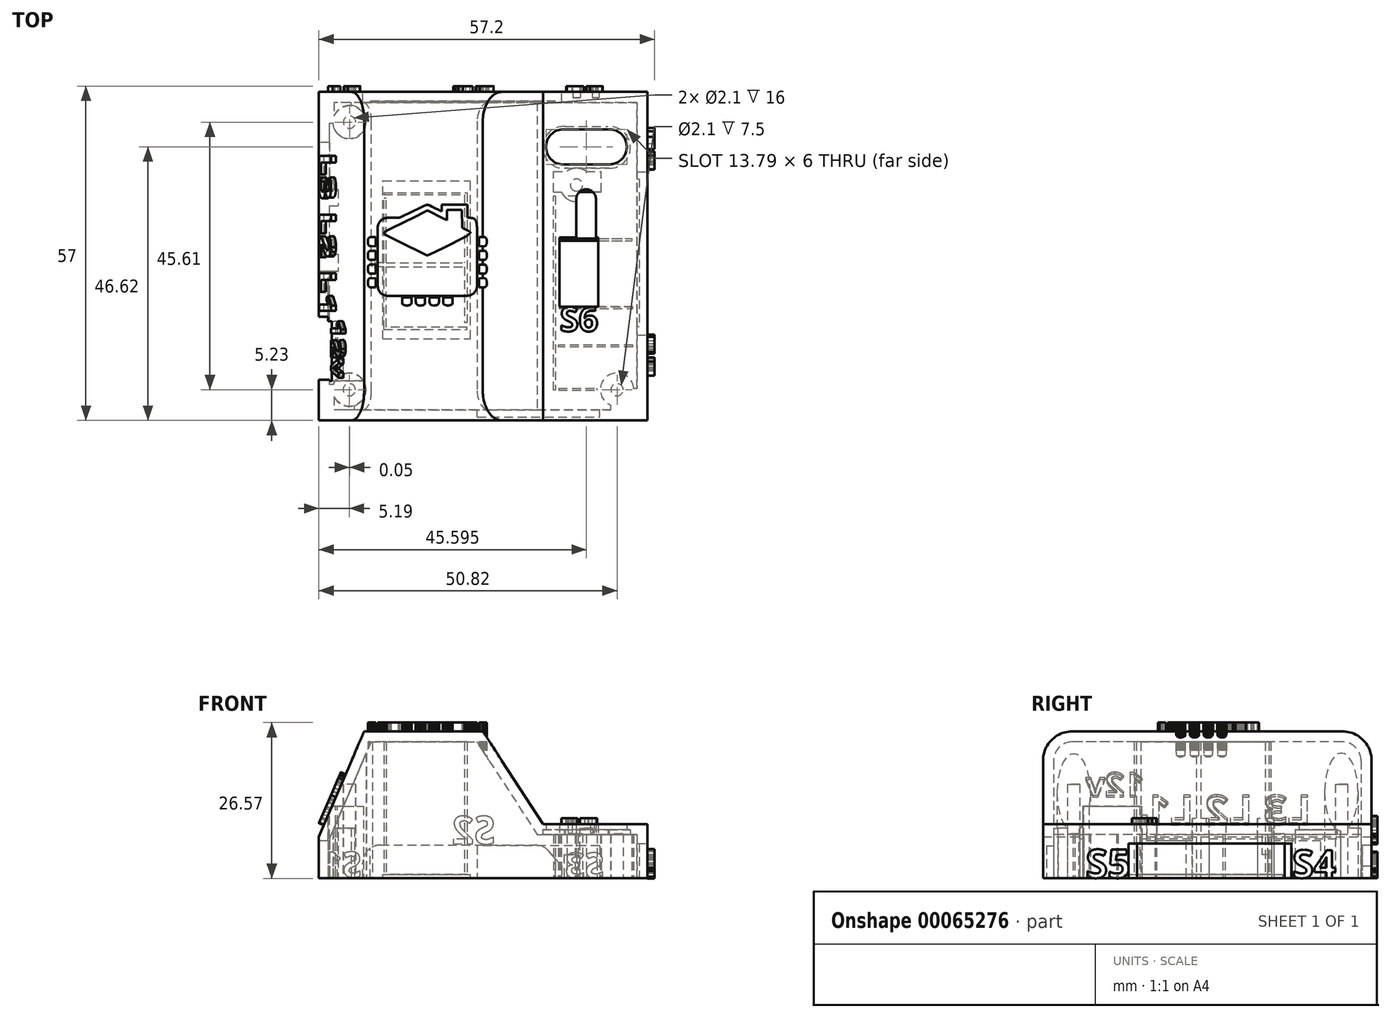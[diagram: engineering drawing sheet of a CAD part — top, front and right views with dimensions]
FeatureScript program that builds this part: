
annotation { "Feature Type Name" : "Feature", "Feature Type Description" : "" }
export const myFeature = defineFeature(function(context is Context, id is Id, definition is map)
    precondition{}
    {
        {
            var Q0;
            Q0=qCreatedBy(makeId("Top.planeOp"),FACE);
            var sketch = newSketch(context, id + "F0", { "sketchPlane" : qUnion([Q0])});
            skLineSegment(sketch, "E0.rect.bottom", {"start": v(22.84, -21.13) * mm, "end": v(-26.83, -21.13) * mm});
            skLineSegment(sketch, "E0.rect.top", {"start": v(22.84, 28.7) * mm, "end": v(-26.83, 28.7) * mm});
            skLineSegment(sketch, "E0.rect.left", {"start": v(22.84, -21.13) * mm, "end": v(22.84, 28.7) * mm});
            skPoint(sketch, "E0.rect.middle", {"position": v(-2, 3.78) * mm});
            skCircle(sketch, "E1", {"center": v(-24.81, -18.99) * mm, "radius": 1.05 * mm});
            skCircle(sketch, "E2", {"center": v(-24.76, 26.62) * mm, "radius": 1.05 * mm});
            skCircle(sketch, "E3", {"center": v(13.92, 15.91) * mm, "radius": 1.05 * mm});
            skLineSegment(sketch, "E4", {"start": v(-2, -21.13) * mm, "end": v(-2, -18.21) * mm});
            skCircle(sketch, "E5.MirrorC", {"center": v(20.82, -18.99) * mm, "radius": 1.05 * mm});
            skLineSegment(sketch, "E6.rect.bottom", {"start": v(24.75, -22.97) * mm, "end": v(-28.75, -22.97) * mm});
            skLineSegment(sketch, "E6.rect.top", {"start": v(24.75, 30.53) * mm, "end": v(-28.75, 30.53) * mm});
            skLineSegment(sketch, "E6.rect.left", {"start": v(24.75, -22.97) * mm, "end": v(24.75, 30.53) * mm});
            skLineSegment(sketch, "E6.rect.right", {"start": v(-28.75, -22.97) * mm, "end": v(-28.75, 30.53) * mm});
            skLineSegment(sketch, "E7.rect.bottom", {"start": v(26, -24.22) * mm, "end": v(-30, -24.22) * mm});
            skLineSegment(sketch, "E7.rect.top", {"start": v(26, 31.78) * mm, "end": v(-30, 31.78) * mm});
            skLineSegment(sketch, "E7.rect.left", {"start": v(26, -24.22) * mm, "end": v(26, 31.78) * mm});
            skLineSegment(sketch, "E7.rect.right", {"start": v(-30, -24.22) * mm, "end": v(-30, 31.78) * mm});
            skPoint(sketch, "E8", {"position": v(8.65, 14) * mm});
            skSolve(sketch);
        }
        {
            var Q0;
            Q0=qSketchRegion(id+"F0",true);
            var Q1;
            Q1=makeQuery(id+"F0.imprint","IMPRINT",FACE,{"disambiguationData":[TD([[makeQuery(id+"F0.imprint","IMPRINT",EDGE,{"derivedFrom":sQuery(id+"F0.wireOp",EDGE,"E1")}),-1.0]])]});
            extrude(context, id + "F1", {"entities" : qUnion([Q0, Q1]), "depth" : 25 * mm});
        }
        {
            var Q0;
            Q0=qCreatedBy(makeId("Front.planeOp"),FACE);
            var sketch = newSketch(context, id + "F2", { "sketchPlane" : qUnion([Q0])});
            skLineSegment(sketch, "E9", {"start": v(0, 0) * mm, "end": v(0, 7) * mm});
            skLineSegment(sketch, "E10", {"start": v(0, 7) * mm, "end": v(26.03, 7) * mm});
            skLineSegment(sketch, "E11", {"start": v(26.03, 9.19) * mm, "end": v(26.03, 25.51) * mm});
            skLineSegment(sketch, "E12", {"start": v(15.3, 7) * mm, "end": v(26.03, 7) * mm});
            skLineSegment(sketch, "E13", {"start": v(0, 7) * mm, "end": v(-30.02, 7) * mm});
            skLineSegment(sketch, "E14", {"start": v(-30.02, 7) * mm, "end": v(-22.06, 25.51) * mm});
            skLineSegment(sketch, "E15", {"start": v(-22.06, 25.51) * mm, "end": v(-2.39, 25.51) * mm});
            skLineSegment(sketch, "E16", {"start": v(26.03, 25.51) * mm, "end": v(-2.39, 25.51) * mm});
            skLineSegment(sketch, "E17", {"start": v(-22.06, 25.51) * mm, "end": v(-30.02, 25.51) * mm});
            skLineSegment(sketch, "E18", {"start": v(-30.02, 25.51) * mm, "end": v(-30.02, 7) * mm});
            skLineSegment(sketch, "E19", {"start": v(18.06, 10.7) * mm, "end": v(18.04, 10.7) * mm});
            skLineSegment(sketch, "E20", {"start": v(19.86, 9.19) * mm, "end": v(8.2, 9.19) * mm});
            skLineSegment(sketch, "E21", {"start": v(8.2, 9.19) * mm, "end": v(-2.39, 25.51) * mm});
            skLineSegment(sketch, "E22", {"start": v(19.86, 9.19) * mm, "end": v(26.03, 9.19) * mm});
            skSolve(sketch);
        }
        {
            var Q0;
            Q0=makeQuery(id+"F2.imprint","IMPRINT",FACE,{"disambiguationData":[TD([[makeQuery(id+"F2.imprint","IMPRINT",EDGE,{"derivedFrom":sQuery(id+"F2.wireOp",EDGE,"E14")}),1.0]])]});
            var Q1;
            {var subQ0=sQuery(id+"F2.wireOp",EDGE,"E11");Q1=makeQuery(id+"F2.imprint","IMPRINT",FACE,{"disambiguationData":[TD([[makeQuery(id+"F2.imprint","IMPRINT",EDGE,{"derivedFrom":subQ0}),1.0]])]});}
            extrude(context, id + "F3", {"entities" : qUnion([Q0, Q1]), "operationType" : NewBodyOperationType.REMOVE, "endBound" : BoundingType.UP_TO_NEXT, "oppositeDirection" : true, "depth" : 25 * mm, "hasSecondDirection" : true, "secondDirectionOppositeDirection" : false, "secondDirectionDepth" : 25 * mm});
        }
        {
            var Q0;
            Q0=makeQuery(id+"F1.opExtrude","CAP_EDGE",EDGE,{"disambiguationData":[OSD([sQuery(id+"F0.wireOp",EDGE,"E7.rect.right")])],"isStart":false});
            var Q1;
            Q1=makeQuery(id+"F3.boolean.opBoolean","COPY",EDGE,{"derivedFrom":makeQuery(id+"F3.opExtrude","TWEAK_EDGE",EDGE,{"derivedFrom":[makeQuery(id+"F1.opExtrude","CAP_FACE",FACE,{"disambiguationData":[OSD([sQuery(id+"F0.wireOp",EDGE,"E1"),sQuery(id+"F0.wireOp",EDGE,"E2"),sQuery(id+"F0.wireOp",EDGE,"E3"),sQuery(id+"F0.wireOp",EDGE,"E5.MirrorC"),sQuery(id+"F0.wireOp",EDGE,"E7.rect.bottom"),sQuery(id+"F0.wireOp",EDGE,"E7.rect.top"),sQuery(id+"F0.wireOp",EDGE,"E7.rect.left"),sQuery(id+"F0.wireOp",EDGE,"E7.rect.right")])],"isStart":false}),makeQuery(id+"F2.imprint","IMPRINT",EDGE,{"derivedFrom":sQuery(id+"F2.wireOp",EDGE,"ff17f17f-c23f-4b7b-92e3-773d52701edb")})]})});
            var Q2;
            Q2=makeQuery(id+"F3.boolean.opBoolean","COPY",EDGE,{"derivedFrom":makeQuery(id+"F3.opExtrude","TWEAK_EDGE",EDGE,{"derivedFrom":[makeQuery(id+"F1.opExtrude","CAP_FACE",FACE,{"disambiguationData":[OSD([sQuery(id+"F0.wireOp",EDGE,"E1"),sQuery(id+"F0.wireOp",EDGE,"E2"),sQuery(id+"F0.wireOp",EDGE,"E3"),sQuery(id+"F0.wireOp",EDGE,"E5.MirrorC"),sQuery(id+"F0.wireOp",EDGE,"E7.rect.bottom"),sQuery(id+"F0.wireOp",EDGE,"E7.rect.top"),sQuery(id+"F0.wireOp",EDGE,"E7.rect.left"),sQuery(id+"F0.wireOp",EDGE,"E7.rect.right")])],"isStart":false}),makeQuery(id+"F2.imprint","IMPRINT",EDGE,{"derivedFrom":sQuery(id+"F2.wireOp",EDGE,"7c30f75c-de24-4105-9ec6-0528e7197d9e")})]})});
            var Q3;
            {var subQ0=sQuery(id+"F2.wireOp",EDGE,"cpQ2IQLn-lepx-jHqE-Occg-QwCyzWVKbBFz");var subQ1=sQuery(id+"F2.wireOp",EDGE,"9136473a-ce9f-4df1-8e41-d79c079f6f02");var subQ2=makeQuery(id+"F2.imprint","INTERSECT",VERTEX,{"disambiguationData":[OD(0.0)],"derivedFrom":[subQ1,subQ0]});var subQ4=makeQuery(id+"F2.imprint","INTERSECT",VERTEX,{"disambiguationData":[OD(1.0)],"derivedFrom":[subQ1,subQ0]});Q3=makeQuery(id+"F3.boolean.opBoolean","COPY",EDGE,{"derivedFrom":makeQuery(id+"F3.opExtrude","TWEAK_EDGE",EDGE,{"derivedFrom":[makeQuery(id+"F1.opExtrude","CAP_FACE",FACE,{"disambiguationData":[OSD([sQuery(id+"F0.wireOp",EDGE,"E1"),sQuery(id+"F0.wireOp",EDGE,"E2"),sQuery(id+"F0.wireOp",EDGE,"E3"),sQuery(id+"F0.wireOp",EDGE,"E5.MirrorC"),sQuery(id+"F0.wireOp",EDGE,"E7.rect.bottom"),sQuery(id+"F0.wireOp",EDGE,"E7.rect.top"),sQuery(id+"F0.wireOp",EDGE,"E7.rect.left"),sQuery(id+"F0.wireOp",EDGE,"E7.rect.right")])],"isStart":false}),makeQuery(id+"F2.imprint","IMPRINT",EDGE,{"disambiguationData":[TD([[subQ4,1.0]])],"derivedFrom":subQ0}),makeQuery(id+"F2.imprint","IMPRINT",EDGE,{"disambiguationData":[TD([[subQ2,1.0]])],"derivedFrom":subQ0}),makeQuery(id+"F2.imprint","IMPRINT",EDGE,{"disambiguationData":[TD([[subQ2,-1.0]])],"derivedFrom":subQ0})]})});}
            var Q4;
            {var subQ0=sQuery(id+"F2.wireOp",EDGE,"cpQ2IQLn-lepx-jHqE-Occg-QwCyzWVKbBFz");var subQ1=sQuery(id+"F2.wireOp",EDGE,"9136473a-ce9f-4df1-8e41-d79c079f6f02");var subQ2=makeQuery(id+"F2.imprint","INTERSECT",VERTEX,{"disambiguationData":[OD(0.0)],"derivedFrom":[subQ1,subQ0]});var subQ3=sQuery(id+"F2.wireOp",EDGE,"7c30f75c-de24-4105-9ec6-0528e7197d9e");var subQ4=makeQuery(id+"F2.imprint","INTERSECT",VERTEX,{"derivedFrom":[subQ3,subQ0]});var subQ5=makeQuery(id+"F2.imprint","INTERSECT",VERTEX,{"disambiguationData":[OD(1.0)],"derivedFrom":[subQ1,subQ0]});Q4=makeQuery(id+"F3.boolean.opBoolean","COPY",EDGE,{"derivedFrom":makeQuery(id+"F3.opExtrude","TWEAK_EDGE",EDGE,{"disambiguationData":[OD(0.0)],"derivedFrom":[makeQuery(id+"F2.imprint","IMPRINT",EDGE,{"disambiguationData":[TD([[subQ4,1.0]])],"derivedFrom":subQ3}),makeQuery(id+"F2.imprint","IMPRINT",EDGE,{"disambiguationData":[TD([[subQ5,1.0]])],"derivedFrom":subQ0}),makeQuery(id+"F2.imprint","IMPRINT",EDGE,{"disambiguationData":[TD([[subQ2,1.0]])],"derivedFrom":subQ0}),makeQuery(id+"F2.imprint","IMPRINT",EDGE,{"disambiguationData":[TD([[subQ2,-1.0]])],"derivedFrom":subQ0})]})});}
            var Q5;
            {var subQ0=sQuery(id+"F2.wireOp",EDGE,"cpQ2IQLn-lepx-jHqE-Occg-QwCyzWVKbBFz");var subQ1=sQuery(id+"F2.wireOp",EDGE,"9136473a-ce9f-4df1-8e41-d79c079f6f02");var subQ2=makeQuery(id+"F2.imprint","INTERSECT",VERTEX,{"disambiguationData":[OD(0.0)],"derivedFrom":[subQ1,subQ0]});var subQ3=sQuery(id+"F2.wireOp",EDGE,"7c30f75c-de24-4105-9ec6-0528e7197d9e");var subQ4=makeQuery(id+"F2.imprint","INTERSECT",VERTEX,{"derivedFrom":[subQ3,subQ0]});var subQ5=makeQuery(id+"F2.imprint","INTERSECT",VERTEX,{"disambiguationData":[OD(1.0)],"derivedFrom":[subQ1,subQ0]});Q5=makeQuery(id+"F3.boolean.opBoolean","COPY",EDGE,{"derivedFrom":makeQuery(id+"F3.opExtrude","TWEAK_EDGE",EDGE,{"disambiguationData":[OD(1.0)],"derivedFrom":[makeQuery(id+"F2.imprint","IMPRINT",EDGE,{"disambiguationData":[TD([[subQ4,1.0]])],"derivedFrom":subQ3}),makeQuery(id+"F2.imprint","IMPRINT",EDGE,{"disambiguationData":[TD([[subQ5,1.0]])],"derivedFrom":subQ0}),makeQuery(id+"F2.imprint","IMPRINT",EDGE,{"disambiguationData":[TD([[subQ2,1.0]])],"derivedFrom":subQ0}),makeQuery(id+"F2.imprint","IMPRINT",EDGE,{"disambiguationData":[TD([[subQ2,-1.0]])],"derivedFrom":subQ0})]})});}
            var Q6;
            Q6=makeQuery(id+"F1.opExtrude","CAP_EDGE",EDGE,{"disambiguationData":[OSD([sQuery(id+"F0.wireOp",EDGE,"E7.rect.bottom")])],"isStart":false});
            var Q7;
            {var subQ0=sQuery(id+"F2.wireOp",EDGE,"cpQ2IQLn-lepx-jHqE-Occg-QwCyzWVKbBFz");var subQ1=sQuery(id+"F2.wireOp",EDGE,"9136473a-ce9f-4df1-8e41-d79c079f6f02");var subQ2=makeQuery(id+"F2.imprint","INTERSECT",VERTEX,{"disambiguationData":[OD(0.0)],"derivedFrom":[subQ1,subQ0]});var subQ4=makeQuery(id+"F2.imprint","INTERSECT",VERTEX,{"disambiguationData":[OD(1.0)],"derivedFrom":[subQ1,subQ0]});Q7=makeQuery(id+"F3.boolean.opBoolean","COPY",EDGE,{"derivedFrom":makeQuery(id+"F3.opExtrude","TWEAK_EDGE",EDGE,{"derivedFrom":[makeQuery(id+"F1.opExtrude","SWEPT_FACE",FACE,{"disambiguationData":[OSD([sQuery(id+"F0.wireOp",EDGE,"E7.rect.bottom")])]}),makeQuery(id+"F2.imprint","IMPRINT",EDGE,{"disambiguationData":[TD([[subQ4,1.0]])],"derivedFrom":subQ0}),makeQuery(id+"F2.imprint","IMPRINT",EDGE,{"disambiguationData":[TD([[subQ2,1.0]])],"derivedFrom":subQ0}),makeQuery(id+"F2.imprint","IMPRINT",EDGE,{"disambiguationData":[TD([[subQ2,-1.0]])],"derivedFrom":subQ0})]})});}
            var Q8;
            Q8=makeQuery(id+"F1.opExtrude","CAP_EDGE",EDGE,{"disambiguationData":[OSD([sQuery(id+"F0.wireOp",EDGE,"E7.rect.top")])],"isStart":false});
            var Q9;
            {var subQ0=sQuery(id+"F2.wireOp",EDGE,"cpQ2IQLn-lepx-jHqE-Occg-QwCyzWVKbBFz");var subQ1=sQuery(id+"F2.wireOp",EDGE,"9136473a-ce9f-4df1-8e41-d79c079f6f02");var subQ2=makeQuery(id+"F2.imprint","INTERSECT",VERTEX,{"disambiguationData":[OD(0.0)],"derivedFrom":[subQ1,subQ0]});var subQ4=makeQuery(id+"F2.imprint","INTERSECT",VERTEX,{"disambiguationData":[OD(1.0)],"derivedFrom":[subQ1,subQ0]});Q9=makeQuery(id+"F3.boolean.opBoolean","COPY",EDGE,{"derivedFrom":makeQuery(id+"F3.opExtrude","TWEAK_EDGE",EDGE,{"derivedFrom":[makeQuery(id+"F1.opExtrude","SWEPT_FACE",FACE,{"disambiguationData":[OSD([sQuery(id+"F0.wireOp",EDGE,"E7.rect.top")])]}),makeQuery(id+"F2.imprint","IMPRINT",EDGE,{"disambiguationData":[TD([[subQ4,1.0]])],"derivedFrom":subQ0}),makeQuery(id+"F2.imprint","IMPRINT",EDGE,{"disambiguationData":[TD([[subQ2,1.0]])],"derivedFrom":subQ0}),makeQuery(id+"F2.imprint","IMPRINT",EDGE,{"disambiguationData":[TD([[subQ2,-1.0]])],"derivedFrom":subQ0})]})});}
            var Q10;
            Q10=makeQuery(id+"F3.boolean.opBoolean","COPY",EDGE,{"derivedFrom":makeQuery(id+"F3.opExtrude","TWEAK_EDGE",EDGE,{"derivedFrom":[makeQuery(id+"F1.opExtrude","CAP_FACE",FACE,{"disambiguationData":[OSD([sQuery(id+"F0.wireOp",EDGE,"E1"),sQuery(id+"F0.wireOp",EDGE,"E2"),sQuery(id+"F0.wireOp",EDGE,"E3"),sQuery(id+"F0.wireOp",EDGE,"E5.MirrorC"),sQuery(id+"F0.wireOp",EDGE,"E7.rect.bottom"),sQuery(id+"F0.wireOp",EDGE,"E7.rect.top"),sQuery(id+"F0.wireOp",EDGE,"E7.rect.left"),sQuery(id+"F0.wireOp",EDGE,"E7.rect.right")])],"isStart":false}),makeQuery(id+"F2.imprint","IMPRINT",EDGE,{"derivedFrom":sQuery(id+"F2.wireOp",EDGE,"99fa5713-44e2-4710-8a3e-a5a5802f03ed")})]})});
            var Q11;
            Q11=makeQuery(id+"F3.boolean.opBoolean","COPY",EDGE,{"derivedFrom":makeQuery(id+"F3.opExtrude","TWEAK_EDGE",EDGE,{"derivedFrom":[makeQuery(id+"F1.opExtrude","CAP_FACE",FACE,{"disambiguationData":[OSD([sQuery(id+"F0.wireOp",EDGE,"E1"),sQuery(id+"F0.wireOp",EDGE,"E2"),sQuery(id+"F0.wireOp",EDGE,"E3"),sQuery(id+"F0.wireOp",EDGE,"E5.MirrorC"),sQuery(id+"F0.wireOp",EDGE,"E7.rect.bottom"),sQuery(id+"F0.wireOp",EDGE,"E7.rect.top"),sQuery(id+"F0.wireOp",EDGE,"E7.rect.left"),sQuery(id+"F0.wireOp",EDGE,"E7.rect.right")])],"isStart":false}),makeQuery(id+"F2.imprint","IMPRINT",EDGE,{"derivedFrom":sQuery(id+"F2.wireOp",EDGE,"E14")})]})});
            var Q12;
            Q12=makeQuery(id+"F3.boolean.opBoolean","COPY",EDGE,{"derivedFrom":makeQuery(id+"F3.opExtrude","TWEAK_EDGE",EDGE,{"derivedFrom":[makeQuery(id+"F1.opExtrude","CAP_FACE",FACE,{"disambiguationData":[OSD([sQuery(id+"F0.wireOp",EDGE,"E1"),sQuery(id+"F0.wireOp",EDGE,"E2"),sQuery(id+"F0.wireOp",EDGE,"E3"),sQuery(id+"F0.wireOp",EDGE,"E5.MirrorC"),sQuery(id+"F0.wireOp",EDGE,"E7.rect.bottom"),sQuery(id+"F0.wireOp",EDGE,"E7.rect.top"),sQuery(id+"F0.wireOp",EDGE,"E7.rect.left"),sQuery(id+"F0.wireOp",EDGE,"E7.rect.right")])],"isStart":false}),makeQuery(id+"F2.imprint","IMPRINT",EDGE,{"derivedFrom":sQuery(id+"F2.wireOp",EDGE,"E21")})]})});
            var Q13;
            Q13=makeQuery(id+"F3.boolean.opBoolean","COPY",EDGE,{"derivedFrom":makeQuery(id+"F3.opExtrude","TWEAK_EDGE",EDGE,{"derivedFrom":[makeQuery(id+"F2.imprint","IMPRINT",EDGE,{"derivedFrom":sQuery(id+"F2.wireOp",EDGE,"E20")}),makeQuery(id+"F2.imprint","IMPRINT",EDGE,{"derivedFrom":sQuery(id+"F2.wireOp",EDGE,"E21")})]})});
            var Q14;
            Q14=makeQuery(id+"F3.boolean.opBoolean","COPY",EDGE,{"derivedFrom":makeQuery(id+"F3.opExtrude","TWEAK_EDGE",EDGE,{"derivedFrom":[makeQuery(id+"F1.opExtrude","SWEPT_FACE",FACE,{"disambiguationData":[OSD([sQuery(id+"F0.wireOp",EDGE,"E7.rect.bottom")])]}),makeQuery(id+"F2.imprint","IMPRINT",EDGE,{"derivedFrom":sQuery(id+"F2.wireOp",EDGE,"E21")})]})});
            var Q15;
            Q15=makeQuery(id+"F3.boolean.opBoolean","COPY",EDGE,{"derivedFrom":makeQuery(id+"F3.opExtrude","TWEAK_EDGE",EDGE,{"derivedFrom":[makeQuery(id+"F1.opExtrude","SWEPT_FACE",FACE,{"disambiguationData":[OSD([sQuery(id+"F0.wireOp",EDGE,"E7.rect.top")])]}),makeQuery(id+"F2.imprint","IMPRINT",EDGE,{"derivedFrom":sQuery(id+"F2.wireOp",EDGE,"E21")})]})});
            var Q16;
            Q16=makeQuery(id+"F3.boolean.opBoolean","COPY",EDGE,{"derivedFrom":makeQuery(id+"F3.opExtrude","TWEAK_EDGE",EDGE,{"derivedFrom":[makeQuery(id+"F1.opExtrude","SWEPT_FACE",FACE,{"disambiguationData":[OSD([sQuery(id+"F0.wireOp",EDGE,"E7.rect.left")])]}),makeQuery(id+"F2.imprint","IMPRINT",EDGE,{"derivedFrom":sQuery(id+"F2.wireOp",EDGE,"E20")}),makeQuery(id+"F2.imprint","IMPRINT",EDGE,{"derivedFrom":sQuery(id+"F2.wireOp",EDGE,"E22")})]})});
            var Q17;
            Q17=makeQuery(id+"F3.boolean.opBoolean","COPY",EDGE,{"derivedFrom":makeQuery(id+"F3.opExtrude","TWEAK_EDGE",EDGE,{"derivedFrom":[makeQuery(id+"F2.imprint","IMPRINT",EDGE,{"derivedFrom":sQuery(id+"F2.wireOp",EDGE,"E20")}),makeQuery(id+"F2.imprint","IMPRINT",EDGE,{"derivedFrom":sQuery(id+"F2.wireOp",EDGE,"E21")}),makeQuery(id+"F2.imprint","IMPRINT",EDGE,{"derivedFrom":sQuery(id+"F2.wireOp",EDGE,"E22")})]})});
            fillet(context, id + "F4", {"entities" : qUnion([Q0, Q1, Q2, Q3, Q4, Q5, Q6, Q7, Q8, Q9, Q10, Q11, Q12, Q13, Q14, Q15, Q16, Q17]), "radius" : 5 * mm, "tangentPropagation" : true, "allowEdgeOverflow" : false});
        }
        {
            var Q0;
            Q0=makeQuery(id+"F1.opExtrude","SWEPT_BODY",BODY,{"disambiguationData":[OSD([sQuery(id+"F0.wireOp",EDGE,"E1"),sQuery(id+"F0.wireOp",EDGE,"E2"),sQuery(id+"F0.wireOp",EDGE,"E3"),sQuery(id+"F0.wireOp",EDGE,"E5.MirrorC"),sQuery(id+"F0.wireOp",EDGE,"E7.rect.bottom"),sQuery(id+"F0.wireOp",EDGE,"E7.rect.top"),sQuery(id+"F0.wireOp",EDGE,"E7.rect.left"),sQuery(id+"F0.wireOp",EDGE,"E7.rect.right")])]});
            transform(context, id + "F5", {"entities" : qUnion([Q0]), "transformType" : TransformType.TRANSLATION_3D, "dx" : -5 * mm, "dy" : -12 * mm, "dz" : 0 * mm, "makeCopy" : false});
        }
        {
            var Q0;
            Q0=makeQuery(id+"F1.opExtrude","CAP_FACE",FACE,{"disambiguationData":[OSD([sQuery(id+"F0.wireOp",EDGE,"E1"),sQuery(id+"F0.wireOp",EDGE,"E2"),sQuery(id+"F0.wireOp",EDGE,"E3"),sQuery(id+"F0.wireOp",EDGE,"E5.MirrorC"),sQuery(id+"F0.wireOp",EDGE,"E7.rect.bottom"),sQuery(id+"F0.wireOp",EDGE,"E7.rect.top"),sQuery(id+"F0.wireOp",EDGE,"E7.rect.left"),sQuery(id+"F0.wireOp",EDGE,"E7.rect.right")])],"isStart":true});
            shell(context, id + "F6", {"entities" : qUnion([Q0]), "thickness" : 1.8 * mm});
        }
        {
            var Q0;
            Q0=makeQuery(id+"F1.opExtrude","SWEPT_FACE",FACE,{"disambiguationData":[OSD([sQuery(id+"F0.wireOp",EDGE,"E7.rect.left")])]});
            cPlane(context, id + "F7", {"entities" : qUnion([Q0]), "cplaneType" : CPlaneType.OFFSET, "offset" : 0 * mm, "width" : 150 * mm, "height" : 150 * mm});
        }
        {
            var Q0;
            Q0=qCreatedBy(id+"F7.planeOp",FACE);
            var sketch = newSketch(context, id + "F8", { "sketchPlane" : qUnion([Q0])});
            skLineSegment(sketch, "E23.bottom", {"start": v(6.92, 0) * mm, "end": v(-20.2, 0) * mm});
            skLineSegment(sketch, "E23.top", {"start": v(6.12, 5.87) * mm, "end": v(-20.2, 5.87) * mm});
            skLineSegment(sketch, "E24", {"start": v(-20.2, 5.87) * mm, "end": v(-21.64, 5.87) * mm});
            skLineSegment(sketch, "E25", {"start": v(-21.64, 5.87) * mm, "end": v(-21.64, 0) * mm});
            skLineSegment(sketch, "E26", {"start": v(-21.64, 0) * mm, "end": v(-20.2, 0) * mm});
            skLineSegment(sketch, "E27", {"start": v(-20.2, 5.87) * mm, "end": v(-20.2, 0) * mm});
            skLineSegment(sketch, "E28", {"start": v(6.12, 5.87) * mm, "end": v(6.12, 0) * mm});
            skPoint(sketch, "E29.orphan", {"position": v(7.84, 0) * mm});
            skLineSegment(sketch, "E30", {"start": v(4.97, 0) * mm, "end": v(4.97, 5.87) * mm});
            skSolve(sketch);
        }
        {
            var Q0;
            Q0=qSketchRegion(id+"F8",true);
            extrude(context, id + "F9", {"entities" : qUnion([Q0]), "operationType" : NewBodyOperationType.REMOVE, "oppositeDirection" : true, "depth" : (1.7 - 0.3) * mm});
        }
        {
            var Q0;
            Q0=makeQuery(id+"F8.imprint","IMPRINT",FACE,{"disambiguationData":[TD([[makeQuery(id+"F8.imprint","IMPRINT",EDGE,{"derivedFrom":sQuery(id+"F8.wireOp",EDGE,"E24")}),1.0]])]});
            var Q1;
            {var subQ0=sQuery(id+"F8.wireOp",EDGE,"E23.left");Q1=makeQuery(id+"F8.imprint","IMPRINT",FACE,{"disambiguationData":[TD([[makeQuery(id+"F8.imprint","IMPRINT",EDGE,{"derivedFrom":subQ0}),1.0]])]});}
            var Q2;
            {var subQ0=sQuery(id+"F8.wireOp",EDGE,"4UiORLbo-slaH-JSft-xh6I-61qYCNnPId7j");Q2=makeQuery(id+"F8.imprint","IMPRINT",FACE,{"disambiguationData":[TD([[makeQuery(id+"F8.imprint","IMPRINT",EDGE,{"derivedFrom":subQ0}),1.0]])]});}
            var Q3;
            {var subQ0=sQuery(id+"F8.wireOp",EDGE,"E28");Q3=makeQuery(id+"F8.imprint","IMPRINT",FACE,{"disambiguationData":[TD([[makeQuery(id+"F8.imprint","IMPRINT",EDGE,{"derivedFrom":subQ0}),-1.0]])]});}
            extrude(context, id + "F10", {"entities" : qUnion([Q0, Q1, Q2, Q3]), "operationType" : NewBodyOperationType.REMOVE, "oppositeDirection" : true, "depth" : 2 * mm});
        }
        {
            var Q0;
            Q0=makeQuery(id+"F1.opExtrude","SWEPT_FACE",FACE,{"disambiguationData":[OSD([sQuery(id+"F0.wireOp",EDGE,"E7.rect.right")])]});
            cPlane(context, id + "F11", {"entities" : qUnion([Q0]), "cplaneType" : CPlaneType.OFFSET, "offset" : 0 * mm, "width" : 150 * mm, "height" : 150 * mm});
        }
        {
            var Q0;
            Q0=qCreatedBy(id+"F11.planeOp",FACE);
            var sketch = newSketch(context, id + "F12", { "sketchPlane" : qUnion([Q0])});
            skLineSegment(sketch, "E31.top", {"start": v(-11.15, 6.31) * mm, "end": v(-3.45, 6.31) * mm});
            skLineSegment(sketch, "E32", {"start": v(27.25, 11.15) * mm, "end": v(27.25, 11.15) * mm});
            skLineSegment(sketch, "E33", {"start": v(-11.15, 0) * mm, "end": v(-11.15, 6.31) * mm});
            skPoint(sketch, "E34.start.orphan", {"position": v(-15.15, 0) * mm});
            skLineSegment(sketch, "E35", {"start": v(29.28, 0) * mm, "end": v(-11.15, 0) * mm});
            skLineSegment(sketch, "E36", {"start": v(-10.29, 6.31) * mm, "end": v(-10.29, 0) * mm});
            skLineSegment(sketch, "E37", {"start": v(19.35, 12.2) * mm, "end": v(29.28, 12.2) * mm});
            skLineSegment(sketch, "E38", {"start": v(-11.15, 3.16) * mm, "end": v(-3.45, 3.16) * mm, "construction": true});
            skLineSegment(sketch, "E39", {"start": v(-3.45, 3.16) * mm, "end": v(-0.05, 3.16) * mm, "construction": true});
            skLineSegment(sketch, "E40", {"start": v(-0.05, 3.16) * mm, "end": v(7.65, 3.16) * mm, "construction": true});
            skLineSegment(sketch, "E41", {"start": v(7.65, 3.16) * mm, "end": v(11.05, 3.16) * mm, "construction": true});
            skLineSegment(sketch, "E42.trimOffspring", {"start": v(11.05, 6.31) * mm, "end": v(18.53, 6.31) * mm});
            skLineSegment(sketch, "E43", {"start": v(11.9, 6.31) * mm, "end": v(11.9, 0) * mm});
            skLineSegment(sketch, "E44", {"start": v(0, 6.31) * mm, "end": v(7.65, 6.31) * mm});
            skLineSegment(sketch, "E45", {"start": v(7.65, 0) * mm, "end": v(0, 0) * mm});
            skLineSegment(sketch, "E46", {"start": v(-3.45, 0) * mm, "end": v(-11.15, 0) * mm});
            skLineSegment(sketch, "E47", {"start": v(30.08, 0) * mm, "end": v(11.05, 0) * mm});
            skLineSegment(sketch, "E48.bottom", {"start": v(-0.32, 0) * mm, "end": v(-3.15, 0) * mm});
            skLineSegment(sketch, "E48.top", {"start": v(-0.32, 6.31) * mm, "end": v(-3.15, 6.31) * mm});
            skLineSegment(sketch, "E48.left", {"start": v(-0.32, 0) * mm, "end": v(-0.32, 6.31) * mm});
            skLineSegment(sketch, "E48.right", {"start": v(-3.15, 0) * mm, "end": v(-3.15, 6.31) * mm});
            skLineSegment(sketch, "E49.bottom", {"start": v(10.8, 0) * mm, "end": v(7.92, 0) * mm});
            skLineSegment(sketch, "E49.top", {"start": v(10.8, 6.31) * mm, "end": v(7.92, 6.31) * mm});
            skLineSegment(sketch, "E49.left", {"start": v(10.8, 0) * mm, "end": v(10.8, 6.31) * mm});
            skLineSegment(sketch, "E49.right", {"start": v(7.92, 0) * mm, "end": v(7.92, 6.31) * mm});
            skLineSegment(sketch, "E50", {"start": v(-3.45, 6.31) * mm, "end": v(11.05, 6.31) * mm});
            skLineSegment(sketch, "E51", {"start": v(29.28, 12.2) * mm, "end": v(29.28, 0) * mm});
            skPoint(sketch, "E52.end.orphan", {"position": v(30.08, 11.15) * mm});
            skPoint(sketch, "E52.start.orphan", {"position": v(30.08, 12.2) * mm});
            skLineSegment(sketch, "E53", {"start": v(18.53, 6.31) * mm, "end": v(18.53, 12.2) * mm});
            skLineSegment(sketch, "E54", {"start": v(18.53, 12.2) * mm, "end": v(19.35, 12.2) * mm});
            skPoint(sketch, "E55.start.orphan", {"position": v(19.35, 11.15) * mm});
            skPoint(sketch, "E56.end.orphan", {"position": v(19.35, 0) * mm});
            skPoint(sketch, "E56.start.orphan", {"position": v(19.35, 6.31) * mm});
            skLineSegment(sketch, "E57", {"start": v(28.38, 0) * mm, "end": v(28.38, 12.2) * mm});
            skLineSegment(sketch, "E58", {"start": v(19.35, 12.2) * mm, "end": v(19.35, 0) * mm});
            skSolve(sketch);
        }
        {
            var Q0;
            {var subQ0=sQuery(id+"F12.wireOp",EDGE,"E33");Q0=makeQuery(id+"F12.imprint","IMPRINT",FACE,{"disambiguationData":[TD([[makeQuery(id+"F12.imprint","IMPRINT",EDGE,{"derivedFrom":subQ0}),-1.0]])]});}
            var Q1;
            {var subQ1=sQuery(id+"F12.wireOp",EDGE,"E36");Q1=makeQuery(id+"F12.imprint","IMPRINT",FACE,{"disambiguationData":[TD([[makeQuery(id+"F12.imprint","IMPRINT",EDGE,{"derivedFrom":subQ1}),1.0]])]});}
            var Q2;
            {var subQ0=sQuery(id+"F12.wireOp",EDGE,"LVVauTd6-uSLQ-SWm0-nvuu-HrEgJgk2loCY");Q2=makeQuery(id+"F12.imprint","IMPRINT",FACE,{"disambiguationData":[TD([[makeQuery(id+"F12.imprint","IMPRINT",EDGE,{"derivedFrom":subQ0}),-1.0]])]});}
            var Q3;
            Q3=makeQuery(id+"F12.imprint","IMPRINT",FACE,{"disambiguationData":[TD([[makeQuery(id+"F12.imprint","IMPRINT",EDGE,{"derivedFrom":sQuery(id+"F12.wireOp",EDGE,"Bzj0w9RH-aYdH-ZF7y-Z4mK-Pif1xP8myCSu")}),1.0]])]});
            var Q4;
            {var subQ2=sQuery(id+"F12.wireOp",EDGE,"E43");Q4=makeQuery(id+"F12.imprint","IMPRINT",FACE,{"disambiguationData":[TD([[makeQuery(id+"F12.imprint","IMPRINT",EDGE,{"derivedFrom":subQ2}),1.0]])]});}
            extrude(context, id + "F13", {"entities" : qUnion([Q0, Q1, Q2, Q3, Q4]), "operationType" : NewBodyOperationType.REMOVE, "oppositeDirection" : true, "depth" : 1.6 * mm});
        }
        {
            var Q0;
            {var subQ2=sQuery(id+"F12.wireOp",EDGE,"E57");Q0=makeQuery(id+"F12.imprint","IMPRINT",FACE,{"disambiguationData":[TD([[makeQuery(id+"F12.imprint","IMPRINT",EDGE,{"derivedFrom":subQ2}),1.0]])]});}
            var Q1;
            {var subQ0=sQuery(id+"F12.wireOp",EDGE,"E33");Q1=makeQuery(id+"F12.imprint","IMPRINT",FACE,{"disambiguationData":[TD([[makeQuery(id+"F12.imprint","IMPRINT",EDGE,{"derivedFrom":subQ0}),-1.0]])]});}
            var Q2;
            {var subQ1=sQuery(id+"F12.wireOp",EDGE,"E45");Q2=makeQuery(id+"F12.imprint","IMPRINT",FACE,{"disambiguationData":[TD([[makeQuery(id+"F12.imprint","IMPRINT",EDGE,{"derivedFrom":subQ1}),-1.0]])]});}
            var Q3;
            {var subQ3=sQuery(id+"F12.wireOp",EDGE,"E36");Q3=makeQuery(id+"F12.imprint","IMPRINT",FACE,{"disambiguationData":[TD([[makeQuery(id+"F12.imprint","IMPRINT",EDGE,{"derivedFrom":subQ3}),1.0]])]});}
            var Q4;
            {var subQ3=sQuery(id+"F12.wireOp",EDGE,"E43");Q4=makeQuery(id+"F12.imprint","IMPRINT",FACE,{"disambiguationData":[TD([[makeQuery(id+"F12.imprint","IMPRINT",EDGE,{"derivedFrom":subQ3}),-1.0]])]});}
            var Q5;
            {var subQ0=sQuery(id+"F12.wireOp",EDGE,"E51");Q5=makeQuery(id+"F12.imprint","IMPRINT",FACE,{"disambiguationData":[TD([[makeQuery(id+"F12.imprint","IMPRINT",EDGE,{"derivedFrom":subQ0}),-1.0]])]});}
            extrude(context, id + "F14", {"entities" : qUnion([Q0, Q1, Q2, Q3, Q4, Q5]), "operationType" : NewBodyOperationType.REMOVE, "oppositeDirection" : true, "depth" : 8 * mm});
        }
        {
            var Q0;
            Q0=qCreatedBy(makeId("Top.planeOp"),FACE);
            var sketch = newSketch(context, id + "F15", { "sketchPlane" : qUnion([Q0])});
            skLineSegment(sketch, "E59.bottom", {"start": v(-27.19, -29.45) * mm, "end": v(-33.17, -29.45) * mm});
            skLineSegment(sketch, "E59.top", {"start": v(-27.19, -20) * mm, "end": v(-33.17, -20) * mm});
            skLineSegment(sketch, "E59.left", {"start": v(-27.19, -29.45) * mm, "end": v(-27.19, -21.32) * mm});
            skLineSegment(sketch, "E59.right", {"start": v(-33.17, -29.45) * mm, "end": v(-33.17, -21.32) * mm});
            skLineSegment(sketch, "E60", {"start": v(-33.17, -20.99) * mm, "end": v(-27.19, -20.99) * mm});
            skLineSegment(sketch, "E61", {"start": v(-33.17, -21.32) * mm, "end": v(-27.19, -21.32) * mm});
            skLineSegment(sketch, "E62.trimOffspring", {"start": v(-27.19, -20.99) * mm, "end": v(-27.19, -20) * mm});
            skLineSegment(sketch, "E63.trimOffspring", {"start": v(-33.17, -20.99) * mm, "end": v(-33.17, -20) * mm});
            skSolve(sketch);
        }
        {
            var Q0;
            Q0=qSketchRegion(id+"F15",true);
            var Q1;
            {var subQ0=sQuery(id+"F12.wireOp",EDGE,"E37");Q1=makeQuery(id+"F14.boolean.opBoolean","COPY",FACE,{"derivedFrom":makeQuery(id+"F14.opExtrude","SWEPT_FACE",FACE,{"disambiguationData":[OSD([subQ0]),TDD([makeQuery(id+"F12.imprint","IMPRINT",EDGE,{"disambiguationData":[TD([[makeQuery(id+"F12.imprint","INTERSECT",VERTEX,{"derivedFrom":[subQ0,sQuery(id+"F12.wireOp",EDGE,"E52")]}),1.0]])],"derivedFrom":subQ0})])]})});}
            extrude(context, id + "F16", {"entities" : qUnion([Q0]), "operationType" : NewBodyOperationType.REMOVE, "endBound" : BoundingType.UP_TO_SURFACE, "endBoundEntityFace" : qUnion([Q1]), "depth" : 11.3 * mm});
        }
        {
            var Q0;
            Q0=makeQuery(id+"F1.opExtrude","SWEPT_FACE",FACE,{"disambiguationData":[OSD([sQuery(id+"F0.wireOp",EDGE,"E7.rect.top")])]});
            cPlane(context, id + "F17", {"entities" : qUnion([Q0]), "cplaneType" : CPlaneType.OFFSET, "offset" : 0 * mm, "width" : 150 * mm, "height" : 150 * mm});
        }
        {
            var Q0;
            Q0=qCreatedBy(id+"F17.planeOp",FACE);
            var sketch = newSketch(context, id + "F18", { "sketchPlane" : qUnion([Q0])});
            skLineSegment(sketch, "E64.bottom", {"start": v(-6.36, 0) * mm, "end": v(27.5, 0) * mm});
            skLineSegment(sketch, "E64.left", {"start": v(-6.36, 0) * mm, "end": v(-6.36, 2.05) * mm});
            skLineSegment(sketch, "E65", {"start": v(-5.32, 3.26) * mm, "end": v(-5.32, 0) * mm});
            skLineSegment(sketch, "E66", {"start": v(27.5, 2.61) * mm, "end": v(27.5, 0) * mm});
            skLineSegment(sketch, "E67", {"start": v(26.27, 5.04) * mm, "end": v(26.27, 0) * mm});
            skPoint(sketch, "E68.visualSharp", {"position": v(-6.36, 7.05) * mm});
            skLineSegment(sketch, "E69", {"start": v(-6.36, 2.05) * mm, "end": v(-4.17, 4.58) * mm});
            skLineSegment(sketch, "E70", {"start": v(24.5, 5.61) * mm, "end": v(-1.9, 5.61) * mm});
            skPoint(sketch, "E71.visualSharp", {"position": v(-3.28, 5.61) * mm});
            skArc(sketch, "E71.filletArc", {"start": v(-1.9, 5.61) * mm, "mid": v(-3.15, 5.34) * mm, "end": v(-4.17, 4.58) * mm});
            skPoint(sketch, "E72.visualSharp", {"position": v(27.5, 5.61) * mm});
            skArc(sketch, "E72.filletArc", {"start": v(27.5, 2.61) * mm, "mid": v(26.63, 4.73) * mm, "end": v(24.5, 5.61) * mm});
            skSolve(sketch);
        }
        {
            var Q0;
            Q0=qSketchRegion(id+"F18",true);
            extrude(context, id + "F19", {"entities" : qUnion([Q0]), "operationType" : NewBodyOperationType.REMOVE, "oppositeDirection" : true, "depth" : 1.6 * mm});
        }
        {
            var Q0;
            Q0=qCreatedBy(makeId("Top.planeOp"),FACE);
            var sketch = newSketch(context, id + "F20", { "sketchPlane" : qUnion([Q0])});
            skArc(sketch, "E73", {"start": v(6.16, 2.02) * mm, "mid": v(8.9, 0.56) * mm, "end": v(11.63, 2.02) * mm});
            skLineSegment(sketch, "E74", {"start": v(11.63, 2.02) * mm, "end": v(6.16, 2.02) * mm});
            skSolve(sketch);
        }
        {
            var Q0;
            Q0=qSketchRegion(id+"F20",true);
            extrude(context, id + "F21", {"entities" : qUnion([Q0]), "operationType" : NewBodyOperationType.REMOVE, "depth" : 4 * mm});
        }
        {
            var Q0;
            {var subQ0=sQuery(id+"F18.wireOp",EDGE,"E64.left");Q0=makeQuery(id+"F18.imprint","IMPRINT",FACE,{"disambiguationData":[TD([[makeQuery(id+"F18.imprint","IMPRINT",EDGE,{"derivedFrom":subQ0}),-1.0]])]});}
            var Q1;
            {var subQ0=sQuery(id+"F18.wireOp",EDGE,"E64.right");Q1=makeQuery(id+"F18.imprint","IMPRINT",FACE,{"disambiguationData":[TD([[makeQuery(id+"F18.imprint","IMPRINT",EDGE,{"derivedFrom":subQ0}),1.0]])]});}
            extrude(context, id + "F22", {"entities" : qUnion([Q0, Q1]), "operationType" : NewBodyOperationType.REMOVE, "oppositeDirection" : true, "depth" : 2 * mm});
        }
        {
            var Q0;
            Q0=qCreatedBy(makeId("Top.planeOp"),FACE);
            var sketch = newSketch(context, id + "F23", { "sketchPlane" : qUnion([Q0])});
            skLineSegment(sketch, "E75", {"start": v(21, 19.9) * mm, "end": v(21, 10.4) * mm, "construction": true});
            skLineSegment(sketch, "E76", {"start": v(12.22, 0) * mm, "end": v(12.22, -5.06) * mm});
            skLineSegment(sketch, "E77", {"start": v(12.22, 0) * mm, "end": v(12.22, 1.5) * mm});
            skArc(sketch, "E78", {"start": v(14.47, 7.42) * mm, "mid": v(17.49, 10.4) * mm, "end": v(14.5, 13.4) * mm});
            skArc(sketch, "E79", {"start": v(6.7, 13.4) * mm, "mid": v(3.7, 10.4) * mm, "end": v(6.7, 7.4) * mm});
            skLineSegment(sketch, "E80", {"start": v(14.5, 13.4) * mm, "end": v(6.7, 13.4) * mm});
            skLineSegment(sketch, "E81", {"start": v(6.7, 7.4) * mm, "end": v(14.54, 7.42) * mm});
            skLineSegment(sketch, "E82", {"start": v(6, -5.57) * mm, "end": v(6, -16.85) * mm});
            skLineSegment(sketch, "E83", {"start": v(12.6, -16.85) * mm, "end": v(6, -16.85) * mm});
            skPoint(sketch, "E84.center.orphan", {"position": v(10.72, -16.85) * mm});
            skLineSegment(sketch, "E85", {"start": v(12.6, -5.57) * mm, "end": v(12.6, -16.85) * mm});
            skLineSegment(sketch, "E86", {"start": v(8.87, -5.06) * mm, "end": v(8.87, 1.5) * mm});
            skArc(sketch, "E87", {"start": v(12.22, 1.5) * mm, "mid": v(10.54, 3.17) * mm, "end": v(8.87, 1.5) * mm});
            skPoint(sketch, "E88.orphan", {"position": v(12.22, -16.85) * mm});
            skLineSegment(sketch, "E89", {"start": v(0, 0) * mm, "end": v(0, 19.9) * mm, "construction": true});
            skLineSegment(sketch, "E90", {"start": v(0, 19.9) * mm, "end": v(21, 19.9) * mm, "construction": true});
            skLineSegment(sketch, "E91", {"start": v(14.5, 10.4) * mm, "end": v(21, 10.4) * mm, "construction": true});
            skLineSegment(sketch, "E92", {"start": v(8.87, -5.06) * mm, "end": v(6, -5.06) * mm});
            skLineSegment(sketch, "E93", {"start": v(6, -5.06) * mm, "end": v(6, -5.57) * mm});
            skLineSegment(sketch, "E94", {"start": v(12.22, -5.06) * mm, "end": v(12.6, -5.06) * mm});
            skLineSegment(sketch, "E95", {"start": v(12.6, -5.06) * mm, "end": v(12.6, -5.57) * mm});
            skSolve(sketch);
        }
        {
            var Q0;
            Q0=qSketchRegion(id+"F23",true);
            extrude(context, id + "F24", {"entities" : qUnion([Q0]), "operationType" : NewBodyOperationType.REMOVE, "depth" : 25 * mm});
        }
        {
            var Q0;
            Q0=qCreatedBy(makeId("Top.planeOp"),FACE);
            var sketch = newSketch(context, id + "F25", { "sketchPlane" : qUnion([Q0])});
            skLineSegment(sketch, "E96", {"start": v(18.49, -17.16) * mm, "end": v(5.97, -17.16) * mm});
            skLineSegment(sketch, "E97", {"start": v(18.49, -16.86) * mm, "end": v(5.97, -16.86) * mm});
            skLineSegment(sketch, "E98", {"start": v(12.44, -31.08) * mm, "end": v(5.87, -31.08) * mm});
            skLineSegment(sketch, "E99", {"start": v(12.44, -30.78) * mm, "end": v(5.87, -30.78) * mm});
            skLineSegment(sketch, "E100.bottom", {"start": v(-33.84, 14.47) * mm, "end": v(-32.16, 14.47) * mm});
            skLineSegment(sketch, "E100.top", {"start": v(-33.84, 18.7) * mm, "end": v(-29.5, 18.7) * mm});
            skLineSegment(sketch, "E100.left", {"start": v(-33.84, 14.47) * mm, "end": v(-33.84, 18.7) * mm});
            skLineSegment(sketch, "E100.right", {"start": v(-29.5, 16.74) * mm, "end": v(-29.5, 18.7) * mm});
            skArc(sketch, "E101", {"start": v(-29.5, 16.74) * mm, "mid": v(-31.35, 16.22) * mm, "end": v(-32.16, 14.47) * mm});
            skLineSegment(sketch, "E102.bottom", {"start": v(-33.6, -31.08) * mm, "end": v(-33.6, -31.08) * mm});
            skLineSegment(sketch, "E102.top", {"start": v(-33.6, -34.81) * mm, "end": v(-31.03, -34.81) * mm});
            skLineSegment(sketch, "E102.left", {"start": v(-33.6, -31.08) * mm, "end": v(-33.6, -34.81) * mm});
            skLineSegment(sketch, "E102.right", {"start": v(-31.03, -31.08) * mm, "end": v(-31.03, -33.21) * mm});
            skLineSegment(sketch, "E103.bottom", {"start": v(-31.03, -34.81) * mm, "end": v(-28.95, -34.81) * mm});
            skLineSegment(sketch, "E103.top", {"start": v(-31.03, -33.21) * mm, "end": v(-28.95, -33.21) * mm});
            skLineSegment(sketch, "E103.right", {"start": v(-28.95, -34.81) * mm, "end": v(-28.95, -33.21) * mm});
            skPoint(sketch, "E104.end.orphan", {"position": v(-34.98, -31.08) * mm});
            skPoint(sketch, "E104.start.orphan", {"position": v(-34.98, -30.78) * mm});
            skLineSegment(sketch, "E105.bottom", {"start": v(16.87, -34.88) * mm, "end": v(19.69, -34.88) * mm});
            skLineSegment(sketch, "E105.top", {"start": v(16.87, -30.79) * mm, "end": v(19.69, -30.79) * mm});
            skLineSegment(sketch, "E105.left", {"start": v(16.87, -33.4) * mm, "end": v(16.87, -30.79) * mm});
            skLineSegment(sketch, "E105.right", {"start": v(19.69, -34.88) * mm, "end": v(19.69, -30.79) * mm});
            skLineSegment(sketch, "E106.bottom", {"start": v(16.87, -34.88) * mm, "end": v(14.73, -34.88) * mm});
            skLineSegment(sketch, "E106.top", {"start": v(16.87, -33.4) * mm, "end": v(14.73, -33.4) * mm});
            skLineSegment(sketch, "E106.right", {"start": v(14.73, -34.88) * mm, "end": v(14.73, -33.4) * mm});
            skLineSegment(sketch, "E107.top", {"start": v(-31.03, -30.09) * mm, "end": v(-33.6, -30.09) * mm});
            skLineSegment(sketch, "E107.left", {"start": v(-31.03, -31.08) * mm, "end": v(-31.03, -30.09) * mm});
            skLineSegment(sketch, "E107.right", {"start": v(-33.6, -31.08) * mm, "end": v(-33.6, -30.09) * mm});
            skLineSegment(sketch, "E108", {"start": v(5.87, -31.08) * mm, "end": v(5.87, -30.78) * mm});
            skPoint(sketch, "E109.end.orphan", {"position": v(-34.98, -17.16) * mm});
            skPoint(sketch, "E109.start.orphan", {"position": v(-34.98, -16.86) * mm});
            skLineSegment(sketch, "E110.trimOffspring", {"start": v(5.97, -17.16) * mm, "end": v(5.97, -16.86) * mm});
            skLineSegment(sketch, "E111.bottom", {"start": v(5.85, -23.4) * mm, "end": v(18.49, -23.4) * mm});
            skLineSegment(sketch, "E111.top", {"start": v(5.85, -23.7) * mm, "end": v(18.49, -23.7) * mm});
            skLineSegment(sketch, "E111.left", {"start": v(5.85, -23.4) * mm, "end": v(5.85, -23.7) * mm});
            skLineSegment(sketch, "E112", {"start": v(5.29, -31.08) * mm, "end": v(5.29, 2.03) * mm});
            skLineSegment(sketch, "E113", {"start": v(4.99, -31.08) * mm, "end": v(5.29, -31.08) * mm});
            skLineSegment(sketch, "E114", {"start": v(12.44, -30.78) * mm, "end": v(12.44, -31.08) * mm});
            skLineSegment(sketch, "E115", {"start": v(18.49, -16.86) * mm, "end": v(18.49, -17.16) * mm});
            skPoint(sketch, "E116.orphan", {"position": v(19.24, -17.16) * mm});
            skLineSegment(sketch, "E117.trimOffspring", {"start": v(18.49, -23.4) * mm, "end": v(18.49, -23.7) * mm});
            skPoint(sketch, "E118.orphan", {"position": v(19.24, -23.7) * mm});
            skLineSegment(sketch, "E119.trimOffspring", {"start": v(4.99, 2.03) * mm, "end": v(4.99, -31.08) * mm});
            skLineSegment(sketch, "E120", {"start": v(4.99, 2.03) * mm, "end": v(5.29, 2.03) * mm});
            skLineSegment(sketch, "E121.bottom", {"start": v(4.99, 2.73) * mm, "end": v(13.12, 2.73) * mm});
            skLineSegment(sketch, "E121.top", {"start": v(4.99, 6.24) * mm, "end": v(13.12, 6.24) * mm});
            skLineSegment(sketch, "E121.left", {"start": v(4.99, 2.73) * mm, "end": v(4.99, 6.24) * mm});
            skLineSegment(sketch, "E121.right", {"start": v(13.12, 2.73) * mm, "end": v(13.12, 6.24) * mm});
            skCircle(sketch, "E122", {"center": v(8.91, 3.9) * mm, "radius": 1.04 * mm});
            skPoint(sketch, "E122.first.point", {"position": v(8.9, 2.86) * mm});
            skPoint(sketch, "E122.second.point", {"position": v(8.95, 4.94) * mm});
            skPoint(sketch, "E122.third.point", {"position": v(9.95, 3.84) * mm});
            skSolve(sketch);
        }
        {
            var Q0;
            Q0=qSketchRegion(id+"F25",true);
            var Q1;
            Q1=makeQuery(id+"F6.opShell","OFFSET_FACE",FACE,{"disambiguationData":[OSD([sQuery(id+"F2.wireOp",EDGE,"E20"),sQuery(id+"F2.wireOp",EDGE,"E22")])]});
            extrude(context, id + "F26", {"entities" : qUnion([Q0]), "operationType" : NewBodyOperationType.ADD, "endBoundEntityFace" : qUnion([Q1]), "depth" : 8.5 * mm});
        }
        {
            var Q0;
            Q0=qCreatedBy(makeId("Top.planeOp"),FACE);
            var sketch = newSketch(context, id + "F27", { "sketchPlane" : qUnion([Q0])});
            skLineSegment(sketch, "E123", {"start": v(-14.06, 0.58) * mm, "end": v(-9.7, 0.57) * mm});
            skLineSegment(sketch, "E124", {"start": v(-8.04, -3.57) * mm, "end": v(-8.03, -3.84) * mm});
            skLineSegment(sketch, "E125", {"start": v(-8.03, -3.84) * mm, "end": v(-8.04, -13.15) * mm});
            skLineSegment(sketch, "E126", {"start": v(-8.04, -13.15) * mm, "end": v(-8.03, -13.22) * mm});
            skLineSegment(sketch, "E127", {"start": v(-8.03, -13.22) * mm, "end": v(-8.03, -13.28) * mm});
            skLineSegment(sketch, "E128", {"start": v(-8.03, -13.28) * mm, "end": v(-8.04, -13.35) * mm});
            skLineSegment(sketch, "E129", {"start": v(-8.04, -13.35) * mm, "end": v(-8.04, -13.42) * mm});
            skLineSegment(sketch, "E130", {"start": v(-8.04, -13.42) * mm, "end": v(-8.05, -13.48) * mm});
            skLineSegment(sketch, "E131", {"start": v(-8.05, -13.48) * mm, "end": v(-8.06, -13.55) * mm});
            skLineSegment(sketch, "E132", {"start": v(-8.06, -13.55) * mm, "end": v(-8.07, -13.61) * mm});
            skLineSegment(sketch, "E133", {"start": v(-8.07, -13.61) * mm, "end": v(-8.1, -13.68) * mm});
            skLineSegment(sketch, "E134", {"start": v(-8.1, -13.68) * mm, "end": v(-8.1, -13.74) * mm});
            skLineSegment(sketch, "E135", {"start": v(-8.1, -13.74) * mm, "end": v(-8.13, -13.8) * mm});
            skLineSegment(sketch, "E136", {"start": v(-8.13, -13.8) * mm, "end": v(-8.15, -13.86) * mm});
            skLineSegment(sketch, "E137", {"start": v(-8.15, -13.86) * mm, "end": v(-8.18, -13.93) * mm});
            skLineSegment(sketch, "E138", {"start": v(-8.18, -13.93) * mm, "end": v(-8.2, -13.99) * mm});
            skLineSegment(sketch, "E139", {"start": v(-8.2, -13.99) * mm, "end": v(-8.23, -14.05) * mm});
            skLineSegment(sketch, "E140", {"start": v(-8.23, -14.05) * mm, "end": v(-8.26, -14.1) * mm});
            skLineSegment(sketch, "E141", {"start": v(-8.26, -14.1) * mm, "end": v(-8.3, -14.16) * mm});
            skLineSegment(sketch, "E142", {"start": v(-8.3, -14.16) * mm, "end": v(-8.33, -14.22) * mm});
            skLineSegment(sketch, "E143", {"start": v(-8.33, -14.22) * mm, "end": v(-8.37, -14.27) * mm});
            skLineSegment(sketch, "E144", {"start": v(-8.37, -14.27) * mm, "end": v(-8.4, -14.32) * mm});
            skLineSegment(sketch, "E145", {"start": v(-8.4, -14.32) * mm, "end": v(-8.45, -14.37) * mm});
            skLineSegment(sketch, "E146", {"start": v(-8.45, -14.37) * mm, "end": v(-8.5, -14.42) * mm});
            skLineSegment(sketch, "E147", {"start": v(-8.5, -14.42) * mm, "end": v(-8.54, -14.47) * mm});
            skLineSegment(sketch, "E148", {"start": v(-8.54, -14.47) * mm, "end": v(-8.59, -14.52) * mm});
            skLineSegment(sketch, "E149", {"start": v(-8.59, -14.52) * mm, "end": v(-8.63, -14.56) * mm});
            skLineSegment(sketch, "E150", {"start": v(-8.63, -14.56) * mm, "end": v(-8.69, -14.6) * mm});
            skLineSegment(sketch, "E151", {"start": v(-8.69, -14.6) * mm, "end": v(-8.74, -14.64) * mm});
            skLineSegment(sketch, "E152", {"start": v(-8.74, -14.64) * mm, "end": v(-8.8, -14.68) * mm});
            skLineSegment(sketch, "E153", {"start": v(-8.8, -14.68) * mm, "end": v(-8.85, -14.72) * mm});
            skLineSegment(sketch, "E154", {"start": v(-8.85, -14.72) * mm, "end": v(-8.9, -14.75) * mm});
            skLineSegment(sketch, "E155", {"start": v(-8.9, -14.75) * mm, "end": v(-8.95, -14.77) * mm});
            skLineSegment(sketch, "E156", {"start": v(-8.95, -14.77) * mm, "end": v(-8.99, -14.8) * mm});
            skLineSegment(sketch, "E157", {"start": v(-8.99, -14.8) * mm, "end": v(-9.03, -14.81) * mm});
            skLineSegment(sketch, "E158", {"start": v(-9.03, -14.81) * mm, "end": v(-9.07, -14.83) * mm});
            skLineSegment(sketch, "E159", {"start": v(-9.07, -14.83) * mm, "end": v(-9.11, -14.85) * mm});
            skLineSegment(sketch, "E160", {"start": v(-9.11, -14.85) * mm, "end": v(-9.16, -14.86) * mm});
            skLineSegment(sketch, "E161", {"start": v(-9.16, -14.86) * mm, "end": v(-9.2, -14.88) * mm});
            skLineSegment(sketch, "E162", {"start": v(-9.2, -14.88) * mm, "end": v(-9.24, -14.9) * mm});
            skLineSegment(sketch, "E163", {"start": v(-9.24, -14.9) * mm, "end": v(-9.29, -14.9) * mm});
            skLineSegment(sketch, "E164", {"start": v(-9.29, -14.9) * mm, "end": v(-9.33, -14.91) * mm});
            skLineSegment(sketch, "E165", {"start": v(-9.33, -14.91) * mm, "end": v(-9.38, -14.92) * mm});
            skLineSegment(sketch, "E166", {"start": v(-9.38, -14.92) * mm, "end": v(-9.42, -14.93) * mm});
            skLineSegment(sketch, "E167", {"start": v(-9.42, -14.93) * mm, "end": v(-9.51, -14.94) * mm});
            skLineSegment(sketch, "E168", {"start": v(-9.51, -14.94) * mm, "end": v(-9.6, -14.96) * mm});
            skLineSegment(sketch, "E169", {"start": v(-9.6, -14.96) * mm, "end": v(-9.74, -14.97) * mm});
            skLineSegment(sketch, "E170", {"start": v(-9.74, -14.97) * mm, "end": v(-10.2, -14.98) * mm});
            skLineSegment(sketch, "E171", {"start": v(-10.2, -14.98) * mm, "end": v(-23.2, -14.97) * mm});
            skLineSegment(sketch, "E172", {"start": v(-23.2, -14.97) * mm, "end": v(-23.28, -14.97) * mm});
            skLineSegment(sketch, "E173", {"start": v(-23.28, -14.97) * mm, "end": v(-23.35, -14.97) * mm});
            skLineSegment(sketch, "E174", {"start": v(-23.35, -14.97) * mm, "end": v(-23.43, -14.97) * mm});
            skLineSegment(sketch, "E175", {"start": v(-23.43, -14.97) * mm, "end": v(-23.5, -14.96) * mm});
            skLineSegment(sketch, "E176", {"start": v(-23.5, -14.96) * mm, "end": v(-23.58, -14.94) * mm});
            skLineSegment(sketch, "E177", {"start": v(-23.58, -14.94) * mm, "end": v(-23.65, -14.93) * mm});
            skLineSegment(sketch, "E178", {"start": v(-23.65, -14.93) * mm, "end": v(-23.72, -14.9) * mm});
            skLineSegment(sketch, "E179", {"start": v(-23.72, -14.9) * mm, "end": v(-23.8, -14.89) * mm});
            skLineSegment(sketch, "E180", {"start": v(-23.8, -14.89) * mm, "end": v(-23.86, -14.86) * mm});
            skLineSegment(sketch, "E181", {"start": v(-23.86, -14.86) * mm, "end": v(-23.93, -14.83) * mm});
            skLineSegment(sketch, "E182", {"start": v(-23.93, -14.83) * mm, "end": v(-24, -14.8) * mm});
            skLineSegment(sketch, "E183", {"start": v(-24, -14.8) * mm, "end": v(-24.07, -14.77) * mm});
            skLineSegment(sketch, "E184", {"start": v(-24.07, -14.77) * mm, "end": v(-24.13, -14.73) * mm});
            skLineSegment(sketch, "E185", {"start": v(-24.13, -14.73) * mm, "end": v(-24.2, -14.7) * mm});
            skLineSegment(sketch, "E186", {"start": v(-24.2, -14.7) * mm, "end": v(-24.26, -14.65) * mm});
            skLineSegment(sketch, "E187", {"start": v(-24.26, -14.65) * mm, "end": v(-24.32, -14.6) * mm});
            skLineSegment(sketch, "E188", {"start": v(-24.32, -14.6) * mm, "end": v(-24.38, -14.56) * mm});
            skLineSegment(sketch, "E189", {"start": v(-24.38, -14.56) * mm, "end": v(-24.43, -14.51) * mm});
            skLineSegment(sketch, "E190", {"start": v(-24.43, -14.51) * mm, "end": v(-24.48, -14.46) * mm});
            skLineSegment(sketch, "E191", {"start": v(-24.48, -14.46) * mm, "end": v(-24.54, -14.4) * mm});
            skLineSegment(sketch, "E192", {"start": v(-24.54, -14.4) * mm, "end": v(-24.59, -14.35) * mm});
            skLineSegment(sketch, "E193", {"start": v(-24.59, -14.35) * mm, "end": v(-24.63, -14.3) * mm});
            skLineSegment(sketch, "E194", {"start": v(-24.63, -14.3) * mm, "end": v(-24.68, -14.23) * mm});
            skLineSegment(sketch, "E195", {"start": v(-24.68, -14.23) * mm, "end": v(-24.72, -14.17) * mm});
            skLineSegment(sketch, "E196", {"start": v(-24.72, -14.17) * mm, "end": v(-24.76, -14.1) * mm});
            skLineSegment(sketch, "E197", {"start": v(-24.76, -14.1) * mm, "end": v(-24.8, -14.04) * mm});
            skLineSegment(sketch, "E198", {"start": v(-24.8, -14.04) * mm, "end": v(-24.82, -13.97) * mm});
            skLineSegment(sketch, "E199", {"start": v(-24.82, -13.97) * mm, "end": v(-24.85, -13.9) * mm});
            skLineSegment(sketch, "E200", {"start": v(-24.85, -13.9) * mm, "end": v(-24.88, -13.83) * mm});
            skLineSegment(sketch, "E201", {"start": v(-24.88, -13.83) * mm, "end": v(-24.9, -13.76) * mm});
            skLineSegment(sketch, "E202", {"start": v(-24.9, -13.76) * mm, "end": v(-24.92, -13.66) * mm});
            skLineSegment(sketch, "E203", {"start": v(-24.92, -13.66) * mm, "end": v(-24.94, -13.55) * mm});
            skLineSegment(sketch, "E204", {"start": v(-24.94, -13.55) * mm, "end": v(-24.96, -13.38) * mm});
            skLineSegment(sketch, "E205", {"start": v(-24.96, -13.38) * mm, "end": v(-24.98, -12.8) * mm});
            skLineSegment(sketch, "E206", {"start": v(-24.98, -12.8) * mm, "end": v(-24.98, -3.92) * mm});
            skLineSegment(sketch, "E207", {"start": v(-24.98, -3.92) * mm, "end": v(-24.97, -3.38) * mm});
            skLineSegment(sketch, "E208", {"start": v(-24.97, -3.38) * mm, "end": v(-24.96, -3.24) * mm});
            skLineSegment(sketch, "E209", {"start": v(-24.96, -3.24) * mm, "end": v(-24.95, -3.15) * mm});
            skLineSegment(sketch, "E210", {"start": v(-24.95, -3.15) * mm, "end": v(-24.94, -3.1) * mm});
            skLineSegment(sketch, "E211", {"start": v(-24.94, -3.1) * mm, "end": v(-24.93, -3.06) * mm});
            skLineSegment(sketch, "E212", {"start": v(-24.93, -3.06) * mm, "end": v(-24.93, -3.02) * mm});
            skLineSegment(sketch, "E213", {"start": v(-24.93, -3.02) * mm, "end": v(-24.92, -2.97) * mm});
            skLineSegment(sketch, "E214", {"start": v(-24.92, -2.97) * mm, "end": v(-24.9, -2.93) * mm});
            skLineSegment(sketch, "E215", {"start": v(-24.9, -2.93) * mm, "end": v(-24.9, -2.88) * mm});
            skLineSegment(sketch, "E216", {"start": v(-24.9, -2.88) * mm, "end": v(-24.88, -2.84) * mm});
            skLineSegment(sketch, "E217", {"start": v(-24.88, -2.84) * mm, "end": v(-24.87, -2.8) * mm});
            skLineSegment(sketch, "E218", {"start": v(-24.87, -2.8) * mm, "end": v(-24.85, -2.76) * mm});
            skLineSegment(sketch, "E219", {"start": v(-24.85, -2.76) * mm, "end": v(-24.83, -2.71) * mm});
            skLineSegment(sketch, "E220", {"start": v(-24.83, -2.71) * mm, "end": v(-24.81, -2.67) * mm});
            skLineSegment(sketch, "E221", {"start": v(-24.81, -2.67) * mm, "end": v(-24.8, -2.63) * mm});
            skLineSegment(sketch, "E222", {"start": v(-24.8, -2.63) * mm, "end": v(-24.77, -2.58) * mm});
            skLineSegment(sketch, "E223", {"start": v(-24.77, -2.58) * mm, "end": v(-24.74, -2.53) * mm});
            skLineSegment(sketch, "E224", {"start": v(-24.74, -2.53) * mm, "end": v(-24.7, -2.48) * mm});
            skLineSegment(sketch, "E225", {"start": v(-24.7, -2.48) * mm, "end": v(-24.68, -2.43) * mm});
            skLineSegment(sketch, "E226", {"start": v(-24.68, -2.43) * mm, "end": v(-24.64, -2.38) * mm});
            skLineSegment(sketch, "E227", {"start": v(-24.64, -2.38) * mm, "end": v(-24.6, -2.34) * mm});
            skLineSegment(sketch, "E228", {"start": v(-24.6, -2.34) * mm, "end": v(-24.57, -2.3) * mm});
            skLineSegment(sketch, "E229", {"start": v(-24.57, -2.3) * mm, "end": v(-24.53, -2.25) * mm});
            skLineSegment(sketch, "E230", {"start": v(-24.53, -2.25) * mm, "end": v(-24.5, -2.2) * mm});
            skLineSegment(sketch, "E231", {"start": v(-24.5, -2.2) * mm, "end": v(-24.45, -2.16) * mm});
            skLineSegment(sketch, "E232", {"start": v(-24.45, -2.16) * mm, "end": v(-24.41, -2.12) * mm});
            skLineSegment(sketch, "E233", {"start": v(-24.41, -2.12) * mm, "end": v(-24.37, -2.08) * mm});
            skLineSegment(sketch, "E234", {"start": v(-24.37, -2.08) * mm, "end": v(-24.32, -2.05) * mm});
            skLineSegment(sketch, "E235", {"start": v(-24.32, -2.05) * mm, "end": v(-24.28, -2.01) * mm});
            skLineSegment(sketch, "E236", {"start": v(-24.28, -2.01) * mm, "end": v(-24.23, -1.98) * mm});
            skLineSegment(sketch, "E237", {"start": v(-24.23, -1.98) * mm, "end": v(-24.18, -1.94) * mm});
            skLineSegment(sketch, "E238", {"start": v(-24.18, -1.94) * mm, "end": v(-24.13, -1.91) * mm});
            skLineSegment(sketch, "E239", {"start": v(-24.13, -1.91) * mm, "end": v(-24.08, -1.88) * mm});
            skLineSegment(sketch, "E240", {"start": v(-24.08, -1.88) * mm, "end": v(-24.03, -1.86) * mm});
            skLineSegment(sketch, "E241", {"start": v(-24.03, -1.86) * mm, "end": v(-23.98, -1.83) * mm});
            skLineSegment(sketch, "E242", {"start": v(-23.98, -1.83) * mm, "end": v(-23.93, -1.8) * mm});
            skLineSegment(sketch, "E243", {"start": v(-23.93, -1.8) * mm, "end": v(-23.87, -1.79) * mm});
            skLineSegment(sketch, "E244", {"start": v(-23.87, -1.79) * mm, "end": v(-23.82, -1.77) * mm});
            skLineSegment(sketch, "E245", {"start": v(-23.82, -1.77) * mm, "end": v(-23.76, -1.75) * mm});
            skLineSegment(sketch, "E246", {"start": v(-23.76, -1.75) * mm, "end": v(-23.7, -1.73) * mm});
            skLineSegment(sketch, "E247", {"start": v(-23.7, -1.73) * mm, "end": v(-23.65, -1.72) * mm});
            skLineSegment(sketch, "E248", {"start": v(-23.65, -1.72) * mm, "end": v(-23.6, -1.71) * mm});
            skLineSegment(sketch, "E249", {"start": v(-23.6, -1.71) * mm, "end": v(-23.53, -1.7) * mm});
            skLineSegment(sketch, "E250", {"start": v(-23.53, -1.7) * mm, "end": v(-23.48, -1.7) * mm});
            skLineSegment(sketch, "E251", {"start": v(-23.48, -1.7) * mm, "end": v(-23.32, -1.69) * mm});
            skLineSegment(sketch, "E252", {"start": v(-23.32, -1.69) * mm, "end": v(-23.17, -1.68) * mm});
            skLineSegment(sketch, "E253", {"start": v(-23.17, -1.68) * mm, "end": v(-22.95, -1.67) * mm});
            skLineSegment(sketch, "E254", {"start": v(-22.95, -1.67) * mm, "end": v(-21.9, -1.67) * mm});
            skLineSegment(sketch, "E255", {"start": v(-21.9, -1.67) * mm, "end": v(-21.52, -1.67) * mm});
            skLineSegment(sketch, "E256", {"start": v(-21.52, -1.67) * mm, "end": v(-21.3, -1.66) * mm});
            skLineSegment(sketch, "E257", {"start": v(-21.3, -1.66) * mm, "end": v(-21.2, -1.64) * mm});
            skLineSegment(sketch, "E258", {"start": v(-21.2, -1.64) * mm, "end": v(-20.86, -1.5) * mm});
            skLineSegment(sketch, "E259", {"start": v(-20.86, -1.5) * mm, "end": v(-17.7, 0.02) * mm});
            skLineSegment(sketch, "E260", {"start": v(-17.7, 0.02) * mm, "end": v(-17.01, 0.36) * mm});
            skLineSegment(sketch, "E261", {"start": v(-15.75, 0.24) * mm, "end": v(-14.06, -0.59) * mm});
            skLineSegment(sketch, "E262", {"start": v(-14.06, -0.59) * mm, "end": v(-14.06, 0.58) * mm});
            skLineSegment(sketch, "E263", {"start": v(-13.15, -0.33) * mm, "end": v(-13.15, -2.1) * mm});
            skLineSegment(sketch, "E264", {"start": v(-13.15, -2.1) * mm, "end": v(-13.26, -2.06) * mm});
            skLineSegment(sketch, "E265", {"start": v(-13.26, -2.06) * mm, "end": v(-13.9, -1.75) * mm});
            skLineSegment(sketch, "E266", {"start": v(-16.83, -0.6) * mm, "end": v(-17.05, -0.71) * mm});
            skLineSegment(sketch, "E267", {"start": v(-17.05, -0.71) * mm, "end": v(-17.27, -0.83) * mm});
            skLineSegment(sketch, "E268", {"start": v(-17.27, -0.83) * mm, "end": v(-18.4, -1.4) * mm});
            skLineSegment(sketch, "E269", {"start": v(-18.4, -1.4) * mm, "end": v(-22.7, -3.51) * mm});
            skLineSegment(sketch, "E270", {"start": v(-22.7, -3.51) * mm, "end": v(-23.6, -3.97) * mm});
            skLineSegment(sketch, "E271", {"start": v(-23.6, -3.97) * mm, "end": v(-23.64, -4) * mm});
            skLineSegment(sketch, "E272", {"start": v(-23.64, -4) * mm, "end": v(-23.69, -4.02) * mm});
            skLineSegment(sketch, "E273", {"start": v(-23.69, -4.02) * mm, "end": v(-23.73, -4.05) * mm});
            skLineSegment(sketch, "E274", {"start": v(-23.73, -4.05) * mm, "end": v(-23.76, -4.08) * mm});
            skLineSegment(sketch, "E275", {"start": v(-23.76, -4.08) * mm, "end": v(-23.79, -4.1) * mm});
            skLineSegment(sketch, "E276", {"start": v(-23.79, -4.1) * mm, "end": v(-23.8, -4.13) * mm});
            skLineSegment(sketch, "E277", {"start": v(-23.8, -4.13) * mm, "end": v(-23.82, -4.15) * mm});
            skLineSegment(sketch, "E278", {"start": v(-23.82, -4.15) * mm, "end": v(-23.83, -4.16) * mm});
            skLineSegment(sketch, "E279", {"start": v(-23.83, -4.16) * mm, "end": v(-23.83, -4.18) * mm});
            skLineSegment(sketch, "E280", {"start": v(-23.83, -4.18) * mm, "end": v(-23.84, -4.2) * mm});
            skLineSegment(sketch, "E281", {"start": v(-23.84, -4.2) * mm, "end": v(-23.85, -4.21) * mm});
            skLineSegment(sketch, "E282", {"start": v(-23.85, -4.21) * mm, "end": v(-23.85, -4.23) * mm});
            skLineSegment(sketch, "E283", {"start": v(-23.85, -4.23) * mm, "end": v(-23.85, -4.25) * mm});
            skLineSegment(sketch, "E284", {"start": v(-23.85, -4.25) * mm, "end": v(-23.86, -4.27) * mm});
            skLineSegment(sketch, "E285", {"start": v(-23.86, -4.27) * mm, "end": v(-23.86, -4.29) * mm});
            skLineSegment(sketch, "E286", {"start": v(-23.86, -4.29) * mm, "end": v(-23.86, -4.3) * mm});
            skLineSegment(sketch, "E287", {"start": v(-23.86, -4.3) * mm, "end": v(-23.85, -4.32) * mm});
            skLineSegment(sketch, "E288", {"start": v(-23.85, -4.32) * mm, "end": v(-23.85, -4.34) * mm});
            skLineSegment(sketch, "E289", {"start": v(-23.85, -4.34) * mm, "end": v(-23.84, -4.36) * mm});
            skLineSegment(sketch, "E290", {"start": v(-23.84, -4.36) * mm, "end": v(-23.84, -4.38) * mm});
            skLineSegment(sketch, "E291", {"start": v(-23.84, -4.38) * mm, "end": v(-23.83, -4.4) * mm});
            skLineSegment(sketch, "E292", {"start": v(-23.83, -4.4) * mm, "end": v(-23.82, -4.42) * mm});
            skLineSegment(sketch, "E293", {"start": v(-23.82, -4.42) * mm, "end": v(-23.81, -4.44) * mm});
            skLineSegment(sketch, "E294", {"start": v(-23.81, -4.44) * mm, "end": v(-23.8, -4.45) * mm});
            skLineSegment(sketch, "E295", {"start": v(-23.8, -4.45) * mm, "end": v(-23.8, -4.47) * mm});
            skLineSegment(sketch, "E296", {"start": v(-23.8, -4.47) * mm, "end": v(-23.78, -4.48) * mm});
            skLineSegment(sketch, "E297", {"start": v(-23.78, -4.48) * mm, "end": v(-23.76, -4.5) * mm});
            skLineSegment(sketch, "E298", {"start": v(-23.76, -4.5) * mm, "end": v(-23.73, -4.53) * mm});
            skLineSegment(sketch, "E299", {"start": v(-23.73, -4.53) * mm, "end": v(-23.7, -4.55) * mm});
            skLineSegment(sketch, "E300", {"start": v(-23.7, -4.55) * mm, "end": v(-23.58, -4.62) * mm});
            skLineSegment(sketch, "E301", {"start": v(-23.58, -4.62) * mm, "end": v(-23.42, -4.7) * mm});
            skLineSegment(sketch, "E302", {"start": v(-23.42, -4.7) * mm, "end": v(-19.6, -6.6) * mm});
            skLineSegment(sketch, "E303", {"start": v(-19.6, -6.6) * mm, "end": v(-18.6, -7.09) * mm});
            skLineSegment(sketch, "E304", {"start": v(-18.6, -7.09) * mm, "end": v(-17.5, -7.65) * mm});
            skLineSegment(sketch, "E305", {"start": v(-17.5, -7.65) * mm, "end": v(-16.7, -8.03) * mm});
            skLineSegment(sketch, "E306", {"start": v(-16.7, -8.03) * mm, "end": v(-16.68, -8.04) * mm});
            skLineSegment(sketch, "E307", {"start": v(-16.68, -8.04) * mm, "end": v(-16.66, -8.05) * mm});
            skLineSegment(sketch, "E308", {"start": v(-16.66, -8.05) * mm, "end": v(-16.64, -8.06) * mm});
            skLineSegment(sketch, "E309", {"start": v(-16.64, -8.06) * mm, "end": v(-16.62, -8.06) * mm});
            skLineSegment(sketch, "E310", {"start": v(-16.62, -8.06) * mm, "end": v(-16.6, -8.07) * mm});
            skLineSegment(sketch, "E311", {"start": v(-16.6, -8.07) * mm, "end": v(-16.58, -8.07) * mm});
            skLineSegment(sketch, "E312", {"start": v(-16.58, -8.07) * mm, "end": v(-16.56, -8.07) * mm});
            skLineSegment(sketch, "E313", {"start": v(-16.56, -8.07) * mm, "end": v(-16.54, -8.07) * mm});
            skLineSegment(sketch, "E314", {"start": v(-16.54, -8.07) * mm, "end": v(-16.52, -8.08) * mm});
            skLineSegment(sketch, "E315", {"start": v(-16.52, -8.08) * mm, "end": v(-16.48, -8.07) * mm});
            skLineSegment(sketch, "E316", {"start": v(-16.48, -8.07) * mm, "end": v(-16.44, -8.07) * mm});
            skLineSegment(sketch, "E317", {"start": v(-16.44, -8.07) * mm, "end": v(-16.4, -8.06) * mm});
            skLineSegment(sketch, "E318", {"start": v(-16.4, -8.06) * mm, "end": v(-16.32, -8.04) * mm});
            skLineSegment(sketch, "E319", {"start": v(-16.32, -8.04) * mm, "end": v(-16.14, -7.96) * mm});
            skLineSegment(sketch, "E320", {"start": v(-16.14, -7.96) * mm, "end": v(-13.76, -6.78) * mm});
            skLineSegment(sketch, "E321", {"start": v(-13.76, -6.78) * mm, "end": v(-9.85, -4.84) * mm});
            skLineSegment(sketch, "E322", {"start": v(-9.4, -3.99) * mm, "end": v(-9.57, -3.89) * mm});
            skLineSegment(sketch, "E323", {"start": v(-9.57, -3.89) * mm, "end": v(-10.59, -3.4) * mm});
            skLineSegment(sketch, "E324", {"start": v(-10.59, -3.4) * mm, "end": v(-10.6, -0.33) * mm});
            skLineSegment(sketch, "E325", {"start": v(-10.6, -0.33) * mm, "end": v(-13.15, -0.33) * mm});
            skLineSegment(sketch, "E326", {"start": v(-26.34, -4.98) * mm, "end": v(-25.3, -4.97) * mm});
            skLineSegment(sketch, "E327", {"start": v(-25.3, -4.97) * mm, "end": v(-25.28, -6.53) * mm});
            skLineSegment(sketch, "E328", {"start": v(-25.28, -6.53) * mm, "end": v(-26.11, -6.52) * mm});
            skLineSegment(sketch, "E329", {"start": v(-26.11, -6.52) * mm, "end": v(-26.27, -6.5) * mm});
            skLineSegment(sketch, "E330", {"start": v(-26.27, -6.5) * mm, "end": v(-26.38, -6.49) * mm});
            skLineSegment(sketch, "E331", {"start": v(-26.38, -6.49) * mm, "end": v(-26.4, -6.47) * mm});
            skLineSegment(sketch, "E332", {"start": v(-26.4, -6.47) * mm, "end": v(-26.43, -6.45) * mm});
            skLineSegment(sketch, "E333", {"start": v(-26.43, -6.45) * mm, "end": v(-26.45, -6.43) * mm});
            skLineSegment(sketch, "E334", {"start": v(-26.45, -6.43) * mm, "end": v(-26.47, -6.41) * mm});
            skLineSegment(sketch, "E335", {"start": v(-26.47, -6.41) * mm, "end": v(-26.49, -6.39) * mm});
            skLineSegment(sketch, "E336", {"start": v(-26.49, -6.39) * mm, "end": v(-26.5, -6.37) * mm});
            skLineSegment(sketch, "E337", {"start": v(-26.5, -6.37) * mm, "end": v(-26.52, -6.34) * mm});
            skLineSegment(sketch, "E338", {"start": v(-26.52, -6.34) * mm, "end": v(-26.54, -6.32) * mm});
            skLineSegment(sketch, "E339", {"start": v(-26.54, -6.32) * mm, "end": v(-26.55, -6.29) * mm});
            skLineSegment(sketch, "E340", {"start": v(-26.55, -6.29) * mm, "end": v(-26.56, -6.26) * mm});
            skLineSegment(sketch, "E341", {"start": v(-26.56, -6.26) * mm, "end": v(-26.57, -6.23) * mm});
            skLineSegment(sketch, "E342", {"start": v(-26.57, -6.23) * mm, "end": v(-26.58, -6.2) * mm});
            skLineSegment(sketch, "E343", {"start": v(-26.58, -6.2) * mm, "end": v(-26.59, -6.18) * mm});
            skLineSegment(sketch, "E344", {"start": v(-26.59, -6.18) * mm, "end": v(-26.6, -6.15) * mm});
            skLineSegment(sketch, "E345", {"start": v(-26.6, -6.15) * mm, "end": v(-26.6, -6.09) * mm});
            skLineSegment(sketch, "E346", {"start": v(-26.6, -6.09) * mm, "end": v(-26.62, -6.03) * mm});
            skLineSegment(sketch, "E347", {"start": v(-26.62, -6.03) * mm, "end": v(-26.62, -5.9) * mm});
            skLineSegment(sketch, "E348", {"start": v(-26.62, -5.9) * mm, "end": v(-26.63, -5.75) * mm});
            skLineSegment(sketch, "E349", {"start": v(-26.63, -5.75) * mm, "end": v(-26.63, -5.7) * mm});
            skLineSegment(sketch, "E350", {"start": v(-26.63, -5.7) * mm, "end": v(-26.63, -5.62) * mm});
            skLineSegment(sketch, "E351", {"start": v(-26.63, -5.62) * mm, "end": v(-26.62, -5.5) * mm});
            skLineSegment(sketch, "E352", {"start": v(-26.62, -5.5) * mm, "end": v(-26.6, -5.42) * mm});
            skLineSegment(sketch, "E353", {"start": v(-26.6, -5.42) * mm, "end": v(-26.6, -5.36) * mm});
            skLineSegment(sketch, "E354", {"start": v(-26.6, -5.36) * mm, "end": v(-26.58, -5.3) * mm});
            skLineSegment(sketch, "E355", {"start": v(-26.58, -5.3) * mm, "end": v(-26.58, -5.28) * mm});
            skLineSegment(sketch, "E356", {"start": v(-26.58, -5.28) * mm, "end": v(-26.57, -5.25) * mm});
            skLineSegment(sketch, "E357", {"start": v(-26.57, -5.25) * mm, "end": v(-26.56, -5.23) * mm});
            skLineSegment(sketch, "E358", {"start": v(-26.56, -5.23) * mm, "end": v(-26.55, -5.2) * mm});
            skLineSegment(sketch, "E359", {"start": v(-26.55, -5.2) * mm, "end": v(-26.53, -5.18) * mm});
            skLineSegment(sketch, "E360", {"start": v(-26.53, -5.18) * mm, "end": v(-26.52, -5.15) * mm});
            skLineSegment(sketch, "E361", {"start": v(-26.52, -5.15) * mm, "end": v(-26.5, -5.13) * mm});
            skLineSegment(sketch, "E362", {"start": v(-26.5, -5.13) * mm, "end": v(-26.5, -5.1) * mm});
            skLineSegment(sketch, "E363", {"start": v(-26.5, -5.1) * mm, "end": v(-26.47, -5.09) * mm});
            skLineSegment(sketch, "E364", {"start": v(-26.47, -5.09) * mm, "end": v(-26.46, -5.07) * mm});
            skLineSegment(sketch, "E365", {"start": v(-26.46, -5.07) * mm, "end": v(-26.44, -5.05) * mm});
            skLineSegment(sketch, "E366", {"start": v(-26.44, -5.05) * mm, "end": v(-26.42, -5.03) * mm});
            skLineSegment(sketch, "E367", {"start": v(-26.42, -5.03) * mm, "end": v(-26.4, -5.01) * mm});
            skLineSegment(sketch, "E368", {"start": v(-26.4, -5.01) * mm, "end": v(-26.37, -5) * mm});
            skLineSegment(sketch, "E369", {"start": v(-26.37, -5) * mm, "end": v(-26.34, -4.98) * mm});
            skLineSegment(sketch, "E370", {"start": v(-7.72, -4.97) * mm, "end": v(-7.68, -4.98) * mm});
            skLineSegment(sketch, "E371", {"start": v(-7.68, -4.98) * mm, "end": v(-7.64, -4.98) * mm});
            skLineSegment(sketch, "E372", {"start": v(-7.64, -4.98) * mm, "end": v(-7.6, -4.98) * mm});
            skLineSegment(sketch, "E373", {"start": v(-7.6, -4.98) * mm, "end": v(-7.55, -4.98) * mm});
            skLineSegment(sketch, "E374", {"start": v(-7.55, -4.98) * mm, "end": v(-7.5, -4.98) * mm});
            skLineSegment(sketch, "E375", {"start": v(-7.5, -4.98) * mm, "end": v(-7.41, -4.97) * mm});
            skLineSegment(sketch, "E376", {"start": v(-7.41, -4.97) * mm, "end": v(-7.13, -4.95) * mm});
            skLineSegment(sketch, "E377", {"start": v(-7.13, -4.95) * mm, "end": v(-7.09, -4.94) * mm});
            skLineSegment(sketch, "E378", {"start": v(-7.09, -4.94) * mm, "end": v(-7.04, -4.94) * mm});
            skLineSegment(sketch, "E379", {"start": v(-7.04, -4.94) * mm, "end": v(-7, -4.94) * mm});
            skLineSegment(sketch, "E380", {"start": v(-7, -4.94) * mm, "end": v(-6.95, -4.94) * mm});
            skLineSegment(sketch, "E381", {"start": v(-6.95, -4.94) * mm, "end": v(-6.9, -4.94) * mm});
            skLineSegment(sketch, "E382", {"start": v(-6.9, -4.94) * mm, "end": v(-6.86, -4.95) * mm});
            skLineSegment(sketch, "E383", {"start": v(-6.86, -4.95) * mm, "end": v(-6.82, -4.95) * mm});
            skLineSegment(sketch, "E384", {"start": v(-6.82, -4.95) * mm, "end": v(-6.78, -4.96) * mm});
            skLineSegment(sketch, "E385", {"start": v(-6.78, -4.96) * mm, "end": v(-6.74, -4.97) * mm});
            skLineSegment(sketch, "E386", {"start": v(-6.74, -4.97) * mm, "end": v(-6.7, -4.99) * mm});
            skLineSegment(sketch, "E387", {"start": v(-6.7, -4.99) * mm, "end": v(-6.66, -5) * mm});
            skLineSegment(sketch, "E388", {"start": v(-6.66, -5) * mm, "end": v(-6.62, -5.03) * mm});
            skLineSegment(sketch, "E389", {"start": v(-6.62, -5.03) * mm, "end": v(-6.58, -5.05) * mm});
            skLineSegment(sketch, "E390", {"start": v(-6.58, -5.05) * mm, "end": v(-6.55, -5.08) * mm});
            skLineSegment(sketch, "E391", {"start": v(-6.55, -5.08) * mm, "end": v(-6.52, -5.1) * mm});
            skLineSegment(sketch, "E392", {"start": v(-6.52, -5.1) * mm, "end": v(-6.48, -5.14) * mm});
            skLineSegment(sketch, "E393", {"start": v(-6.48, -5.14) * mm, "end": v(-6.47, -5.18) * mm});
            skLineSegment(sketch, "E394", {"start": v(-6.47, -5.18) * mm, "end": v(-6.46, -5.21) * mm});
            skLineSegment(sketch, "E395", {"start": v(-6.46, -5.21) * mm, "end": v(-6.45, -5.24) * mm});
            skLineSegment(sketch, "E396", {"start": v(-6.45, -5.24) * mm, "end": v(-6.43, -5.31) * mm});
            skLineSegment(sketch, "E397", {"start": v(-6.43, -5.31) * mm, "end": v(-6.41, -5.38) * mm});
            skLineSegment(sketch, "E398", {"start": v(-6.41, -5.38) * mm, "end": v(-6.4, -5.45) * mm});
            skLineSegment(sketch, "E399", {"start": v(-6.4, -5.45) * mm, "end": v(-6.4, -5.52) * mm});
            skLineSegment(sketch, "E400", {"start": v(-6.4, -5.52) * mm, "end": v(-6.39, -5.59) * mm});
            skLineSegment(sketch, "E401", {"start": v(-6.39, -5.59) * mm, "end": v(-6.38, -5.7) * mm});
            skLineSegment(sketch, "E402", {"start": v(-6.38, -5.7) * mm, "end": v(-6.39, -5.83) * mm});
            skLineSegment(sketch, "E403", {"start": v(-6.39, -5.83) * mm, "end": v(-6.4, -6.08) * mm});
            skLineSegment(sketch, "E404", {"start": v(-6.4, -6.08) * mm, "end": v(-6.42, -6.15) * mm});
            skLineSegment(sketch, "E405", {"start": v(-6.42, -6.15) * mm, "end": v(-6.47, -6.3) * mm});
            skLineSegment(sketch, "E406", {"start": v(-6.47, -6.3) * mm, "end": v(-6.5, -6.36) * mm});
            skLineSegment(sketch, "E407", {"start": v(-6.5, -6.36) * mm, "end": v(-6.53, -6.4) * mm});
            skLineSegment(sketch, "E408", {"start": v(-6.53, -6.4) * mm, "end": v(-6.56, -6.43) * mm});
            skLineSegment(sketch, "E409", {"start": v(-6.56, -6.43) * mm, "end": v(-6.59, -6.46) * mm});
            skLineSegment(sketch, "E410", {"start": v(-6.59, -6.46) * mm, "end": v(-6.61, -6.47) * mm});
            skLineSegment(sketch, "E411", {"start": v(-6.61, -6.47) * mm, "end": v(-6.64, -6.49) * mm});
            skLineSegment(sketch, "E412", {"start": v(-6.64, -6.49) * mm, "end": v(-6.67, -6.5) * mm});
            skLineSegment(sketch, "E413", {"start": v(-6.67, -6.5) * mm, "end": v(-7.74, -6.53) * mm});
            skLineSegment(sketch, "E414", {"start": v(-7.74, -6.53) * mm, "end": v(-7.72, -4.97) * mm});
            skLineSegment(sketch, "E415", {"start": v(-26.35, -7.32) * mm, "end": v(-25.28, -7.3) * mm});
            skLineSegment(sketch, "E416", {"start": v(-25.28, -7.3) * mm, "end": v(-25.28, -8.87) * mm});
            skLineSegment(sketch, "E417", {"start": v(-25.28, -8.87) * mm, "end": v(-26.35, -8.85) * mm});
            skLineSegment(sketch, "E418", {"start": v(-26.35, -8.85) * mm, "end": v(-26.5, -8.7) * mm});
            skLineSegment(sketch, "E419", {"start": v(-26.5, -8.7) * mm, "end": v(-26.55, -8.62) * mm});
            skLineSegment(sketch, "E420", {"start": v(-26.55, -8.62) * mm, "end": v(-26.57, -8.57) * mm});
            skLineSegment(sketch, "E421", {"start": v(-26.57, -8.57) * mm, "end": v(-26.6, -8.52) * mm});
            skLineSegment(sketch, "E422", {"start": v(-26.6, -8.52) * mm, "end": v(-26.6, -8.47) * mm});
            skLineSegment(sketch, "E423", {"start": v(-26.6, -8.47) * mm, "end": v(-26.6, -8.45) * mm});
            skLineSegment(sketch, "E424", {"start": v(-26.6, -8.45) * mm, "end": v(-26.61, -8.37) * mm});
            skLineSegment(sketch, "E425", {"start": v(-26.61, -8.37) * mm, "end": v(-26.63, -8.2) * mm});
            skLineSegment(sketch, "E426", {"start": v(-26.63, -8.2) * mm, "end": v(-26.63, -8.08) * mm});
            skLineSegment(sketch, "E427", {"start": v(-26.63, -8.08) * mm, "end": v(-26.64, -8) * mm});
            skLineSegment(sketch, "E428", {"start": v(-26.64, -8) * mm, "end": v(-26.64, -7.95) * mm});
            skLineSegment(sketch, "E429", {"start": v(-26.64, -7.95) * mm, "end": v(-26.63, -7.9) * mm});
            skLineSegment(sketch, "E430", {"start": v(-26.63, -7.9) * mm, "end": v(-26.63, -7.86) * mm});
            skLineSegment(sketch, "E431", {"start": v(-26.63, -7.86) * mm, "end": v(-26.63, -7.82) * mm});
            skLineSegment(sketch, "E432", {"start": v(-26.63, -7.82) * mm, "end": v(-26.62, -7.78) * mm});
            skLineSegment(sketch, "E433", {"start": v(-26.62, -7.78) * mm, "end": v(-26.61, -7.74) * mm});
            skLineSegment(sketch, "E434", {"start": v(-26.61, -7.74) * mm, "end": v(-26.6, -7.7) * mm});
            skLineSegment(sketch, "E435", {"start": v(-26.6, -7.7) * mm, "end": v(-26.6, -7.66) * mm});
            skLineSegment(sketch, "E436", {"start": v(-26.6, -7.66) * mm, "end": v(-26.58, -7.62) * mm});
            skLineSegment(sketch, "E437", {"start": v(-26.58, -7.62) * mm, "end": v(-26.56, -7.58) * mm});
            skLineSegment(sketch, "E438", {"start": v(-26.56, -7.58) * mm, "end": v(-26.55, -7.54) * mm});
            skLineSegment(sketch, "E439", {"start": v(-26.55, -7.54) * mm, "end": v(-26.53, -7.5) * mm});
            skLineSegment(sketch, "E440", {"start": v(-26.53, -7.5) * mm, "end": v(-26.5, -7.47) * mm});
            skLineSegment(sketch, "E441", {"start": v(-26.5, -7.47) * mm, "end": v(-26.48, -7.44) * mm});
            skLineSegment(sketch, "E442", {"start": v(-26.48, -7.44) * mm, "end": v(-26.45, -7.4) * mm});
            skLineSegment(sketch, "E443", {"start": v(-26.45, -7.4) * mm, "end": v(-26.42, -7.38) * mm});
            skLineSegment(sketch, "E444", {"start": v(-26.42, -7.38) * mm, "end": v(-26.39, -7.35) * mm});
            skLineSegment(sketch, "E445", {"start": v(-26.39, -7.35) * mm, "end": v(-26.35, -7.32) * mm});
            skLineSegment(sketch, "E446", {"start": v(-7.73, -7.3) * mm, "end": v(-6.66, -7.32) * mm});
            skLineSegment(sketch, "E447", {"start": v(-6.66, -7.32) * mm, "end": v(-6.53, -7.44) * mm});
            skLineSegment(sketch, "E448", {"start": v(-6.53, -7.44) * mm, "end": v(-6.47, -7.53) * mm});
            skLineSegment(sketch, "E449", {"start": v(-6.47, -7.53) * mm, "end": v(-6.44, -7.58) * mm});
            skLineSegment(sketch, "E450", {"start": v(-6.44, -7.58) * mm, "end": v(-6.43, -7.63) * mm});
            skLineSegment(sketch, "E451", {"start": v(-6.43, -7.63) * mm, "end": v(-6.41, -7.68) * mm});
            skLineSegment(sketch, "E452", {"start": v(-6.41, -7.68) * mm, "end": v(-6.4, -7.7) * mm});
            skLineSegment(sketch, "E453", {"start": v(-6.4, -7.7) * mm, "end": v(-6.4, -7.79) * mm});
            skLineSegment(sketch, "E454", {"start": v(-6.4, -7.79) * mm, "end": v(-6.39, -7.96) * mm});
            skLineSegment(sketch, "E455", {"start": v(-6.39, -7.96) * mm, "end": v(-6.38, -8.09) * mm});
            skLineSegment(sketch, "E456", {"start": v(-6.38, -8.09) * mm, "end": v(-6.38, -8.17) * mm});
            skLineSegment(sketch, "E457", {"start": v(-6.38, -8.17) * mm, "end": v(-6.38, -8.22) * mm});
            skLineSegment(sketch, "E458", {"start": v(-6.38, -8.22) * mm, "end": v(-6.38, -8.26) * mm});
            skLineSegment(sketch, "E459", {"start": v(-6.38, -8.26) * mm, "end": v(-6.38, -8.3) * mm});
            skLineSegment(sketch, "E460", {"start": v(-6.38, -8.3) * mm, "end": v(-6.39, -8.34) * mm});
            skLineSegment(sketch, "E461", {"start": v(-6.39, -8.34) * mm, "end": v(-6.4, -8.39) * mm});
            skLineSegment(sketch, "E462", {"start": v(-6.4, -8.39) * mm, "end": v(-6.4, -8.43) * mm});
            skLineSegment(sketch, "E463", {"start": v(-6.4, -8.43) * mm, "end": v(-6.4, -8.47) * mm});
            skLineSegment(sketch, "E464", {"start": v(-6.4, -8.47) * mm, "end": v(-6.42, -8.5) * mm});
            skLineSegment(sketch, "E465", {"start": v(-6.42, -8.5) * mm, "end": v(-6.43, -8.55) * mm});
            skLineSegment(sketch, "E466", {"start": v(-6.43, -8.55) * mm, "end": v(-6.45, -8.58) * mm});
            skLineSegment(sketch, "E467", {"start": v(-6.45, -8.58) * mm, "end": v(-6.47, -8.62) * mm});
            skLineSegment(sketch, "E468", {"start": v(-6.47, -8.62) * mm, "end": v(-6.49, -8.66) * mm});
            skLineSegment(sketch, "E469", {"start": v(-6.49, -8.66) * mm, "end": v(-6.5, -8.7) * mm});
            skLineSegment(sketch, "E470", {"start": v(-6.5, -8.7) * mm, "end": v(-6.53, -8.73) * mm});
            skLineSegment(sketch, "E471", {"start": v(-6.53, -8.73) * mm, "end": v(-6.56, -8.76) * mm});
            skLineSegment(sketch, "E472", {"start": v(-6.56, -8.76) * mm, "end": v(-6.6, -8.79) * mm});
            skLineSegment(sketch, "E473", {"start": v(-6.6, -8.79) * mm, "end": v(-6.62, -8.82) * mm});
            skLineSegment(sketch, "E474", {"start": v(-6.62, -8.82) * mm, "end": v(-6.66, -8.85) * mm});
            skLineSegment(sketch, "E475", {"start": v(-6.66, -8.85) * mm, "end": v(-7.73, -8.87) * mm});
            skLineSegment(sketch, "E476", {"start": v(-7.73, -8.87) * mm, "end": v(-7.73, -7.3) * mm});
            skLineSegment(sketch, "E477", {"start": v(-26.38, -9.67) * mm, "end": v(-26.27, -9.66) * mm});
            skLineSegment(sketch, "E478", {"start": v(-26.27, -9.66) * mm, "end": v(-26.08, -9.64) * mm});
            skLineSegment(sketch, "E479", {"start": v(-26.08, -9.64) * mm, "end": v(-25.28, -9.63) * mm});
            skLineSegment(sketch, "E480", {"start": v(-25.28, -9.63) * mm, "end": v(-25.3, -11.2) * mm});
            skLineSegment(sketch, "E481", {"start": v(-25.3, -11.2) * mm, "end": v(-26.03, -11.2) * mm});
            skLineSegment(sketch, "E482", {"start": v(-26.03, -11.2) * mm, "end": v(-26.17, -11.2) * mm});
            skLineSegment(sketch, "E483", {"start": v(-26.17, -11.2) * mm, "end": v(-26.27, -11.19) * mm});
            skLineSegment(sketch, "E484", {"start": v(-26.27, -11.19) * mm, "end": v(-26.3, -11.18) * mm});
            skLineSegment(sketch, "E485", {"start": v(-26.3, -11.18) * mm, "end": v(-26.34, -11.17) * mm});
            skLineSegment(sketch, "E486", {"start": v(-26.34, -11.17) * mm, "end": v(-26.36, -11.16) * mm});
            skLineSegment(sketch, "E487", {"start": v(-26.36, -11.16) * mm, "end": v(-26.39, -11.15) * mm});
            skLineSegment(sketch, "E488", {"start": v(-26.39, -11.15) * mm, "end": v(-26.41, -11.13) * mm});
            skLineSegment(sketch, "E489", {"start": v(-26.41, -11.13) * mm, "end": v(-26.43, -11.11) * mm});
            skLineSegment(sketch, "E490", {"start": v(-26.43, -11.11) * mm, "end": v(-26.46, -11.1) * mm});
            skLineSegment(sketch, "E491", {"start": v(-26.46, -11.1) * mm, "end": v(-26.47, -11.08) * mm});
            skLineSegment(sketch, "E492", {"start": v(-26.47, -11.08) * mm, "end": v(-26.5, -11.05) * mm});
            skLineSegment(sketch, "E493", {"start": v(-26.5, -11.05) * mm, "end": v(-26.5, -11.03) * mm});
            skLineSegment(sketch, "E494", {"start": v(-26.5, -11.03) * mm, "end": v(-26.52, -11) * mm});
            skLineSegment(sketch, "E495", {"start": v(-26.52, -11) * mm, "end": v(-26.54, -10.98) * mm});
            skLineSegment(sketch, "E496", {"start": v(-26.54, -10.98) * mm, "end": v(-26.55, -10.95) * mm});
            skLineSegment(sketch, "E497", {"start": v(-26.55, -10.95) * mm, "end": v(-26.56, -10.93) * mm});
            skLineSegment(sketch, "E498", {"start": v(-26.56, -10.93) * mm, "end": v(-26.57, -10.9) * mm});
            skLineSegment(sketch, "E499", {"start": v(-26.57, -10.9) * mm, "end": v(-26.58, -10.87) * mm});
            skLineSegment(sketch, "E500", {"start": v(-26.58, -10.87) * mm, "end": v(-26.59, -10.84) * mm});
            skLineSegment(sketch, "E501", {"start": v(-26.59, -10.84) * mm, "end": v(-26.6, -10.78) * mm});
            skLineSegment(sketch, "E502", {"start": v(-26.6, -10.78) * mm, "end": v(-26.61, -10.72) * mm});
            skLineSegment(sketch, "E503", {"start": v(-26.61, -10.72) * mm, "end": v(-26.62, -10.63) * mm});
            skLineSegment(sketch, "E504", {"start": v(-26.62, -10.63) * mm, "end": v(-26.63, -10.55) * mm});
            skLineSegment(sketch, "E505", {"start": v(-26.63, -10.55) * mm, "end": v(-26.63, -10.5) * mm});
            skLineSegment(sketch, "E506", {"start": v(-26.63, -10.5) * mm, "end": v(-26.63, -10.47) * mm});
            skLineSegment(sketch, "E507", {"start": v(-26.63, -10.47) * mm, "end": v(-26.63, -10.38) * mm});
            skLineSegment(sketch, "E508", {"start": v(-26.63, -10.38) * mm, "end": v(-26.62, -10.23) * mm});
            skLineSegment(sketch, "E509", {"start": v(-26.62, -10.23) * mm, "end": v(-26.62, -10.14) * mm});
            skLineSegment(sketch, "E510", {"start": v(-26.62, -10.14) * mm, "end": v(-26.6, -10.08) * mm});
            skLineSegment(sketch, "E511", {"start": v(-26.6, -10.08) * mm, "end": v(-26.6, -10.02) * mm});
            skLineSegment(sketch, "E512", {"start": v(-26.6, -10.02) * mm, "end": v(-26.59, -9.99) * mm});
            skLineSegment(sketch, "E513", {"start": v(-26.59, -9.99) * mm, "end": v(-26.58, -9.96) * mm});
            skLineSegment(sketch, "E514", {"start": v(-26.58, -9.96) * mm, "end": v(-26.57, -9.93) * mm});
            skLineSegment(sketch, "E515", {"start": v(-26.57, -9.93) * mm, "end": v(-26.56, -9.9) * mm});
            skLineSegment(sketch, "E516", {"start": v(-26.56, -9.9) * mm, "end": v(-26.55, -9.87) * mm});
            skLineSegment(sketch, "E517", {"start": v(-26.55, -9.87) * mm, "end": v(-26.54, -9.85) * mm});
            skLineSegment(sketch, "E518", {"start": v(-26.54, -9.85) * mm, "end": v(-26.52, -9.82) * mm});
            skLineSegment(sketch, "E519", {"start": v(-26.52, -9.82) * mm, "end": v(-26.5, -9.8) * mm});
            skLineSegment(sketch, "E520", {"start": v(-26.5, -9.8) * mm, "end": v(-26.49, -9.77) * mm});
            skLineSegment(sketch, "E521", {"start": v(-26.49, -9.77) * mm, "end": v(-26.47, -9.75) * mm});
            skLineSegment(sketch, "E522", {"start": v(-26.47, -9.75) * mm, "end": v(-26.45, -9.73) * mm});
            skLineSegment(sketch, "E523", {"start": v(-26.45, -9.73) * mm, "end": v(-26.43, -9.71) * mm});
            skLineSegment(sketch, "E524", {"start": v(-26.43, -9.71) * mm, "end": v(-26.4, -9.7) * mm});
            skLineSegment(sketch, "E525", {"start": v(-26.4, -9.7) * mm, "end": v(-26.38, -9.67) * mm});
            skLineSegment(sketch, "E526", {"start": v(-7.73, -9.64) * mm, "end": v(-6.54, -9.67) * mm});
            skLineSegment(sketch, "E527", {"start": v(-6.54, -9.67) * mm, "end": v(-6.51, -9.75) * mm});
            skLineSegment(sketch, "E528", {"start": v(-6.51, -9.75) * mm, "end": v(-6.48, -9.83) * mm});
            skLineSegment(sketch, "E529", {"start": v(-6.48, -9.83) * mm, "end": v(-6.46, -9.9) * mm});
            skLineSegment(sketch, "E530", {"start": v(-6.46, -9.9) * mm, "end": v(-6.44, -9.99) * mm});
            skLineSegment(sketch, "E531", {"start": v(-6.44, -9.99) * mm, "end": v(-6.42, -10.07) * mm});
            skLineSegment(sketch, "E532", {"start": v(-6.42, -10.07) * mm, "end": v(-6.4, -10.15) * mm});
            skLineSegment(sketch, "E533", {"start": v(-6.4, -10.15) * mm, "end": v(-6.4, -10.23) * mm});
            skLineSegment(sketch, "E534", {"start": v(-6.4, -10.23) * mm, "end": v(-6.39, -10.32) * mm});
            skLineSegment(sketch, "E535", {"start": v(-6.39, -10.32) * mm, "end": v(-6.38, -10.4) * mm});
            skLineSegment(sketch, "E536", {"start": v(-6.38, -10.4) * mm, "end": v(-6.38, -10.44) * mm});
            skLineSegment(sketch, "E537", {"start": v(-6.38, -10.44) * mm, "end": v(-6.38, -10.48) * mm});
            skLineSegment(sketch, "E538", {"start": v(-6.38, -10.48) * mm, "end": v(-6.38, -10.53) * mm});
            skLineSegment(sketch, "E539", {"start": v(-6.38, -10.53) * mm, "end": v(-6.39, -10.57) * mm});
            skLineSegment(sketch, "E540", {"start": v(-6.39, -10.57) * mm, "end": v(-6.39, -10.6) * mm});
            skLineSegment(sketch, "E541", {"start": v(-6.39, -10.6) * mm, "end": v(-6.4, -10.65) * mm});
            skLineSegment(sketch, "E542", {"start": v(-6.4, -10.65) * mm, "end": v(-6.4, -10.7) * mm});
            skLineSegment(sketch, "E543", {"start": v(-6.4, -10.7) * mm, "end": v(-6.4, -10.73) * mm});
            skLineSegment(sketch, "E544", {"start": v(-6.4, -10.73) * mm, "end": v(-6.41, -10.77) * mm});
            skLineSegment(sketch, "E545", {"start": v(-6.41, -10.77) * mm, "end": v(-6.42, -10.82) * mm});
            skLineSegment(sketch, "E546", {"start": v(-6.42, -10.82) * mm, "end": v(-6.43, -10.86) * mm});
            skLineSegment(sketch, "E547", {"start": v(-6.43, -10.86) * mm, "end": v(-6.45, -10.92) * mm});
            skLineSegment(sketch, "E548", {"start": v(-6.45, -10.92) * mm, "end": v(-6.47, -10.97) * mm});
            skLineSegment(sketch, "E549", {"start": v(-6.47, -10.97) * mm, "end": v(-6.5, -11.03) * mm});
            skLineSegment(sketch, "E550", {"start": v(-6.5, -11.03) * mm, "end": v(-6.53, -11.07) * mm});
            skLineSegment(sketch, "E551", {"start": v(-6.53, -11.07) * mm, "end": v(-6.56, -11.1) * mm});
            skLineSegment(sketch, "E552", {"start": v(-6.56, -11.1) * mm, "end": v(-6.58, -11.12) * mm});
            skLineSegment(sketch, "E553", {"start": v(-6.58, -11.12) * mm, "end": v(-6.6, -11.14) * mm});
            skLineSegment(sketch, "E554", {"start": v(-6.6, -11.14) * mm, "end": v(-6.64, -11.15) * mm});
            skLineSegment(sketch, "E555", {"start": v(-6.64, -11.15) * mm, "end": v(-6.66, -11.17) * mm});
            skLineSegment(sketch, "E556", {"start": v(-6.66, -11.17) * mm, "end": v(-6.7, -11.18) * mm});
            skLineSegment(sketch, "E557", {"start": v(-6.7, -11.18) * mm, "end": v(-6.7, -11.18) * mm});
            skLineSegment(sketch, "E558", {"start": v(-6.7, -11.18) * mm, "end": v(-7.72, -11.2) * mm});
            skLineSegment(sketch, "E559", {"start": v(-7.72, -11.2) * mm, "end": v(-7.73, -9.64) * mm});
            skLineSegment(sketch, "E560", {"start": v(-26.47, -12.01) * mm, "end": v(-25.28, -11.98) * mm});
            skLineSegment(sketch, "E561", {"start": v(-25.28, -11.98) * mm, "end": v(-25.3, -13.53) * mm});
            skLineSegment(sketch, "E562", {"start": v(-25.3, -13.53) * mm, "end": v(-25.33, -13.53) * mm});
            skLineSegment(sketch, "E563", {"start": v(-25.33, -13.53) * mm, "end": v(-25.38, -13.52) * mm});
            skLineSegment(sketch, "E564", {"start": v(-25.38, -13.52) * mm, "end": v(-25.42, -13.52) * mm});
            skLineSegment(sketch, "E565", {"start": v(-25.42, -13.52) * mm, "end": v(-25.47, -13.52) * mm});
            skLineSegment(sketch, "E566", {"start": v(-25.47, -13.52) * mm, "end": v(-25.5, -13.52) * mm});
            skLineSegment(sketch, "E567", {"start": v(-25.5, -13.52) * mm, "end": v(-25.6, -13.53) * mm});
            skLineSegment(sketch, "E568", {"start": v(-25.6, -13.53) * mm, "end": v(-25.88, -13.56) * mm});
            skLineSegment(sketch, "E569", {"start": v(-25.88, -13.56) * mm, "end": v(-25.93, -13.56) * mm});
            skLineSegment(sketch, "E570", {"start": v(-25.93, -13.56) * mm, "end": v(-25.97, -13.56) * mm});
            skLineSegment(sketch, "E571", {"start": v(-25.97, -13.56) * mm, "end": v(-26.02, -13.56) * mm});
            skLineSegment(sketch, "E572", {"start": v(-26.02, -13.56) * mm, "end": v(-26.06, -13.56) * mm});
            skLineSegment(sketch, "E573", {"start": v(-26.06, -13.56) * mm, "end": v(-26.1, -13.56) * mm});
            skLineSegment(sketch, "E574", {"start": v(-26.1, -13.56) * mm, "end": v(-26.15, -13.56) * mm});
            skLineSegment(sketch, "E575", {"start": v(-26.15, -13.56) * mm, "end": v(-26.2, -13.55) * mm});
            skLineSegment(sketch, "E576", {"start": v(-26.2, -13.55) * mm, "end": v(-26.24, -13.54) * mm});
            skLineSegment(sketch, "E577", {"start": v(-26.24, -13.54) * mm, "end": v(-26.28, -13.53) * mm});
            skLineSegment(sketch, "E578", {"start": v(-26.28, -13.53) * mm, "end": v(-26.32, -13.52) * mm});
            skLineSegment(sketch, "E579", {"start": v(-26.32, -13.52) * mm, "end": v(-26.36, -13.5) * mm});
            skLineSegment(sketch, "E580", {"start": v(-26.36, -13.5) * mm, "end": v(-26.4, -13.48) * mm});
            skLineSegment(sketch, "E581", {"start": v(-26.4, -13.48) * mm, "end": v(-26.43, -13.45) * mm});
            skLineSegment(sketch, "E582", {"start": v(-26.43, -13.45) * mm, "end": v(-26.46, -13.43) * mm});
            skLineSegment(sketch, "E583", {"start": v(-26.46, -13.43) * mm, "end": v(-26.5, -13.4) * mm});
            skLineSegment(sketch, "E584", {"start": v(-26.5, -13.4) * mm, "end": v(-26.53, -13.36) * mm});
            skLineSegment(sketch, "E585", {"start": v(-26.53, -13.36) * mm, "end": v(-26.55, -13.31) * mm});
            skLineSegment(sketch, "E586", {"start": v(-26.55, -13.31) * mm, "end": v(-26.56, -13.27) * mm});
            skLineSegment(sketch, "E587", {"start": v(-26.56, -13.27) * mm, "end": v(-26.57, -13.22) * mm});
            skLineSegment(sketch, "E588", {"start": v(-26.57, -13.22) * mm, "end": v(-26.59, -13.18) * mm});
            skLineSegment(sketch, "E589", {"start": v(-26.59, -13.18) * mm, "end": v(-26.6, -13.13) * mm});
            skLineSegment(sketch, "E590", {"start": v(-26.6, -13.13) * mm, "end": v(-26.6, -13.08) * mm});
            skLineSegment(sketch, "E591", {"start": v(-26.6, -13.08) * mm, "end": v(-26.61, -13.04) * mm});
            skLineSegment(sketch, "E592", {"start": v(-26.61, -13.04) * mm, "end": v(-26.62, -12.99) * mm});
            skLineSegment(sketch, "E593", {"start": v(-26.62, -12.99) * mm, "end": v(-26.63, -12.94) * mm});
            skLineSegment(sketch, "E594", {"start": v(-26.63, -12.94) * mm, "end": v(-26.63, -12.9) * mm});
            skLineSegment(sketch, "E595", {"start": v(-26.63, -12.9) * mm, "end": v(-26.63, -12.85) * mm});
            skLineSegment(sketch, "E596", {"start": v(-26.63, -12.85) * mm, "end": v(-26.63, -12.8) * mm});
            skLineSegment(sketch, "E597", {"start": v(-26.63, -12.8) * mm, "end": v(-26.63, -12.75) * mm});
            skLineSegment(sketch, "E598", {"start": v(-26.63, -12.75) * mm, "end": v(-26.63, -12.7) * mm});
            skLineSegment(sketch, "E599", {"start": v(-26.63, -12.7) * mm, "end": v(-26.63, -12.66) * mm});
            skLineSegment(sketch, "E600", {"start": v(-26.63, -12.66) * mm, "end": v(-26.62, -12.6) * mm});
            skLineSegment(sketch, "E601", {"start": v(-26.62, -12.6) * mm, "end": v(-26.62, -12.56) * mm});
            skLineSegment(sketch, "E602", {"start": v(-26.62, -12.56) * mm, "end": v(-26.61, -12.51) * mm});
            skLineSegment(sketch, "E603", {"start": v(-26.61, -12.51) * mm, "end": v(-26.6, -12.47) * mm});
            skLineSegment(sketch, "E604", {"start": v(-26.6, -12.47) * mm, "end": v(-26.6, -12.42) * mm});
            skLineSegment(sketch, "E605", {"start": v(-26.6, -12.42) * mm, "end": v(-26.59, -12.37) * mm});
            skLineSegment(sketch, "E606", {"start": v(-26.59, -12.37) * mm, "end": v(-26.58, -12.33) * mm});
            skLineSegment(sketch, "E607", {"start": v(-26.58, -12.33) * mm, "end": v(-26.56, -12.28) * mm});
            skLineSegment(sketch, "E608", {"start": v(-26.56, -12.28) * mm, "end": v(-26.55, -12.23) * mm});
            skLineSegment(sketch, "E609", {"start": v(-26.55, -12.23) * mm, "end": v(-26.54, -12.19) * mm});
            skLineSegment(sketch, "E610", {"start": v(-26.54, -12.19) * mm, "end": v(-26.52, -12.14) * mm});
            skLineSegment(sketch, "E611", {"start": v(-26.52, -12.14) * mm, "end": v(-26.5, -12.1) * mm});
            skLineSegment(sketch, "E612", {"start": v(-26.5, -12.1) * mm, "end": v(-26.49, -12.05) * mm});
            skLineSegment(sketch, "E613", {"start": v(-26.49, -12.05) * mm, "end": v(-26.47, -12.01) * mm});
            skLineSegment(sketch, "E614", {"start": v(-7.73, -11.98) * mm, "end": v(-6.54, -12.01) * mm});
            skLineSegment(sketch, "E615", {"start": v(-6.54, -12.01) * mm, "end": v(-6.52, -12.06) * mm});
            skLineSegment(sketch, "E616", {"start": v(-6.52, -12.06) * mm, "end": v(-6.5, -12.1) * mm});
            skLineSegment(sketch, "E617", {"start": v(-6.5, -12.1) * mm, "end": v(-6.49, -12.16) * mm});
            skLineSegment(sketch, "E618", {"start": v(-6.49, -12.16) * mm, "end": v(-6.47, -12.2) * mm});
            skLineSegment(sketch, "E619", {"start": v(-6.47, -12.2) * mm, "end": v(-6.46, -12.26) * mm});
            skLineSegment(sketch, "E620", {"start": v(-6.46, -12.26) * mm, "end": v(-6.44, -12.31) * mm});
            skLineSegment(sketch, "E621", {"start": v(-6.44, -12.31) * mm, "end": v(-6.43, -12.37) * mm});
            skLineSegment(sketch, "E622", {"start": v(-6.43, -12.37) * mm, "end": v(-6.42, -12.42) * mm});
            skLineSegment(sketch, "E623", {"start": v(-6.42, -12.42) * mm, "end": v(-6.4, -12.48) * mm});
            skLineSegment(sketch, "E624", {"start": v(-6.4, -12.48) * mm, "end": v(-6.4, -12.53) * mm});
            skLineSegment(sketch, "E625", {"start": v(-6.4, -12.53) * mm, "end": v(-6.39, -12.59) * mm});
            skLineSegment(sketch, "E626", {"start": v(-6.39, -12.59) * mm, "end": v(-6.38, -12.64) * mm});
            skLineSegment(sketch, "E627", {"start": v(-6.38, -12.64) * mm, "end": v(-6.38, -12.7) * mm});
            skLineSegment(sketch, "E628", {"start": v(-6.38, -12.7) * mm, "end": v(-6.37, -12.75) * mm});
            skLineSegment(sketch, "E629", {"start": v(-6.37, -12.75) * mm, "end": v(-6.37, -12.8) * mm});
            skLineSegment(sketch, "E630", {"start": v(-6.37, -12.8) * mm, "end": v(-6.37, -12.86) * mm});
            skLineSegment(sketch, "E631", {"start": v(-6.37, -12.86) * mm, "end": v(-6.38, -12.91) * mm});
            skLineSegment(sketch, "E632", {"start": v(-6.38, -12.91) * mm, "end": v(-6.38, -12.97) * mm});
            skLineSegment(sketch, "E633", {"start": v(-6.38, -12.97) * mm, "end": v(-6.39, -13.02) * mm});
            skLineSegment(sketch, "E634", {"start": v(-6.39, -13.02) * mm, "end": v(-6.4, -13.07) * mm});
            skLineSegment(sketch, "E635", {"start": v(-6.4, -13.07) * mm, "end": v(-6.4, -13.12) * mm});
            skLineSegment(sketch, "E636", {"start": v(-6.4, -13.12) * mm, "end": v(-6.42, -13.17) * mm});
            skLineSegment(sketch, "E637", {"start": v(-6.42, -13.17) * mm, "end": v(-6.44, -13.22) * mm});
            skLineSegment(sketch, "E638", {"start": v(-6.44, -13.22) * mm, "end": v(-6.46, -13.27) * mm});
            skLineSegment(sketch, "E639", {"start": v(-6.46, -13.27) * mm, "end": v(-6.49, -13.32) * mm});
            skLineSegment(sketch, "E640", {"start": v(-6.49, -13.32) * mm, "end": v(-6.51, -13.36) * mm});
            skLineSegment(sketch, "E641", {"start": v(-6.51, -13.36) * mm, "end": v(-6.54, -13.4) * mm});
            skLineSegment(sketch, "E642", {"start": v(-6.54, -13.4) * mm, "end": v(-6.58, -13.45) * mm});
            skLineSegment(sketch, "E643", {"start": v(-6.58, -13.45) * mm, "end": v(-6.61, -13.49) * mm});
            skLineSegment(sketch, "E644", {"start": v(-6.61, -13.49) * mm, "end": v(-6.65, -13.5) * mm});
            skLineSegment(sketch, "E645", {"start": v(-6.65, -13.5) * mm, "end": v(-6.69, -13.5) * mm});
            skLineSegment(sketch, "E646", {"start": v(-6.69, -13.5) * mm, "end": v(-6.72, -13.52) * mm});
            skLineSegment(sketch, "E647", {"start": v(-6.72, -13.52) * mm, "end": v(-6.76, -13.52) * mm});
            skLineSegment(sketch, "E648", {"start": v(-6.76, -13.52) * mm, "end": v(-6.8, -13.53) * mm});
            skLineSegment(sketch, "E649", {"start": v(-6.8, -13.53) * mm, "end": v(-6.87, -13.54) * mm});
            skLineSegment(sketch, "E650", {"start": v(-6.87, -13.54) * mm, "end": v(-6.95, -13.55) * mm});
            skLineSegment(sketch, "E651", {"start": v(-6.95, -13.55) * mm, "end": v(-7.06, -13.55) * mm});
            skLineSegment(sketch, "E652", {"start": v(-7.06, -13.55) * mm, "end": v(-7.6, -13.53) * mm});
            skLineSegment(sketch, "E653", {"start": v(-7.6, -13.53) * mm, "end": v(-7.72, -13.53) * mm});
            skLineSegment(sketch, "E654", {"start": v(-7.72, -13.53) * mm, "end": v(-7.73, -11.98) * mm});
            skLineSegment(sketch, "E655", {"start": v(-20.77, -15.27) * mm, "end": v(-19.21, -15.27) * mm});
            skLineSegment(sketch, "E656", {"start": v(-19.21, -15.27) * mm, "end": v(-19.21, -16.13) * mm});
            skLineSegment(sketch, "E657", {"start": v(-19.21, -16.13) * mm, "end": v(-19.22, -16.27) * mm});
            skLineSegment(sketch, "E658", {"start": v(-19.22, -16.27) * mm, "end": v(-19.23, -16.29) * mm});
            skLineSegment(sketch, "E659", {"start": v(-19.23, -16.29) * mm, "end": v(-19.23, -16.3) * mm});
            skLineSegment(sketch, "E660", {"start": v(-19.23, -16.3) * mm, "end": v(-19.24, -16.32) * mm});
            skLineSegment(sketch, "E661", {"start": v(-19.24, -16.32) * mm, "end": v(-19.24, -16.34) * mm});
            skLineSegment(sketch, "E662", {"start": v(-19.24, -16.34) * mm, "end": v(-19.25, -16.35) * mm});
            skLineSegment(sketch, "E663", {"start": v(-19.25, -16.35) * mm, "end": v(-19.26, -16.37) * mm});
            skLineSegment(sketch, "E664", {"start": v(-19.26, -16.37) * mm, "end": v(-19.27, -16.38) * mm});
            skLineSegment(sketch, "E665", {"start": v(-19.27, -16.38) * mm, "end": v(-19.28, -16.4) * mm});
            skLineSegment(sketch, "E666", {"start": v(-19.28, -16.4) * mm, "end": v(-19.3, -16.41) * mm});
            skLineSegment(sketch, "E667", {"start": v(-19.3, -16.41) * mm, "end": v(-19.32, -16.43) * mm});
            skLineSegment(sketch, "E668", {"start": v(-19.32, -16.43) * mm, "end": v(-19.34, -16.46) * mm});
            skLineSegment(sketch, "E669", {"start": v(-19.34, -16.46) * mm, "end": v(-19.39, -16.49) * mm});
            skLineSegment(sketch, "E670", {"start": v(-19.39, -16.49) * mm, "end": v(-19.47, -16.53) * mm});
            skLineSegment(sketch, "E671", {"start": v(-19.47, -16.53) * mm, "end": v(-19.6, -16.58) * mm});
            skLineSegment(sketch, "E672", {"start": v(-19.6, -16.58) * mm, "end": v(-19.69, -16.6) * mm});
            skLineSegment(sketch, "E673", {"start": v(-19.69, -16.6) * mm, "end": v(-19.73, -16.6) * mm});
            skLineSegment(sketch, "E674", {"start": v(-19.73, -16.6) * mm, "end": v(-19.77, -16.6) * mm});
            skLineSegment(sketch, "E675", {"start": v(-19.77, -16.6) * mm, "end": v(-19.81, -16.61) * mm});
            skLineSegment(sketch, "E676", {"start": v(-19.81, -16.61) * mm, "end": v(-19.86, -16.62) * mm});
            skLineSegment(sketch, "E677", {"start": v(-19.86, -16.62) * mm, "end": v(-19.9, -16.62) * mm});
            skLineSegment(sketch, "E678", {"start": v(-19.9, -16.62) * mm, "end": v(-19.94, -16.62) * mm});
            skLineSegment(sketch, "E679", {"start": v(-19.94, -16.62) * mm, "end": v(-19.98, -16.62) * mm});
            skLineSegment(sketch, "E680", {"start": v(-19.98, -16.62) * mm, "end": v(-20.03, -16.62) * mm});
            skLineSegment(sketch, "E681", {"start": v(-20.03, -16.62) * mm, "end": v(-20.07, -16.62) * mm});
            skLineSegment(sketch, "E682", {"start": v(-20.07, -16.62) * mm, "end": v(-20.11, -16.62) * mm});
            skLineSegment(sketch, "E683", {"start": v(-20.11, -16.62) * mm, "end": v(-20.15, -16.62) * mm});
            skLineSegment(sketch, "E684", {"start": v(-20.15, -16.62) * mm, "end": v(-20.2, -16.61) * mm});
            skLineSegment(sketch, "E685", {"start": v(-20.2, -16.61) * mm, "end": v(-20.24, -16.6) * mm});
            skLineSegment(sketch, "E686", {"start": v(-20.24, -16.6) * mm, "end": v(-20.28, -16.6) * mm});
            skLineSegment(sketch, "E687", {"start": v(-20.28, -16.6) * mm, "end": v(-20.32, -16.6) * mm});
            skLineSegment(sketch, "E688", {"start": v(-20.32, -16.6) * mm, "end": v(-20.36, -16.58) * mm});
            skLineSegment(sketch, "E689", {"start": v(-20.36, -16.58) * mm, "end": v(-20.4, -16.57) * mm});
            skLineSegment(sketch, "E690", {"start": v(-20.4, -16.57) * mm, "end": v(-20.44, -16.56) * mm});
            skLineSegment(sketch, "E691", {"start": v(-20.44, -16.56) * mm, "end": v(-20.48, -16.54) * mm});
            skLineSegment(sketch, "E692", {"start": v(-20.48, -16.54) * mm, "end": v(-20.52, -16.53) * mm});
            skLineSegment(sketch, "E693", {"start": v(-20.52, -16.53) * mm, "end": v(-20.56, -16.51) * mm});
            skLineSegment(sketch, "E694", {"start": v(-20.56, -16.51) * mm, "end": v(-20.6, -16.5) * mm});
            skLineSegment(sketch, "E695", {"start": v(-20.6, -16.5) * mm, "end": v(-20.64, -16.47) * mm});
            skLineSegment(sketch, "E696", {"start": v(-20.64, -16.47) * mm, "end": v(-20.68, -16.45) * mm});
            skLineSegment(sketch, "E697", {"start": v(-20.68, -16.45) * mm, "end": v(-20.71, -16.43) * mm});
            skLineSegment(sketch, "E698", {"start": v(-20.71, -16.43) * mm, "end": v(-20.75, -16.4) * mm});
            skLineSegment(sketch, "E699", {"start": v(-20.75, -16.4) * mm, "end": v(-20.78, -16.38) * mm});
            skLineSegment(sketch, "E700", {"start": v(-20.78, -16.38) * mm, "end": v(-20.77, -15.27) * mm});
            skLineSegment(sketch, "E701", {"start": v(-18.48, -15.27) * mm, "end": v(-16.91, -15.27) * mm});
            skLineSegment(sketch, "E702", {"start": v(-16.91, -15.27) * mm, "end": v(-16.89, -16.15) * mm});
            skLineSegment(sketch, "E703", {"start": v(-16.89, -16.15) * mm, "end": v(-16.9, -16.21) * mm});
            skLineSegment(sketch, "E704", {"start": v(-16.9, -16.21) * mm, "end": v(-16.9, -16.27) * mm});
            skLineSegment(sketch, "E705", {"start": v(-16.9, -16.27) * mm, "end": v(-16.93, -16.32) * mm});
            skLineSegment(sketch, "E706", {"start": v(-16.93, -16.32) * mm, "end": v(-16.96, -16.37) * mm});
            skLineSegment(sketch, "E707", {"start": v(-16.96, -16.37) * mm, "end": v(-17, -16.42) * mm});
            skLineSegment(sketch, "E708", {"start": v(-17, -16.42) * mm, "end": v(-17.02, -16.45) * mm});
            skLineSegment(sketch, "E709", {"start": v(-17.02, -16.45) * mm, "end": v(-17.04, -16.47) * mm});
            skLineSegment(sketch, "E710", {"start": v(-17.04, -16.47) * mm, "end": v(-17.07, -16.5) * mm});
            skLineSegment(sketch, "E711", {"start": v(-17.07, -16.5) * mm, "end": v(-17.1, -16.52) * mm});
            skLineSegment(sketch, "E712", {"start": v(-17.1, -16.52) * mm, "end": v(-17.13, -16.54) * mm});
            skLineSegment(sketch, "E713", {"start": v(-17.13, -16.54) * mm, "end": v(-17.15, -16.55) * mm});
            skLineSegment(sketch, "E714", {"start": v(-17.15, -16.55) * mm, "end": v(-17.17, -16.56) * mm});
            skLineSegment(sketch, "E715", {"start": v(-17.17, -16.56) * mm, "end": v(-17.19, -16.56) * mm});
            skLineSegment(sketch, "E716", {"start": v(-17.19, -16.56) * mm, "end": v(-17.2, -16.57) * mm});
            skLineSegment(sketch, "E717", {"start": v(-17.2, -16.57) * mm, "end": v(-17.22, -16.57) * mm});
            skLineSegment(sketch, "E718", {"start": v(-17.22, -16.57) * mm, "end": v(-17.24, -16.57) * mm});
            skLineSegment(sketch, "E719", {"start": v(-17.24, -16.57) * mm, "end": v(-17.26, -16.58) * mm});
            skLineSegment(sketch, "E720", {"start": v(-17.26, -16.58) * mm, "end": v(-17.3, -16.58) * mm});
            skLineSegment(sketch, "E721", {"start": v(-17.3, -16.58) * mm, "end": v(-17.39, -16.6) * mm});
            skLineSegment(sketch, "E722", {"start": v(-17.39, -16.6) * mm, "end": v(-17.47, -16.61) * mm});
            skLineSegment(sketch, "E723", {"start": v(-17.47, -16.61) * mm, "end": v(-17.56, -16.62) * mm});
            skLineSegment(sketch, "E724", {"start": v(-17.56, -16.62) * mm, "end": v(-17.6, -16.62) * mm});
            skLineSegment(sketch, "E725", {"start": v(-17.6, -16.62) * mm, "end": v(-17.65, -16.63) * mm});
            skLineSegment(sketch, "E726", {"start": v(-17.65, -16.63) * mm, "end": v(-17.7, -16.63) * mm});
            skLineSegment(sketch, "E727", {"start": v(-17.7, -16.63) * mm, "end": v(-17.74, -16.63) * mm});
            skLineSegment(sketch, "E728", {"start": v(-17.74, -16.63) * mm, "end": v(-17.79, -16.63) * mm});
            skLineSegment(sketch, "E729", {"start": v(-17.79, -16.63) * mm, "end": v(-17.83, -16.62) * mm});
            skLineSegment(sketch, "E730", {"start": v(-17.83, -16.62) * mm, "end": v(-17.88, -16.62) * mm});
            skLineSegment(sketch, "E731", {"start": v(-17.88, -16.62) * mm, "end": v(-17.92, -16.61) * mm});
            skLineSegment(sketch, "E732", {"start": v(-17.92, -16.61) * mm, "end": v(-17.96, -16.6) * mm});
            skLineSegment(sketch, "E733", {"start": v(-17.96, -16.6) * mm, "end": v(-18, -16.6) * mm});
            skLineSegment(sketch, "E734", {"start": v(-18, -16.6) * mm, "end": v(-18.05, -16.59) * mm});
            skLineSegment(sketch, "E735", {"start": v(-18.05, -16.59) * mm, "end": v(-18.1, -16.57) * mm});
            skLineSegment(sketch, "E736", {"start": v(-18.1, -16.57) * mm, "end": v(-18.13, -16.56) * mm});
            skLineSegment(sketch, "E737", {"start": v(-18.13, -16.56) * mm, "end": v(-18.17, -16.54) * mm});
            skLineSegment(sketch, "E738", {"start": v(-18.17, -16.54) * mm, "end": v(-18.2, -16.52) * mm});
            skLineSegment(sketch, "E739", {"start": v(-18.2, -16.52) * mm, "end": v(-18.25, -16.5) * mm});
            skLineSegment(sketch, "E740", {"start": v(-18.25, -16.5) * mm, "end": v(-18.28, -16.48) * mm});
            skLineSegment(sketch, "E741", {"start": v(-18.28, -16.48) * mm, "end": v(-18.32, -16.45) * mm});
            skLineSegment(sketch, "E742", {"start": v(-18.32, -16.45) * mm, "end": v(-18.35, -16.42) * mm});
            skLineSegment(sketch, "E743", {"start": v(-18.35, -16.42) * mm, "end": v(-18.38, -16.39) * mm});
            skLineSegment(sketch, "E744", {"start": v(-18.38, -16.39) * mm, "end": v(-18.4, -16.35) * mm});
            skLineSegment(sketch, "E745", {"start": v(-18.4, -16.35) * mm, "end": v(-18.44, -16.32) * mm});
            skLineSegment(sketch, "E746", {"start": v(-18.44, -16.32) * mm, "end": v(-18.45, -16.25) * mm});
            skLineSegment(sketch, "E747", {"start": v(-18.45, -16.25) * mm, "end": v(-18.46, -16.14) * mm});
            skLineSegment(sketch, "E748", {"start": v(-18.46, -16.14) * mm, "end": v(-18.48, -15.96) * mm});
            skLineSegment(sketch, "E749", {"start": v(-18.48, -15.96) * mm, "end": v(-18.48, -15.27) * mm});
            skLineSegment(sketch, "E750", {"start": v(-16.1, -15.27) * mm, "end": v(-14.53, -15.27) * mm});
            skLineSegment(sketch, "E751", {"start": v(-14.53, -15.27) * mm, "end": v(-14.53, -15.99) * mm});
            skLineSegment(sketch, "E752", {"start": v(-14.53, -15.99) * mm, "end": v(-14.54, -16.16) * mm});
            skLineSegment(sketch, "E753", {"start": v(-14.54, -16.16) * mm, "end": v(-14.55, -16.26) * mm});
            skLineSegment(sketch, "E754", {"start": v(-14.55, -16.26) * mm, "end": v(-14.57, -16.3) * mm});
            skLineSegment(sketch, "E755", {"start": v(-14.57, -16.3) * mm, "end": v(-14.59, -16.33) * mm});
            skLineSegment(sketch, "E756", {"start": v(-14.59, -16.33) * mm, "end": v(-14.6, -16.36) * mm});
            skLineSegment(sketch, "E757", {"start": v(-14.6, -16.36) * mm, "end": v(-14.63, -16.38) * mm});
            skLineSegment(sketch, "E758", {"start": v(-14.63, -16.38) * mm, "end": v(-14.65, -16.41) * mm});
            skLineSegment(sketch, "E759", {"start": v(-14.65, -16.41) * mm, "end": v(-14.67, -16.44) * mm});
            skLineSegment(sketch, "E760", {"start": v(-14.67, -16.44) * mm, "end": v(-14.7, -16.46) * mm});
            skLineSegment(sketch, "E761", {"start": v(-14.7, -16.46) * mm, "end": v(-14.73, -16.48) * mm});
            skLineSegment(sketch, "E762", {"start": v(-14.73, -16.48) * mm, "end": v(-14.76, -16.5) * mm});
            skLineSegment(sketch, "E763", {"start": v(-14.76, -16.5) * mm, "end": v(-14.78, -16.52) * mm});
            skLineSegment(sketch, "E764", {"start": v(-14.78, -16.52) * mm, "end": v(-14.82, -16.53) * mm});
            skLineSegment(sketch, "E765", {"start": v(-14.82, -16.53) * mm, "end": v(-14.85, -16.55) * mm});
            skLineSegment(sketch, "E766", {"start": v(-14.85, -16.55) * mm, "end": v(-14.88, -16.56) * mm});
            skLineSegment(sketch, "E767", {"start": v(-14.88, -16.56) * mm, "end": v(-14.91, -16.57) * mm});
            skLineSegment(sketch, "E768", {"start": v(-14.91, -16.57) * mm, "end": v(-14.95, -16.58) * mm});
            skLineSegment(sketch, "E769", {"start": v(-14.95, -16.58) * mm, "end": v(-14.98, -16.59) * mm});
            skLineSegment(sketch, "E770", {"start": v(-14.98, -16.59) * mm, "end": v(-15.02, -16.6) * mm});
            skLineSegment(sketch, "E771", {"start": v(-15.02, -16.6) * mm, "end": v(-15.05, -16.6) * mm});
            skLineSegment(sketch, "E772", {"start": v(-15.05, -16.6) * mm, "end": v(-15.1, -16.6) * mm});
            skLineSegment(sketch, "E773", {"start": v(-15.1, -16.6) * mm, "end": v(-15.16, -16.61) * mm});
            skLineSegment(sketch, "E774", {"start": v(-15.16, -16.61) * mm, "end": v(-15.24, -16.62) * mm});
            skLineSegment(sketch, "E775", {"start": v(-15.24, -16.62) * mm, "end": v(-15.3, -16.62) * mm});
            skLineSegment(sketch, "E776", {"start": v(-15.3, -16.62) * mm, "end": v(-15.38, -16.62) * mm});
            skLineSegment(sketch, "E777", {"start": v(-15.38, -16.62) * mm, "end": v(-15.44, -16.61) * mm});
            skLineSegment(sketch, "E778", {"start": v(-15.44, -16.61) * mm, "end": v(-15.5, -16.62) * mm});
            skLineSegment(sketch, "E779", {"start": v(-15.5, -16.62) * mm, "end": v(-15.55, -16.61) * mm});
            skLineSegment(sketch, "E780", {"start": v(-15.55, -16.61) * mm, "end": v(-15.6, -16.6) * mm});
            skLineSegment(sketch, "E781", {"start": v(-15.6, -16.6) * mm, "end": v(-15.66, -16.6) * mm});
            skLineSegment(sketch, "E782", {"start": v(-15.66, -16.6) * mm, "end": v(-15.71, -16.59) * mm});
            skLineSegment(sketch, "E783", {"start": v(-15.71, -16.59) * mm, "end": v(-15.74, -16.58) * mm});
            skLineSegment(sketch, "E784", {"start": v(-15.74, -16.58) * mm, "end": v(-15.77, -16.57) * mm});
            skLineSegment(sketch, "E785", {"start": v(-15.77, -16.57) * mm, "end": v(-15.8, -16.56) * mm});
            skLineSegment(sketch, "E786", {"start": v(-15.8, -16.56) * mm, "end": v(-15.82, -16.55) * mm});
            skLineSegment(sketch, "E787", {"start": v(-15.82, -16.55) * mm, "end": v(-15.84, -16.54) * mm});
            skLineSegment(sketch, "E788", {"start": v(-15.84, -16.54) * mm, "end": v(-15.87, -16.53) * mm});
            skLineSegment(sketch, "E789", {"start": v(-15.87, -16.53) * mm, "end": v(-15.9, -16.52) * mm});
            skLineSegment(sketch, "E790", {"start": v(-15.9, -16.52) * mm, "end": v(-15.92, -16.5) * mm});
            skLineSegment(sketch, "E791", {"start": v(-15.92, -16.5) * mm, "end": v(-15.94, -16.49) * mm});
            skLineSegment(sketch, "E792", {"start": v(-15.94, -16.49) * mm, "end": v(-15.96, -16.47) * mm});
            skLineSegment(sketch, "E793", {"start": v(-15.96, -16.47) * mm, "end": v(-15.98, -16.46) * mm});
            skLineSegment(sketch, "E794", {"start": v(-15.98, -16.46) * mm, "end": v(-16, -16.44) * mm});
            skLineSegment(sketch, "E795", {"start": v(-16, -16.44) * mm, "end": v(-16.02, -16.42) * mm});
            skLineSegment(sketch, "E796", {"start": v(-16.02, -16.42) * mm, "end": v(-16.04, -16.4) * mm});
            skLineSegment(sketch, "E797", {"start": v(-16.04, -16.4) * mm, "end": v(-16.05, -16.38) * mm});
            skLineSegment(sketch, "E798", {"start": v(-16.05, -16.38) * mm, "end": v(-16.07, -16.35) * mm});
            skLineSegment(sketch, "E799", {"start": v(-16.07, -16.35) * mm, "end": v(-16.08, -16.33) * mm});
            skLineSegment(sketch, "E800", {"start": v(-16.08, -16.33) * mm, "end": v(-16.1, -16.3) * mm});
            skLineSegment(sketch, "E801", {"start": v(-16.1, -16.3) * mm, "end": v(-16.1, -16.28) * mm});
            skLineSegment(sketch, "E802", {"start": v(-16.1, -16.28) * mm, "end": v(-16.12, -16.18) * mm});
            skLineSegment(sketch, "E803", {"start": v(-16.12, -16.18) * mm, "end": v(-16.13, -16.04) * mm});
            skLineSegment(sketch, "E804", {"start": v(-16.13, -16.04) * mm, "end": v(-16.13, -15.76) * mm});
            skLineSegment(sketch, "E805", {"start": v(-16.13, -15.76) * mm, "end": v(-16.1, -15.27) * mm});
            skLineSegment(sketch, "E806", {"start": v(-13.8, -15.27) * mm, "end": v(-12.24, -15.27) * mm});
            skLineSegment(sketch, "E807", {"start": v(-12.24, -15.27) * mm, "end": v(-12.23, -16.38) * mm});
            skLineSegment(sketch, "E808", {"start": v(-12.23, -16.38) * mm, "end": v(-12.27, -16.4) * mm});
            skLineSegment(sketch, "E809", {"start": v(-12.27, -16.4) * mm, "end": v(-12.3, -16.43) * mm});
            skLineSegment(sketch, "E810", {"start": v(-12.3, -16.43) * mm, "end": v(-12.34, -16.45) * mm});
            skLineSegment(sketch, "E811", {"start": v(-12.34, -16.45) * mm, "end": v(-12.38, -16.48) * mm});
            skLineSegment(sketch, "E812", {"start": v(-12.38, -16.48) * mm, "end": v(-12.42, -16.5) * mm});
            skLineSegment(sketch, "E813", {"start": v(-12.42, -16.5) * mm, "end": v(-12.46, -16.51) * mm});
            skLineSegment(sketch, "E814", {"start": v(-12.46, -16.51) * mm, "end": v(-12.5, -16.53) * mm});
            skLineSegment(sketch, "E815", {"start": v(-12.5, -16.53) * mm, "end": v(-12.54, -16.55) * mm});
            skLineSegment(sketch, "E816", {"start": v(-12.54, -16.55) * mm, "end": v(-12.58, -16.56) * mm});
            skLineSegment(sketch, "E817", {"start": v(-12.58, -16.56) * mm, "end": v(-12.62, -16.57) * mm});
            skLineSegment(sketch, "E818", {"start": v(-12.62, -16.57) * mm, "end": v(-12.66, -16.58) * mm});
            skLineSegment(sketch, "E819", {"start": v(-12.66, -16.58) * mm, "end": v(-12.7, -16.6) * mm});
            skLineSegment(sketch, "E820", {"start": v(-12.7, -16.6) * mm, "end": v(-12.75, -16.6) * mm});
            skLineSegment(sketch, "E821", {"start": v(-12.75, -16.6) * mm, "end": v(-12.8, -16.6) * mm});
            skLineSegment(sketch, "E822", {"start": v(-12.8, -16.6) * mm, "end": v(-12.84, -16.61) * mm});
            skLineSegment(sketch, "E823", {"start": v(-12.84, -16.61) * mm, "end": v(-12.88, -16.62) * mm});
            skLineSegment(sketch, "E824", {"start": v(-12.88, -16.62) * mm, "end": v(-12.92, -16.62) * mm});
            skLineSegment(sketch, "E825", {"start": v(-12.92, -16.62) * mm, "end": v(-12.97, -16.62) * mm});
            skLineSegment(sketch, "E826", {"start": v(-12.97, -16.62) * mm, "end": v(-13.01, -16.62) * mm});
            skLineSegment(sketch, "E827", {"start": v(-13.01, -16.62) * mm, "end": v(-13.05, -16.62) * mm});
            skLineSegment(sketch, "E828", {"start": v(-13.05, -16.62) * mm, "end": v(-13.1, -16.62) * mm});
            skLineSegment(sketch, "E829", {"start": v(-13.1, -16.62) * mm, "end": v(-13.14, -16.62) * mm});
            skLineSegment(sketch, "E830", {"start": v(-13.14, -16.62) * mm, "end": v(-13.19, -16.61) * mm});
            skLineSegment(sketch, "E831", {"start": v(-13.19, -16.61) * mm, "end": v(-13.23, -16.6) * mm});
            skLineSegment(sketch, "E832", {"start": v(-13.23, -16.6) * mm, "end": v(-13.27, -16.6) * mm});
            skLineSegment(sketch, "E833", {"start": v(-13.27, -16.6) * mm, "end": v(-13.32, -16.6) * mm});
            skLineSegment(sketch, "E834", {"start": v(-13.32, -16.6) * mm, "end": v(-13.36, -16.59) * mm});
            skLineSegment(sketch, "E835", {"start": v(-13.36, -16.59) * mm, "end": v(-13.4, -16.58) * mm});
            skLineSegment(sketch, "E836", {"start": v(-13.4, -16.58) * mm, "end": v(-13.44, -16.57) * mm});
            skLineSegment(sketch, "E837", {"start": v(-13.44, -16.57) * mm, "end": v(-13.63, -16.48) * mm});
            skLineSegment(sketch, "E838", {"start": v(-13.63, -16.48) * mm, "end": v(-13.67, -16.46) * mm});
            skLineSegment(sketch, "E839", {"start": v(-13.67, -16.46) * mm, "end": v(-13.7, -16.44) * mm});
            skLineSegment(sketch, "E840", {"start": v(-13.7, -16.44) * mm, "end": v(-13.72, -16.42) * mm});
            skLineSegment(sketch, "E841", {"start": v(-13.72, -16.42) * mm, "end": v(-13.74, -16.4) * mm});
            skLineSegment(sketch, "E842", {"start": v(-13.74, -16.4) * mm, "end": v(-13.74, -16.39) * mm});
            skLineSegment(sketch, "E843", {"start": v(-13.74, -16.39) * mm, "end": v(-13.75, -16.37) * mm});
            skLineSegment(sketch, "E844", {"start": v(-13.75, -16.37) * mm, "end": v(-13.76, -16.36) * mm});
            skLineSegment(sketch, "E845", {"start": v(-13.76, -16.36) * mm, "end": v(-13.76, -16.34) * mm});
            skLineSegment(sketch, "E846", {"start": v(-13.76, -16.34) * mm, "end": v(-13.77, -16.33) * mm});
            skLineSegment(sketch, "E847", {"start": v(-13.77, -16.33) * mm, "end": v(-13.77, -16.31) * mm});
            skLineSegment(sketch, "E848", {"start": v(-13.77, -16.31) * mm, "end": v(-13.78, -16.3) * mm});
            skLineSegment(sketch, "E849", {"start": v(-13.78, -16.3) * mm, "end": v(-13.8, -15.27) * mm});
            skFitSpline(sketch, "E850", {"points": [v(-16.09, 0.4) * mm, v(-16.48, 0.53) * mm, v(-16.87, 0.42) * mm], "startDerivative": vector(-0.77, 0.4) * mm, "endDerivative": vector(-0.8, -0.36) * mm});
            skFitSpline(sketch, "E851", {"points": [v(-9.68, -1.66) * mm, v(-8.41, -1.95) * mm, v(-8.04, -3.41) * mm], "startDerivative": vector(3.1, -0.07) * mm, "endDerivative": vector(0.22, -3.4) * mm});
            skLineSegment(sketch, "E852", {"start": v(-8.04, -3.41) * mm, "end": v(-8.04, -3.57) * mm});
            skLineSegment(sketch, "E853", {"start": v(-16.09, 0.4) * mm, "end": v(-15.75, 0.24) * mm});
            skLineSegment(sketch, "E854", {"start": v(-17.01, 0.36) * mm, "end": v(-16.87, 0.42) * mm});
            skLineSegment(sketch, "E855", {"start": v(-9.68, -1.66) * mm, "end": v(-9.7, 0.57) * mm});
            skLineSegment(sketch, "E856", {"start": v(-13.9, -1.75) * mm, "end": v(-16.26, -0.55) * mm});
            skFitSpline(sketch, "E857", {"points": [v(-16.26, -0.55) * mm, v(-16.5, -0.47) * mm, v(-16.83, -0.6) * mm], "startDerivative": vector(-0.52, 0.27) * mm, "endDerivative": vector(-0.63, -0.37) * mm});
            skFitSpline(sketch, "E858", {"points": [v(-9.4, -3.99) * mm, v(-9.18, -4.2) * mm, v(-9.85, -4.84) * mm], "startDerivative": vector(0.88, -0.52) * mm, "endDerivative": vector(-1.57, -1.12) * mm});
            skSolve(sketch);
        }
        {
            var Q0;
            Q0=qSketchRegion(id+"F27",true);
            extrude(context, id + "F28", {"entities" : qUnion([Q0]), "operationType" : NewBodyOperationType.ADD, "depth" : 26.5 * mm});
        }
        {
            var Q0;
            Q0=qSketchRegion(id+"F27",true);
            var Q1;
            {var subQ0=sQuery(id+"F0.wireOp",EDGE,"E7.rect.top");var subQ1=sQuery(id+"F0.wireOp",EDGE,"E7.rect.right");var subQ2=sQuery(id+"F0.wireOp",EDGE,"E7.rect.left");var subQ3=sQuery(id+"F0.wireOp",EDGE,"E7.rect.bottom");var subQ4=sQuery(id+"F0.wireOp",EDGE,"E5.MirrorC");var subQ5=sQuery(id+"F0.wireOp",EDGE,"E3");var subQ6=sQuery(id+"F0.wireOp",EDGE,"E2");var subQ7=sQuery(id+"F0.wireOp",EDGE,"E1");Q1=makeQuery(id+"F28.boolean.opBoolean","SPLIT",FACE,{"disambiguationData":[TD([makeQuery(id+"F28.opExtrude","SWEPT_FACE",FACE,{"disambiguationData":[OSD([sQuery(id+"F27.wireOp",EDGE,"E123")])]})])],"derivedFrom":makeQuery(id+"F6.opShell","OFFSET_FACE",FACE,{"disambiguationData":[OSD([subQ7,subQ6,subQ5,subQ4,subQ3,subQ0,subQ2,subQ1]),TDD([makeQuery(id+"F1.opExtrude","CAP_FACE",FACE,{"disambiguationData":[OSD([subQ7,subQ6,subQ5,subQ4,subQ3,subQ0,subQ2,subQ1])],"isStart":false})])]})});}
            extrude(context, id + "F29", {"entities" : qUnion([Q0]), "operationType" : NewBodyOperationType.REMOVE, "endBound" : BoundingType.UP_TO_SURFACE, "endBoundEntityFace" : qUnion([Q1]), "depth" : 23 * mm});
        }
        {
            var Q0;
            {var subQ0=sQuery(id+"F18.wireOp",EDGE,"E66");Q0=makeQuery(id+"F18.imprint","IMPRINT",FACE,{"disambiguationData":[TD([[makeQuery(id+"F18.imprint","IMPRINT",EDGE,{"derivedFrom":subQ0}),-1.0]])]});}
            extrude(context, id + "F30", {"entities" : qUnion([Q0]), "operationType" : NewBodyOperationType.REMOVE, "oppositeDirection" : true, "depth" : 2 * mm});
        }
        {
            var Q0;
            Q0=qCreatedBy(makeId("Top.planeOp"),FACE);
            var sketch = newSketch(context, id + "F31", { "sketchPlane" : qUnion([Q0])});
            skLineSegment(sketch, "E859.bottom", {"start": v(7.48, -5.58) * mm, "end": v(13.97, -5.58) * mm});
            skLineSegment(sketch, "E859.top", {"start": v(7.48, -5.2) * mm, "end": v(13.97, -5.2) * mm});
            skLineSegment(sketch, "E860.bottom", {"start": v(6.04, -5.58) * mm, "end": v(16.8, -5.58) * mm});
            skLineSegment(sketch, "E860.top", {"start": v(6.04, -5.2) * mm, "end": v(16.8, -5.2) * mm});
            skLineSegment(sketch, "E860.left", {"start": v(6.04, -5.58) * mm, "end": v(6.04, -5.2) * mm});
            skLineSegment(sketch, "E861", {"start": v(16.8, -5.2) * mm, "end": v(18.32, -5.2) * mm});
            skLineSegment(sketch, "E862", {"start": v(18.32, -5.2) * mm, "end": v(18.32, -5.58) * mm});
            skLineSegment(sketch, "E863", {"start": v(18.32, -5.58) * mm, "end": v(16.8, -5.58) * mm});
            skSolve(sketch);
        }
        {
            var Q0;
            Q0=qSketchRegion(id+"F31",true);
            var Q1;
            {var subQ1=sQuery(id+"F2.wireOp",EDGE,"E22");var subQ3=sQuery(id+"F2.wireOp",EDGE,"E20");Q1=makeQuery(id+"F24.boolean.opBoolean","SPLIT",FACE,{"disambiguationData":[TD([makeQuery(id+"F6.opShell","OFFSET_FACE",FACE,{"disambiguationData":[OSD([sQuery(id+"F0.wireOp",EDGE,"E3")])]})])],"derivedFrom":makeQuery(id+"F6.opShell","OFFSET_FACE",FACE,{"disambiguationData":[OSD([subQ3,subQ1])]})});}
            extrude(context, id + "F32", {"entities" : qUnion([Q0]), "operationType" : NewBodyOperationType.ADD, "endBound" : BoundingType.UP_TO_SURFACE, "endBoundEntityFace" : qUnion([Q1]), "depth" : 25 * mm});
        }
        {
            var Q0;
            {var subQ0=sQuery(id+"F0.wireOp",EDGE,"E7.rect.top");var subQ1=sQuery(id+"F0.wireOp",EDGE,"E7.rect.right");var subQ2=sQuery(id+"F0.wireOp",EDGE,"E7.rect.left");var subQ3=sQuery(id+"F0.wireOp",EDGE,"E7.rect.bottom");var subQ4=sQuery(id+"F0.wireOp",EDGE,"E5.MirrorC");var subQ5=sQuery(id+"F0.wireOp",EDGE,"E3");var subQ6=sQuery(id+"F0.wireOp",EDGE,"E2");var subQ7=sQuery(id+"F0.wireOp",EDGE,"E1");Q0=makeQuery(id+"F28.boolean.opBoolean","SPLIT",FACE,{"disambiguationData":[TD([makeQuery(id+"F4.opFillet","BLEND_FACE",FACE,{"disambiguationData":[OSD([subQ0])]})])],"derivedFrom":makeQuery(id+"F1.opExtrude","CAP_FACE",FACE,{"disambiguationData":[OSD([subQ7,subQ6,subQ5,subQ4,subQ3,subQ0,subQ2,subQ1])],"isStart":false})});}
            cPlane(context, id + "F33", {"entities" : qUnion([Q0]), "cplaneType" : CPlaneType.OFFSET, "offset" : 9 * mm, "oppositeDirection" : true, "width" : 150 * mm, "height" : 150 * mm});
        }
        {
            var Q0;
            Q0=qCreatedBy(id+"F33.planeOp",FACE);
            var sketch = newSketch(context, id + "F34", { "sketchPlane" : qUnion([Q0])});
            skCircle(sketch, "E864", {"center": v(-29.86, -30.9) * mm, "radius": 1.22 * mm});
            skCircle(sketch, "E865", {"center": v(-29.84, 14.65) * mm, "radius": 1.25 * mm});
            skSolve(sketch);
        }
        {
            var Q0;
            Q0=qSketchRegion(id+"F34",true);
            var Q1;
            Q1=makeQuery(id+"F3.boolean.opBoolean","COPY",FACE,{"derivedFrom":makeQuery(id+"F3.opExtrude","SWEPT_FACE",FACE,{"disambiguationData":[OSD([sQuery(id+"F2.wireOp",EDGE,"E14")])]})});
            extrude(context, id + "F35", {"entities" : qUnion([Q0]), "operationType" : NewBodyOperationType.ADD, "endBound" : BoundingType.UP_TO_SURFACE, "endBoundEntityFace" : qUnion([Q1]), "depth" : 25 * mm});
        }
        {
            var Q0;
            {var subQ0=sQuery(id+"F0.wireOp",EDGE,"E7.rect.right");var subQ1=sQuery(id+"F0.wireOp",EDGE,"E7.rect.left");var subQ2=sQuery(id+"F0.wireOp",EDGE,"E7.rect.top");var subQ3=sQuery(id+"F0.wireOp",EDGE,"E7.rect.bottom");var subQ4=sQuery(id+"F0.wireOp",EDGE,"E5.MirrorC");var subQ5=sQuery(id+"F0.wireOp",EDGE,"E3");var subQ6=sQuery(id+"F0.wireOp",EDGE,"E2");var subQ7=sQuery(id+"F0.wireOp",EDGE,"E1");Q0=makeQuery(id+"F28.boolean.opBoolean","SPLIT",FACE,{"disambiguationData":[TD([makeQuery(id+"F4.opFillet","BLEND_FACE",FACE,{"disambiguationData":[OSD([subQ3])]})])],"derivedFrom":makeQuery(id+"F1.opExtrude","CAP_FACE",FACE,{"disambiguationData":[OSD([subQ7,subQ6,subQ5,subQ4,subQ3,subQ2,subQ1,subQ0])],"isStart":false})});}
            cPlane(context, id + "F36", {"entities" : qUnion([Q0]), "cplaneType" : CPlaneType.OFFSET, "offset" : 17.5 * mm, "oppositeDirection" : true, "width" : 150 * mm, "height" : 150 * mm});
        }
        {
            var Q0;
            Q0=qCreatedBy(id+"F36.planeOp",FACE);
            var sketch = newSketch(context, id + "F37", { "sketchPlane" : qUnion([Q0])});
            skCircle(sketch, "E866", {"center": v(8.9, 3.98) * mm, "radius": 1.26 * mm});
            skCircle(sketch, "E867", {"center": v(15.8, -30.92) * mm, "radius": 1.17 * mm});
            skSolve(sketch);
        }
        {
            var Q0;
            Q0=qSketchRegion(id+"F37",true);
            var Q1;
            {var subQ0=sQuery(id+"F2.wireOp",EDGE,"E22");var subQ1=sQuery(id+"F2.wireOp",EDGE,"E20");Q1=makeQuery(id+"F24.boolean.opBoolean","SPLIT",FACE,{"disambiguationData":[TD([makeQuery(id+"F1.opExtrude","SWEPT_FACE",FACE,{"disambiguationData":[OSD([sQuery(id+"F0.wireOp",EDGE,"E3")])]})])],"derivedFrom":makeQuery(id+"F3.boolean.opBoolean","COPY",FACE,{"derivedFrom":makeQuery(id+"F3.opExtrude","SWEPT_FACE",FACE,{"disambiguationData":[OSD([subQ1,subQ0])]})})});}
            extrude(context, id + "F38", {"entities" : qUnion([Q0]), "operationType" : NewBodyOperationType.ADD, "endBound" : BoundingType.UP_TO_SURFACE, "endBoundEntityFace" : qUnion([Q1]), "depth" : 25 * mm});
        }
        {
            var Q0;
            Q0=makeQuery(id+"F1.opExtrude","SWEPT_FACE",FACE,{"disambiguationData":[OSD([sQuery(id+"F0.wireOp",EDGE,"E7.rect.bottom")])]});
            cPlane(context, id + "F39", {"entities" : qUnion([Q0]), "cplaneType" : CPlaneType.OFFSET, "offset" : 1.8 * mm, "oppositeDirection" : true, "width" : 150 * mm, "height" : 150 * mm});
        }
        {
            var Q0;
            Q0=qCreatedBy(id+"F39.planeOp",FACE);
            var sketch = newSketch(context, id + "F40", { "sketchPlane" : qUnion([Q0])});
            skLineSegment(sketch, "E868.top", {"start": v(-5.27, 0) * mm, "end": v(12.86, 0) * mm});
            skLineSegment(sketch, "E869.right", {"start": v(12.86, 5.48) * mm, "end": v(12.86, 0) * mm});
            skLineSegment(sketch, "E870.bottom", {"start": v(12.86, 0) * mm, "end": v(-5.27, 0) * mm});
            skLineSegment(sketch, "E870.top", {"start": v(12.86, 5.48) * mm, "end": v(-5.27, 5.48) * mm});
            skLineSegment(sketch, "E870.left", {"start": v(12.86, 0) * mm, "end": v(12.86, 5.48) * mm});
            skPoint(sketch, "E871.orphan", {"position": v(14.06, 0) * mm});
            skLineSegment(sketch, "E872", {"start": v(-5.27, 5.48) * mm, "end": v(-8, 5.48) * mm});
            skLineSegment(sketch, "E873", {"start": v(-8, 5.48) * mm, "end": v(-8, 0) * mm});
            skLineSegment(sketch, "E874", {"start": v(-8, 0) * mm, "end": v(-5.27, 0) * mm});
            skSolve(sketch);
        }
        {
            var Q0;
            Q0 = qSketchRegion(id + "F40", true);
            extrude(context, id + "F41", {"entities" : qUnion([Q0]), "operationType" : NewBodyOperationType.REMOVE, "depth" : 1.2 * mm});
        }
        {
            var Q0;
            Q0=qCreatedBy(makeId("Top.planeOp"),FACE);
            var sketch = newSketch(context, id + "F42", { "sketchPlane" : qUnion([Q0])});
            skLineSegment(sketch, "E875.bottom", {"start": v(-10.2, -20.34) * mm, "end": v(-23.5, -20.34) * mm});
            skLineSegment(sketch, "E875.top", {"start": v(-9.76, -20.7) * mm, "end": v(-23.91, -20.7) * mm});
            skLineSegment(sketch, "E875.left", {"start": v(-9.76, -20.34) * mm, "end": v(-9.76, -20.7) * mm});
            skLineSegment(sketch, "E876", {"start": v(-9.76, -19.58) * mm, "end": v(-9.76, 2.28) * mm});
            skLineSegment(sketch, "E877.bottom", {"start": v(-10.2, 2.28) * mm, "end": v(-23.5, 2.28) * mm});
            skLineSegment(sketch, "E877.top", {"start": v(-9.76, 2.58) * mm, "end": v(-23.91, 2.58) * mm});
            skLineSegment(sketch, "E877.left", {"start": v(-9.76, 2.28) * mm, "end": v(-9.76, 2.58) * mm});
            skLineSegment(sketch, "E877.right", {"start": v(-23.91, 2.28) * mm, "end": v(-23.91, 2.58) * mm});
            skLineSegment(sketch, "E878.bottom", {"start": v(-10.2, -10.06) * mm, "end": v(-23.5, -10.06) * mm});
            skLineSegment(sketch, "E878.top", {"start": v(-10.2, -9.35) * mm, "end": v(-23.5, -9.35) * mm});
            skLineSegment(sketch, "E878.left", {"start": v(-9.76, -10.06) * mm, "end": v(-9.76, -9.35) * mm});
            skLineSegment(sketch, "E878.right", {"start": v(-25.9, -10.06) * mm, "end": v(-25.9, -9.35) * mm});
            skLineSegment(sketch, "E879", {"start": v(-10.2, -19.58) * mm, "end": v(-10.2, -10.06) * mm});
            skLineSegment(sketch, "E880.bottom", {"start": v(-23.91, 2.58) * mm, "end": v(-23.5, 2.58) * mm});
            skLineSegment(sketch, "E880.top", {"start": v(-23.91, -20.7) * mm, "end": v(-23.5, -20.7) * mm});
            skLineSegment(sketch, "E880.left", {"start": v(-23.91, 2.58) * mm, "end": v(-23.91, 2.28) * mm});
            skLineSegment(sketch, "E880.right", {"start": v(-23.5, 1.67) * mm, "end": v(-23.5, -9.35) * mm});
            skLineSegment(sketch, "E881.trimOffspring", {"start": v(-10.2, -9.35) * mm, "end": v(-10.2, 2.28) * mm});
            skLineSegment(sketch, "E882.trimOffspring", {"start": v(-23.91, -10.06) * mm, "end": v(-25.9, -10.06) * mm});
            skLineSegment(sketch, "E883.trimOffspring", {"start": v(-23.91, -10.06) * mm, "end": v(-23.91, -20.7) * mm});
            skLineSegment(sketch, "E884.trimOffspring", {"start": v(-23.5, -10.06) * mm, "end": v(-23.5, -20.34) * mm});
            skLineSegment(sketch, "E885.trimOffspring", {"start": v(-23.91, -9.35) * mm, "end": v(-25.9, -9.35) * mm});
            skLineSegment(sketch, "E886", {"start": v(-10.2, -19.58) * mm, "end": v(-9.76, -19.58) * mm});
            skLineSegment(sketch, "E887", {"start": v(-10.2, -20.34) * mm, "end": v(-9.76, -20.34) * mm});
            skLineSegment(sketch, "E888", {"start": v(-23.5, 2.28) * mm, "end": v(-23.91, 2.28) * mm});
            skLineSegment(sketch, "E889", {"start": v(-23.5, 1.67) * mm, "end": v(-23.91, 1.67) * mm});
            skLineSegment(sketch, "E890.trimOffspring", {"start": v(-23.91, 1.67) * mm, "end": v(-23.91, -9.35) * mm});
            skSolve(sketch);
        }
        {
            var Q0;
            Q0 = qSketchRegion(id + "F42", true);
            var Q1;
            {var subQ0=sQuery(id+"F27.wireOp",EDGE,"E849");var subQ1=sQuery(id+"F27.wireOp",EDGE,"E848");var subQ2=sQuery(id+"F27.wireOp",EDGE,"E847");var subQ3=sQuery(id+"F27.wireOp",EDGE,"E846");var subQ4=sQuery(id+"F27.wireOp",EDGE,"E845");var subQ5=sQuery(id+"F27.wireOp",EDGE,"E844");var subQ6=sQuery(id+"F27.wireOp",EDGE,"E843");var subQ7=sQuery(id+"F27.wireOp",EDGE,"E842");var subQ8=sQuery(id+"F27.wireOp",EDGE,"E841");var subQ9=sQuery(id+"F27.wireOp",EDGE,"E840");var subQ10=sQuery(id+"F27.wireOp",EDGE,"E839");var subQ11=sQuery(id+"F27.wireOp",EDGE,"E838");var subQ12=sQuery(id+"F27.wireOp",EDGE,"E837");var subQ13=sQuery(id+"F27.wireOp",EDGE,"E836");var subQ14=sQuery(id+"F27.wireOp",EDGE,"E835");var subQ15=sQuery(id+"F27.wireOp",EDGE,"E834");var subQ16=sQuery(id+"F27.wireOp",EDGE,"E833");var subQ17=sQuery(id+"F27.wireOp",EDGE,"E832");var subQ18=sQuery(id+"F27.wireOp",EDGE,"E831");var subQ19=sQuery(id+"F27.wireOp",EDGE,"E830");var subQ20=sQuery(id+"F27.wireOp",EDGE,"E829");var subQ21=sQuery(id+"F27.wireOp",EDGE,"E828");var subQ22=sQuery(id+"F27.wireOp",EDGE,"E827");var subQ23=sQuery(id+"F27.wireOp",EDGE,"E826");var subQ24=sQuery(id+"F27.wireOp",EDGE,"E825");var subQ25=sQuery(id+"F27.wireOp",EDGE,"E824");var subQ26=sQuery(id+"F27.wireOp",EDGE,"E823");var subQ27=sQuery(id+"F27.wireOp",EDGE,"E822");var subQ28=sQuery(id+"F27.wireOp",EDGE,"E821");var subQ29=sQuery(id+"F27.wireOp",EDGE,"E820");var subQ30=sQuery(id+"F27.wireOp",EDGE,"E819");var subQ31=sQuery(id+"F27.wireOp",EDGE,"E818");var subQ32=sQuery(id+"F27.wireOp",EDGE,"E817");var subQ33=sQuery(id+"F27.wireOp",EDGE,"E816");var subQ34=sQuery(id+"F27.wireOp",EDGE,"E815");var subQ35=sQuery(id+"F27.wireOp",EDGE,"E814");var subQ36=sQuery(id+"F27.wireOp",EDGE,"E813");var subQ37=sQuery(id+"F27.wireOp",EDGE,"E812");var subQ38=sQuery(id+"F27.wireOp",EDGE,"E811");var subQ39=sQuery(id+"F27.wireOp",EDGE,"E810");var subQ40=sQuery(id+"F27.wireOp",EDGE,"E809");var subQ41=sQuery(id+"F27.wireOp",EDGE,"E808");var subQ42=sQuery(id+"F27.wireOp",EDGE,"E807");var subQ43=sQuery(id+"F27.wireOp",EDGE,"E806");var subQ44=sQuery(id+"F27.wireOp",EDGE,"E805");var subQ45=sQuery(id+"F27.wireOp",EDGE,"E804");var subQ46=sQuery(id+"F27.wireOp",EDGE,"E803");var subQ47=sQuery(id+"F27.wireOp",EDGE,"E802");var subQ48=sQuery(id+"F27.wireOp",EDGE,"E801");var subQ49=sQuery(id+"F27.wireOp",EDGE,"E800");var subQ50=sQuery(id+"F27.wireOp",EDGE,"E799");var subQ51=sQuery(id+"F27.wireOp",EDGE,"E798");var subQ52=sQuery(id+"F27.wireOp",EDGE,"E797");var subQ53=sQuery(id+"F27.wireOp",EDGE,"E796");var subQ54=sQuery(id+"F27.wireOp",EDGE,"E795");var subQ55=sQuery(id+"F27.wireOp",EDGE,"E794");var subQ56=sQuery(id+"F27.wireOp",EDGE,"E793");var subQ57=sQuery(id+"F27.wireOp",EDGE,"E792");var subQ58=sQuery(id+"F27.wireOp",EDGE,"E791");var subQ59=sQuery(id+"F27.wireOp",EDGE,"E790");var subQ60=sQuery(id+"F27.wireOp",EDGE,"E789");var subQ61=sQuery(id+"F27.wireOp",EDGE,"E788");var subQ62=sQuery(id+"F27.wireOp",EDGE,"E787");var subQ63=sQuery(id+"F27.wireOp",EDGE,"E786");var subQ64=sQuery(id+"F27.wireOp",EDGE,"E785");var subQ65=sQuery(id+"F27.wireOp",EDGE,"E784");var subQ66=sQuery(id+"F27.wireOp",EDGE,"E783");var subQ67=sQuery(id+"F27.wireOp",EDGE,"E782");var subQ68=sQuery(id+"F27.wireOp",EDGE,"E781");var subQ69=sQuery(id+"F27.wireOp",EDGE,"E780");var subQ70=sQuery(id+"F27.wireOp",EDGE,"E779");var subQ71=sQuery(id+"F27.wireOp",EDGE,"E778");var subQ72=sQuery(id+"F27.wireOp",EDGE,"E777");var subQ73=sQuery(id+"F27.wireOp",EDGE,"E776");var subQ74=sQuery(id+"F27.wireOp",EDGE,"E775");var subQ75=sQuery(id+"F27.wireOp",EDGE,"E774");var subQ76=sQuery(id+"F27.wireOp",EDGE,"E773");var subQ77=sQuery(id+"F27.wireOp",EDGE,"E772");var subQ78=sQuery(id+"F27.wireOp",EDGE,"E771");var subQ79=sQuery(id+"F27.wireOp",EDGE,"E770");var subQ80=sQuery(id+"F27.wireOp",EDGE,"E769");var subQ81=sQuery(id+"F27.wireOp",EDGE,"E768");var subQ82=sQuery(id+"F27.wireOp",EDGE,"E767");var subQ83=sQuery(id+"F27.wireOp",EDGE,"E766");var subQ84=sQuery(id+"F27.wireOp",EDGE,"E765");var subQ85=sQuery(id+"F27.wireOp",EDGE,"E764");var subQ86=sQuery(id+"F27.wireOp",EDGE,"E763");var subQ87=sQuery(id+"F27.wireOp",EDGE,"E762");var subQ88=sQuery(id+"F27.wireOp",EDGE,"E761");var subQ89=sQuery(id+"F27.wireOp",EDGE,"E760");var subQ90=sQuery(id+"F27.wireOp",EDGE,"E759");var subQ91=sQuery(id+"F27.wireOp",EDGE,"E758");var subQ92=sQuery(id+"F27.wireOp",EDGE,"E757");var subQ93=sQuery(id+"F27.wireOp",EDGE,"E756");var subQ94=sQuery(id+"F27.wireOp",EDGE,"E755");var subQ95=sQuery(id+"F27.wireOp",EDGE,"E754");var subQ96=sQuery(id+"F27.wireOp",EDGE,"E753");var subQ97=sQuery(id+"F27.wireOp",EDGE,"E752");var subQ98=sQuery(id+"F27.wireOp",EDGE,"E751");var subQ99=sQuery(id+"F27.wireOp",EDGE,"E750");var subQ100=sQuery(id+"F27.wireOp",EDGE,"E749");var subQ101=sQuery(id+"F27.wireOp",EDGE,"E748");var subQ102=sQuery(id+"F27.wireOp",EDGE,"E747");var subQ103=sQuery(id+"F27.wireOp",EDGE,"E746");var subQ104=sQuery(id+"F27.wireOp",EDGE,"E745");var subQ105=sQuery(id+"F27.wireOp",EDGE,"E744");var subQ106=sQuery(id+"F27.wireOp",EDGE,"E743");var subQ107=sQuery(id+"F27.wireOp",EDGE,"E742");var subQ108=sQuery(id+"F27.wireOp",EDGE,"E741");var subQ109=sQuery(id+"F27.wireOp",EDGE,"E740");var subQ110=sQuery(id+"F27.wireOp",EDGE,"E739");var subQ111=sQuery(id+"F27.wireOp",EDGE,"E738");var subQ112=sQuery(id+"F27.wireOp",EDGE,"E737");var subQ113=sQuery(id+"F27.wireOp",EDGE,"E736");var subQ114=sQuery(id+"F27.wireOp",EDGE,"E735");var subQ115=sQuery(id+"F27.wireOp",EDGE,"E734");var subQ116=sQuery(id+"F27.wireOp",EDGE,"E733");var subQ117=sQuery(id+"F27.wireOp",EDGE,"E732");var subQ118=sQuery(id+"F27.wireOp",EDGE,"E731");var subQ119=sQuery(id+"F27.wireOp",EDGE,"E730");var subQ120=sQuery(id+"F27.wireOp",EDGE,"E729");var subQ121=sQuery(id+"F27.wireOp",EDGE,"E728");var subQ122=sQuery(id+"F27.wireOp",EDGE,"E727");var subQ123=sQuery(id+"F27.wireOp",EDGE,"E726");var subQ124=sQuery(id+"F27.wireOp",EDGE,"E725");var subQ125=sQuery(id+"F27.wireOp",EDGE,"E724");var subQ126=sQuery(id+"F27.wireOp",EDGE,"E723");var subQ127=sQuery(id+"F27.wireOp",EDGE,"E722");var subQ128=sQuery(id+"F27.wireOp",EDGE,"E721");var subQ129=sQuery(id+"F27.wireOp",EDGE,"E720");var subQ130=sQuery(id+"F27.wireOp",EDGE,"E719");var subQ131=sQuery(id+"F27.wireOp",EDGE,"E718");var subQ132=sQuery(id+"F27.wireOp",EDGE,"E717");var subQ133=sQuery(id+"F27.wireOp",EDGE,"E716");var subQ134=sQuery(id+"F27.wireOp",EDGE,"E715");var subQ135=sQuery(id+"F27.wireOp",EDGE,"E714");var subQ136=sQuery(id+"F27.wireOp",EDGE,"E713");var subQ137=sQuery(id+"F27.wireOp",EDGE,"E712");var subQ138=sQuery(id+"F27.wireOp",EDGE,"E711");var subQ139=sQuery(id+"F27.wireOp",EDGE,"E710");var subQ140=sQuery(id+"F27.wireOp",EDGE,"E709");var subQ141=sQuery(id+"F27.wireOp",EDGE,"E708");var subQ142=sQuery(id+"F27.wireOp",EDGE,"E707");var subQ143=sQuery(id+"F27.wireOp",EDGE,"E706");var subQ144=sQuery(id+"F27.wireOp",EDGE,"E705");var subQ145=sQuery(id+"F27.wireOp",EDGE,"E704");var subQ146=sQuery(id+"F27.wireOp",EDGE,"E703");var subQ147=sQuery(id+"F27.wireOp",EDGE,"E702");var subQ148=sQuery(id+"F27.wireOp",EDGE,"E701");var subQ149=sQuery(id+"F27.wireOp",EDGE,"E700");var subQ150=sQuery(id+"F27.wireOp",EDGE,"E699");var subQ151=sQuery(id+"F27.wireOp",EDGE,"E698");var subQ152=sQuery(id+"F27.wireOp",EDGE,"E697");var subQ153=sQuery(id+"F27.wireOp",EDGE,"E696");var subQ154=sQuery(id+"F27.wireOp",EDGE,"E695");var subQ155=sQuery(id+"F27.wireOp",EDGE,"E694");var subQ156=sQuery(id+"F27.wireOp",EDGE,"E693");var subQ157=sQuery(id+"F27.wireOp",EDGE,"E692");var subQ158=sQuery(id+"F27.wireOp",EDGE,"E691");var subQ159=sQuery(id+"F27.wireOp",EDGE,"E690");var subQ160=sQuery(id+"F27.wireOp",EDGE,"E689");var subQ161=sQuery(id+"F27.wireOp",EDGE,"E688");var subQ162=sQuery(id+"F27.wireOp",EDGE,"E687");var subQ163=sQuery(id+"F27.wireOp",EDGE,"E686");var subQ164=sQuery(id+"F27.wireOp",EDGE,"E685");var subQ165=sQuery(id+"F27.wireOp",EDGE,"E684");var subQ166=sQuery(id+"F27.wireOp",EDGE,"E683");var subQ167=sQuery(id+"F27.wireOp",EDGE,"E682");var subQ168=sQuery(id+"F27.wireOp",EDGE,"E681");var subQ169=sQuery(id+"F27.wireOp",EDGE,"E680");var subQ170=sQuery(id+"F27.wireOp",EDGE,"E679");var subQ171=sQuery(id+"F27.wireOp",EDGE,"E678");var subQ172=sQuery(id+"F27.wireOp",EDGE,"E677");var subQ173=sQuery(id+"F27.wireOp",EDGE,"E676");var subQ174=sQuery(id+"F27.wireOp",EDGE,"E675");var subQ175=sQuery(id+"F27.wireOp",EDGE,"E674");var subQ176=sQuery(id+"F27.wireOp",EDGE,"E673");var subQ177=sQuery(id+"F27.wireOp",EDGE,"E672");var subQ178=sQuery(id+"F27.wireOp",EDGE,"E671");var subQ179=sQuery(id+"F27.wireOp",EDGE,"E670");var subQ180=sQuery(id+"F27.wireOp",EDGE,"E669");var subQ181=sQuery(id+"F27.wireOp",EDGE,"E668");var subQ182=sQuery(id+"F27.wireOp",EDGE,"E667");var subQ183=sQuery(id+"F27.wireOp",EDGE,"E666");var subQ184=sQuery(id+"F27.wireOp",EDGE,"E665");var subQ185=sQuery(id+"F27.wireOp",EDGE,"E664");var subQ186=sQuery(id+"F27.wireOp",EDGE,"E663");var subQ187=sQuery(id+"F27.wireOp",EDGE,"E662");var subQ188=sQuery(id+"F27.wireOp",EDGE,"E661");var subQ189=sQuery(id+"F27.wireOp",EDGE,"E660");var subQ190=sQuery(id+"F27.wireOp",EDGE,"E659");var subQ191=sQuery(id+"F27.wireOp",EDGE,"E658");var subQ192=sQuery(id+"F27.wireOp",EDGE,"E657");var subQ193=sQuery(id+"F27.wireOp",EDGE,"E656");var subQ194=sQuery(id+"F27.wireOp",EDGE,"E655");var subQ195=sQuery(id+"F27.wireOp",EDGE,"E858");var subQ196=sQuery(id+"F27.wireOp",EDGE,"E857");var subQ197=sQuery(id+"F27.wireOp",EDGE,"E856");var subQ198=sQuery(id+"F27.wireOp",EDGE,"E854");var subQ199=sQuery(id+"F27.wireOp",EDGE,"E853");var subQ200=sQuery(id+"F27.wireOp",EDGE,"E850");var subQ201=sQuery(id+"F27.wireOp",EDGE,"E325");var subQ202=sQuery(id+"F27.wireOp",EDGE,"E324");var subQ203=sQuery(id+"F27.wireOp",EDGE,"E323");var subQ204=sQuery(id+"F27.wireOp",EDGE,"E321");var subQ205=sQuery(id+"F27.wireOp",EDGE,"E320");var subQ206=sQuery(id+"F27.wireOp",EDGE,"E319");var subQ207=sQuery(id+"F27.wireOp",EDGE,"E318");var subQ208=sQuery(id+"F27.wireOp",EDGE,"E317");var subQ209=sQuery(id+"F27.wireOp",EDGE,"E316");var subQ210=sQuery(id+"F27.wireOp",EDGE,"E315");var subQ211=sQuery(id+"F27.wireOp",EDGE,"E314");var subQ212=sQuery(id+"F27.wireOp",EDGE,"E313");var subQ213=sQuery(id+"F27.wireOp",EDGE,"E312");var subQ214=sQuery(id+"F27.wireOp",EDGE,"E311");var subQ215=sQuery(id+"F27.wireOp",EDGE,"E310");var subQ216=sQuery(id+"F27.wireOp",EDGE,"E309");var subQ217=sQuery(id+"F27.wireOp",EDGE,"E308");var subQ218=sQuery(id+"F27.wireOp",EDGE,"E307");var subQ219=sQuery(id+"F27.wireOp",EDGE,"E306");var subQ220=sQuery(id+"F27.wireOp",EDGE,"E305");var subQ221=sQuery(id+"F27.wireOp",EDGE,"E304");var subQ222=sQuery(id+"F27.wireOp",EDGE,"E303");var subQ223=sQuery(id+"F27.wireOp",EDGE,"E302");var subQ224=sQuery(id+"F27.wireOp",EDGE,"E301");var subQ225=sQuery(id+"F27.wireOp",EDGE,"E300");var subQ226=sQuery(id+"F27.wireOp",EDGE,"E299");var subQ227=sQuery(id+"F27.wireOp",EDGE,"E298");var subQ228=sQuery(id+"F27.wireOp",EDGE,"E297");var subQ229=sQuery(id+"F27.wireOp",EDGE,"E296");var subQ230=sQuery(id+"F27.wireOp",EDGE,"E295");var subQ231=sQuery(id+"F27.wireOp",EDGE,"E294");var subQ232=sQuery(id+"F27.wireOp",EDGE,"E293");var subQ233=sQuery(id+"F27.wireOp",EDGE,"E292");var subQ234=sQuery(id+"F27.wireOp",EDGE,"E291");var subQ235=sQuery(id+"F27.wireOp",EDGE,"E290");var subQ236=sQuery(id+"F27.wireOp",EDGE,"E289");var subQ237=sQuery(id+"F27.wireOp",EDGE,"E288");var subQ238=sQuery(id+"F27.wireOp",EDGE,"E287");var subQ239=sQuery(id+"F27.wireOp",EDGE,"E286");var subQ240=sQuery(id+"F27.wireOp",EDGE,"E285");var subQ241=sQuery(id+"F27.wireOp",EDGE,"E284");var subQ242=sQuery(id+"F27.wireOp",EDGE,"E283");var subQ243=sQuery(id+"F27.wireOp",EDGE,"E282");var subQ244=sQuery(id+"F27.wireOp",EDGE,"E281");var subQ245=sQuery(id+"F27.wireOp",EDGE,"E280");var subQ246=sQuery(id+"F27.wireOp",EDGE,"E279");var subQ247=sQuery(id+"F27.wireOp",EDGE,"E278");var subQ248=sQuery(id+"F27.wireOp",EDGE,"E277");var subQ249=sQuery(id+"F27.wireOp",EDGE,"E276");var subQ250=sQuery(id+"F27.wireOp",EDGE,"E275");var subQ251=sQuery(id+"F27.wireOp",EDGE,"E274");var subQ252=sQuery(id+"F27.wireOp",EDGE,"E273");var subQ253=sQuery(id+"F27.wireOp",EDGE,"E272");var subQ254=sQuery(id+"F27.wireOp",EDGE,"E271");var subQ255=sQuery(id+"F27.wireOp",EDGE,"E270");var subQ256=sQuery(id+"F27.wireOp",EDGE,"E269");var subQ257=sQuery(id+"F27.wireOp",EDGE,"E268");var subQ258=sQuery(id+"F27.wireOp",EDGE,"E267");var subQ259=sQuery(id+"F27.wireOp",EDGE,"E266");var subQ260=sQuery(id+"F27.wireOp",EDGE,"E265");var subQ261=sQuery(id+"F27.wireOp",EDGE,"E264");var subQ262=sQuery(id+"F27.wireOp",EDGE,"E263");var subQ263=sQuery(id+"F27.wireOp",EDGE,"E262");var subQ264=sQuery(id+"F27.wireOp",EDGE,"E261");var subQ265=sQuery(id+"F27.wireOp",EDGE,"E260");var subQ266=sQuery(id+"F27.wireOp",EDGE,"E259");var subQ267=sQuery(id+"F27.wireOp",EDGE,"E258");var subQ268=sQuery(id+"F27.wireOp",EDGE,"E257");var subQ269=sQuery(id+"F27.wireOp",EDGE,"E256");var subQ270=sQuery(id+"F27.wireOp",EDGE,"E255");var subQ271=sQuery(id+"F27.wireOp",EDGE,"E254");var subQ272=sQuery(id+"F27.wireOp",EDGE,"E253");var subQ273=sQuery(id+"F27.wireOp",EDGE,"E252");var subQ274=sQuery(id+"F27.wireOp",EDGE,"E251");var subQ275=sQuery(id+"F27.wireOp",EDGE,"E250");var subQ276=sQuery(id+"F27.wireOp",EDGE,"E249");var subQ277=sQuery(id+"F27.wireOp",EDGE,"E248");var subQ278=sQuery(id+"F27.wireOp",EDGE,"E247");var subQ279=sQuery(id+"F27.wireOp",EDGE,"E246");var subQ280=sQuery(id+"F27.wireOp",EDGE,"E245");var subQ281=sQuery(id+"F27.wireOp",EDGE,"E244");var subQ282=sQuery(id+"F27.wireOp",EDGE,"E243");var subQ283=sQuery(id+"F27.wireOp",EDGE,"E242");var subQ284=sQuery(id+"F27.wireOp",EDGE,"E241");var subQ285=sQuery(id+"F27.wireOp",EDGE,"E182");var subQ286=sQuery(id+"F27.wireOp",EDGE,"E181");var subQ287=sQuery(id+"F27.wireOp",EDGE,"E180");var subQ288=sQuery(id+"F27.wireOp",EDGE,"E179");var subQ289=sQuery(id+"F27.wireOp",EDGE,"E178");var subQ290=sQuery(id+"F27.wireOp",EDGE,"E177");var subQ291=sQuery(id+"F27.wireOp",EDGE,"E176");var subQ292=sQuery(id+"F27.wireOp",EDGE,"E175");var subQ293=sQuery(id+"F27.wireOp",EDGE,"E174");var subQ294=sQuery(id+"F27.wireOp",EDGE,"E173");var subQ295=sQuery(id+"F27.wireOp",EDGE,"E172");var subQ296=sQuery(id+"F27.wireOp",EDGE,"E171");var subQ297=sQuery(id+"F27.wireOp",EDGE,"E170");var subQ298=sQuery(id+"F27.wireOp",EDGE,"E123");var subQ299=sQuery(id+"F0.wireOp",EDGE,"E7.rect.bottom");var subQ302=sQuery(id+"F0.wireOp",EDGE,"E7.rect.right");var subQ303=sQuery(id+"F0.wireOp",EDGE,"E7.rect.left");var subQ304=sQuery(id+"F0.wireOp",EDGE,"E7.rect.top");var subQ305=sQuery(id+"F0.wireOp",EDGE,"E5.MirrorC");var subQ306=sQuery(id+"F0.wireOp",EDGE,"E3");var subQ307=sQuery(id+"F0.wireOp",EDGE,"E2");var subQ308=sQuery(id+"F0.wireOp",EDGE,"E1");var subQ309=makeQuery(id+"F1.opExtrude","CAP_FACE",FACE,{"disambiguationData":[OSD([subQ308,subQ307,subQ306,subQ305,subQ299,subQ304,subQ303,subQ302])],"isStart":false});var subQ312=makeQuery(id+"F6.opShell","OFFSET_FACE",FACE,{"disambiguationData":[OSD([subQ308,subQ307,subQ306,subQ305,subQ299,subQ304,subQ303,subQ302]),TDD([subQ309])]});Q1=makeQuery(id+"F29.boolean.opBoolean","MERGE",FACE,{"derivedFrom":[makeQuery(id+"F28.boolean.opBoolean","SPLIT",FACE,{"disambiguationData":[TD([makeQuery(id+"F28.opExtrude","SWEPT_FACE",FACE,{"disambiguationData":[OSD([subQ298])]})])],"derivedFrom":subQ312}),makeQuery(id+"F28.boolean.opBoolean","SPLIT",FACE,{"disambiguationData":[TD([makeQuery(id+"F28.opExtrude","SWEPT_FACE",FACE,{"disambiguationData":[OSD([subQ262])]})])],"derivedFrom":subQ312}),makeQuery(id+"F28.boolean.opBoolean","SPLIT",FACE,{"disambiguationData":[TD([makeQuery(id+"F28.opExtrude","SWEPT_FACE",FACE,{"disambiguationData":[OSD([subQ297])]})])],"derivedFrom":subQ312}),makeQuery(id+"F29.opExtrude","CAP_FACE",FACE,{"disambiguationData":[OSD([subQ298,sQuery(id+"F27.wireOp",EDGE,"E124"),sQuery(id+"F27.wireOp",EDGE,"E125"),sQuery(id+"F27.wireOp",EDGE,"E126"),sQuery(id+"F27.wireOp",EDGE,"E127"),sQuery(id+"F27.wireOp",EDGE,"E128"),sQuery(id+"F27.wireOp",EDGE,"E129"),sQuery(id+"F27.wireOp",EDGE,"E130"),sQuery(id+"F27.wireOp",EDGE,"E131"),sQuery(id+"F27.wireOp",EDGE,"E132"),sQuery(id+"F27.wireOp",EDGE,"E133"),sQuery(id+"F27.wireOp",EDGE,"E134"),sQuery(id+"F27.wireOp",EDGE,"E135"),sQuery(id+"F27.wireOp",EDGE,"E136"),sQuery(id+"F27.wireOp",EDGE,"E137"),sQuery(id+"F27.wireOp",EDGE,"E138"),sQuery(id+"F27.wireOp",EDGE,"E139"),sQuery(id+"F27.wireOp",EDGE,"E140"),sQuery(id+"F27.wireOp",EDGE,"E141"),sQuery(id+"F27.wireOp",EDGE,"E142"),sQuery(id+"F27.wireOp",EDGE,"E143"),sQuery(id+"F27.wireOp",EDGE,"E144"),sQuery(id+"F27.wireOp",EDGE,"E145"),sQuery(id+"F27.wireOp",EDGE,"E146"),sQuery(id+"F27.wireOp",EDGE,"E147"),sQuery(id+"F27.wireOp",EDGE,"E148"),sQuery(id+"F27.wireOp",EDGE,"E149"),sQuery(id+"F27.wireOp",EDGE,"E150"),sQuery(id+"F27.wireOp",EDGE,"E151"),sQuery(id+"F27.wireOp",EDGE,"E152"),sQuery(id+"F27.wireOp",EDGE,"E153"),sQuery(id+"F27.wireOp",EDGE,"E154"),sQuery(id+"F27.wireOp",EDGE,"E155"),sQuery(id+"F27.wireOp",EDGE,"E156"),sQuery(id+"F27.wireOp",EDGE,"E157"),sQuery(id+"F27.wireOp",EDGE,"E158"),sQuery(id+"F27.wireOp",EDGE,"E159"),sQuery(id+"F27.wireOp",EDGE,"E160"),sQuery(id+"F27.wireOp",EDGE,"E161"),sQuery(id+"F27.wireOp",EDGE,"E162"),sQuery(id+"F27.wireOp",EDGE,"E163"),sQuery(id+"F27.wireOp",EDGE,"E164"),sQuery(id+"F27.wireOp",EDGE,"E165"),sQuery(id+"F27.wireOp",EDGE,"E166"),sQuery(id+"F27.wireOp",EDGE,"E167"),sQuery(id+"F27.wireOp",EDGE,"E168"),sQuery(id+"F27.wireOp",EDGE,"E169"),subQ297,subQ296,subQ295,subQ294,subQ293,subQ292,subQ291,subQ290,subQ289,subQ288,subQ287,subQ286,subQ285,sQuery(id+"F27.wireOp",EDGE,"E183"),sQuery(id+"F27.wireOp",EDGE,"E184"),sQuery(id+"F27.wireOp",EDGE,"E185"),sQuery(id+"F27.wireOp",EDGE,"E186"),sQuery(id+"F27.wireOp",EDGE,"E187"),sQuery(id+"F27.wireOp",EDGE,"E188"),sQuery(id+"F27.wireOp",EDGE,"E189"),sQuery(id+"F27.wireOp",EDGE,"E190"),sQuery(id+"F27.wireOp",EDGE,"E191"),sQuery(id+"F27.wireOp",EDGE,"E192"),sQuery(id+"F27.wireOp",EDGE,"E193"),sQuery(id+"F27.wireOp",EDGE,"E194"),sQuery(id+"F27.wireOp",EDGE,"E195"),sQuery(id+"F27.wireOp",EDGE,"E196"),sQuery(id+"F27.wireOp",EDGE,"E197"),sQuery(id+"F27.wireOp",EDGE,"E198"),sQuery(id+"F27.wireOp",EDGE,"E199"),sQuery(id+"F27.wireOp",EDGE,"E200"),sQuery(id+"F27.wireOp",EDGE,"E201"),sQuery(id+"F27.wireOp",EDGE,"E202"),sQuery(id+"F27.wireOp",EDGE,"E203"),sQuery(id+"F27.wireOp",EDGE,"E204"),sQuery(id+"F27.wireOp",EDGE,"E205"),sQuery(id+"F27.wireOp",EDGE,"E206"),sQuery(id+"F27.wireOp",EDGE,"E207"),sQuery(id+"F27.wireOp",EDGE,"E208"),sQuery(id+"F27.wireOp",EDGE,"E209"),sQuery(id+"F27.wireOp",EDGE,"E210"),sQuery(id+"F27.wireOp",EDGE,"E211"),sQuery(id+"F27.wireOp",EDGE,"E212"),sQuery(id+"F27.wireOp",EDGE,"E213"),sQuery(id+"F27.wireOp",EDGE,"E214"),sQuery(id+"F27.wireOp",EDGE,"E215"),sQuery(id+"F27.wireOp",EDGE,"E216"),sQuery(id+"F27.wireOp",EDGE,"E217"),sQuery(id+"F27.wireOp",EDGE,"E218"),sQuery(id+"F27.wireOp",EDGE,"E219"),sQuery(id+"F27.wireOp",EDGE,"E220"),sQuery(id+"F27.wireOp",EDGE,"E221"),sQuery(id+"F27.wireOp",EDGE,"E222"),sQuery(id+"F27.wireOp",EDGE,"E223"),sQuery(id+"F27.wireOp",EDGE,"E224"),sQuery(id+"F27.wireOp",EDGE,"E225"),sQuery(id+"F27.wireOp",EDGE,"E226"),sQuery(id+"F27.wireOp",EDGE,"E227"),sQuery(id+"F27.wireOp",EDGE,"E228"),sQuery(id+"F27.wireOp",EDGE,"E229"),sQuery(id+"F27.wireOp",EDGE,"E230"),sQuery(id+"F27.wireOp",EDGE,"E231"),sQuery(id+"F27.wireOp",EDGE,"E232"),sQuery(id+"F27.wireOp",EDGE,"E233"),sQuery(id+"F27.wireOp",EDGE,"E234"),sQuery(id+"F27.wireOp",EDGE,"E235"),sQuery(id+"F27.wireOp",EDGE,"E236"),sQuery(id+"F27.wireOp",EDGE,"E237"),sQuery(id+"F27.wireOp",EDGE,"E238"),sQuery(id+"F27.wireOp",EDGE,"E239"),sQuery(id+"F27.wireOp",EDGE,"E240"),subQ284,subQ283,subQ282,subQ281,subQ280,subQ279,subQ278,subQ277,subQ276,subQ275,subQ274,subQ273,subQ272,subQ271,subQ270,subQ269,subQ268,subQ267,subQ266,subQ265,subQ264,subQ263,subQ262,subQ261,subQ260,subQ259,subQ258,subQ257,subQ256,subQ255,subQ254,subQ253,subQ252,subQ251,subQ250,subQ249,subQ248,subQ247,subQ246,subQ245,subQ244,subQ243,subQ242,subQ241,subQ240,subQ239,subQ238,subQ237,subQ236,subQ235,subQ234,subQ233,subQ232,subQ231,subQ230,subQ229,subQ228,subQ227,subQ226,subQ225,subQ224,subQ223,subQ222,subQ221,subQ220,subQ219,subQ218,subQ217,subQ216,subQ215,subQ214,subQ213,subQ212,subQ211,subQ210,subQ209,subQ208,subQ207,subQ206,subQ205,subQ204,sQuery(id+"F27.wireOp",EDGE,"E322"),subQ203,subQ202,subQ201,subQ200,sQuery(id+"F27.wireOp",EDGE,"E851"),sQuery(id+"F27.wireOp",EDGE,"E852"),subQ199,subQ198,sQuery(id+"F27.wireOp",EDGE,"E855"),subQ197,subQ196,subQ195])],"isStart":false}),makeQuery(id+"F29.opExtrude","CAP_FACE",FACE,{"disambiguationData":[OSD([subQ194,subQ193,subQ192,subQ191,subQ190,subQ189,subQ188,subQ187,subQ186,subQ185,subQ184,subQ183,subQ182,subQ181,subQ180,subQ179,subQ178,subQ177,subQ176,subQ175,subQ174,subQ173,subQ172,subQ171,subQ170,subQ169,subQ168,subQ167,subQ166,subQ165,subQ164,subQ163,subQ162,subQ161,subQ160,subQ159,subQ158,subQ157,subQ156,subQ155,subQ154,subQ153,subQ152,subQ151,subQ150,subQ149])],"isStart":false}),makeQuery(id+"F29.opExtrude","CAP_FACE",FACE,{"disambiguationData":[OSD([subQ148,subQ147,subQ146,subQ145,subQ144,subQ143,subQ142,subQ141,subQ140,subQ139,subQ138,subQ137,subQ136,subQ135,subQ134,subQ133,subQ132,subQ131,subQ130,subQ129,subQ128,subQ127,subQ126,subQ125,subQ124,subQ123,subQ122,subQ121,subQ120,subQ119,subQ118,subQ117,subQ116,subQ115,subQ114,subQ113,subQ112,subQ111,subQ110,subQ109,subQ108,subQ107,subQ106,subQ105,subQ104,subQ103,subQ102,subQ101,subQ100])],"isStart":false}),makeQuery(id+"F29.opExtrude","CAP_FACE",FACE,{"disambiguationData":[OSD([subQ99,subQ98,subQ97,subQ96,subQ95,subQ94,subQ93,subQ92,subQ91,subQ90,subQ89,subQ88,subQ87,subQ86,subQ85,subQ84,subQ83,subQ82,subQ81,subQ80,subQ79,subQ78,subQ77,subQ76,subQ75,subQ74,subQ73,subQ72,subQ71,subQ70,subQ69,subQ68,subQ67,subQ66,subQ65,subQ64,subQ63,subQ62,subQ61,subQ60,subQ59,subQ58,subQ57,subQ56,subQ55,subQ54,subQ53,subQ52,subQ51,subQ50,subQ49,subQ48,subQ47,subQ46,subQ45,subQ44])],"isStart":false}),makeQuery(id+"F29.opExtrude","CAP_FACE",FACE,{"disambiguationData":[OSD([subQ43,subQ42,subQ41,subQ40,subQ39,subQ38,subQ37,subQ36,subQ35,subQ34,subQ33,subQ32,subQ31,subQ30,subQ29,subQ28,subQ27,subQ26,subQ25,subQ24,subQ23,subQ22,subQ21,subQ20,subQ19,subQ18,subQ17,subQ16,subQ15,subQ14,subQ13,subQ12,subQ11,subQ10,subQ9,subQ8,subQ7,subQ6,subQ5,subQ4,subQ3,subQ2,subQ1,subQ0])],"isStart":false})]});}
            extrude(context, id + "F43", {"entities" : qUnion([Q0]), "operationType" : NewBodyOperationType.ADD, "endBound" : BoundingType.UP_TO_SURFACE, "endBoundEntityFace" : qUnion([Q1]), "depth" : 25 * mm});
        }
        {
            var Q0;
            {var subQ0=sQuery(id+"F0.wireOp",EDGE,"E7.rect.right");var subQ2=sQuery(id+"F0.wireOp",EDGE,"E7.rect.bottom");var subQ3=makeQuery(id+"F1.opExtrude","SWEPT_FACE",FACE,{"disambiguationData":[OSD([subQ2])]});var subQ8=sQuery(id+"F0.wireOp",EDGE,"E7.rect.left");var subQ17=sQuery(id+"F0.wireOp",EDGE,"E7.rect.top");var subQ19=sQuery(id+"F0.wireOp",EDGE,"E5.MirrorC");var subQ20=sQuery(id+"F0.wireOp",EDGE,"E3");var subQ21=sQuery(id+"F0.wireOp",EDGE,"E2");var subQ22=sQuery(id+"F0.wireOp",EDGE,"E1");var subQ23=makeQuery(id+"F1.opExtrude","CAP_FACE",FACE,{"disambiguationData":[OSD([subQ22,subQ21,subQ20,subQ19,subQ2,subQ17,subQ8,subQ0])],"isStart":true});Q0=makeQuery(id+"F26.boolean.opBoolean","MERGE",FACE,{"derivedFrom":[makeQuery(id+"F6.opShell","OFFSET_FACE",FACE,{"disambiguationData":[OSD([subQ22,subQ21,subQ20,subQ19,subQ2,subQ17,subQ8,subQ0]),TDD([subQ23]),OD(2.0)]}),makeQuery(id+"F14.boolean.opBoolean","SPLIT",FACE,{"disambiguationData":[TD([makeQuery(id+"F1.opExtrude","SWEPT_FACE",FACE,{"disambiguationData":[OSD([subQ22])]})])],"derivedFrom":makeQuery(id+"F6.opShell","OFFSET_FACE",FACE,{"disambiguationData":[OSD([subQ22,subQ21,subQ20,subQ19,subQ2,subQ17,subQ8,subQ0]),TDD([subQ23]),OD(0.0)]})}),makeQuery(id+"F14.boolean.opBoolean","SPLIT",FACE,{"disambiguationData":[TD([subQ3])],"derivedFrom":makeQuery(id+"F10.boolean.opBoolean","SPLIT",FACE,{"disambiguationData":[TD([subQ3])],"derivedFrom":makeQuery(id+"F6.opShell","OFFSET_FACE",FACE,{"disambiguationData":[OSD([subQ22,subQ21,subQ20,subQ19,subQ2,subQ17,subQ8,subQ0]),TDD([subQ23]),OD(3.0)]})})}),makeQuery(id+"F26.opExtrude","CAP_FACE",FACE,{"disambiguationData":[OSD([sQuery(id+"F25.wireOp",EDGE,"E102.top"),sQuery(id+"F25.wireOp",EDGE,"E102.left"),sQuery(id+"F25.wireOp",EDGE,"E102.right"),sQuery(id+"F25.wireOp",EDGE,"E103.bottom"),sQuery(id+"F25.wireOp",EDGE,"E103.top"),sQuery(id+"F25.wireOp",EDGE,"E103.right"),sQuery(id+"F25.wireOp",EDGE,"E102.bottom"),sQuery(id+"F25.wireOp",EDGE,"E107.top"),sQuery(id+"F25.wireOp",EDGE,"E107.left"),sQuery(id+"F25.wireOp",EDGE,"E107.right")])],"isStart":true}),makeQuery(id+"F26.opExtrude","CAP_FACE",FACE,{"disambiguationData":[OSD([sQuery(id+"F25.wireOp",EDGE,"E105.bottom"),sQuery(id+"F25.wireOp",EDGE,"E105.top"),sQuery(id+"F25.wireOp",EDGE,"E105.left"),sQuery(id+"F25.wireOp",EDGE,"E105.right"),sQuery(id+"F25.wireOp",EDGE,"E106.bottom"),sQuery(id+"F25.wireOp",EDGE,"E106.top"),sQuery(id+"F25.wireOp",EDGE,"E106.right")])],"isStart":true})]});}
            cPlane(context, id + "F44", {"entities" : qUnion([Q0]), "cplaneType" : CPlaneType.OFFSET, "offset" : 0.6 * mm, "oppositeDirection" : true, "width" : 150 * mm, "height" : 150 * mm});
        }
        {
            var Q0;
            Q0=qCreatedBy(id+"F44.planeOp",FACE);
            var sketch = newSketch(context, id + "F45", { "sketchPlane" : qUnion([Q0])});
            skLineSegment(sketch, "E891.bottom", {"start": v(-24.07, 22.32) * mm, "end": v(-9.14, 22.32) * mm});
            skLineSegment(sketch, "E891.top", {"start": v(-24.07, -4.65) * mm, "end": v(-9.14, -4.65) * mm});
            skLineSegment(sketch, "E891.left", {"start": v(-24.07, 22.32) * mm, "end": v(-24.07, -4.65) * mm});
            skLineSegment(sketch, "E891.right", {"start": v(-9.14, 22.32) * mm, "end": v(-9.14, -4.65) * mm});
            skSolve(sketch);
        }
        {
            var Q0;
            Q0 = qSketchRegion(id + "F45", true);
            extrude(context, id + "F46", {"entities" : qUnion([Q0]), "operationType" : NewBodyOperationType.ADD, "depth" : 0.6 * mm});
        }
        {
            var Q0;
            Q0=qCreatedBy(makeId("Top.planeOp"),FACE);
            var sketch = newSketch(context, id + "F47", { "sketchPlane" : qUnion([Q0])});
            skLineSegment(sketch, "E892.bottom", {"start": v(-32.16, -19.74) * mm, "end": v(-31.86, -19.74) * mm});
            skLineSegment(sketch, "E892.top", {"start": v(-32.16, -29.43) * mm, "end": v(-31.86, -29.43) * mm});
            skLineSegment(sketch, "E892.left", {"start": v(-32.16, -19.74) * mm, "end": v(-32.16, -29.43) * mm});
            skLineSegment(sketch, "E892.right", {"start": v(-31.86, -19.74) * mm, "end": v(-31.86, -29.43) * mm});
            skLineSegment(sketch, "E893.bottom", {"start": v(-34.1, 3.13) * mm, "end": v(-31.72, 3.13) * mm});
            skLineSegment(sketch, "E893.top", {"start": v(-34.1, 0.35) * mm, "end": v(-31.72, 0.35) * mm});
            skLineSegment(sketch, "E893.left", {"start": v(-34.1, 3.13) * mm, "end": v(-34.1, 0.35) * mm});
            skLineSegment(sketch, "E893.right", {"start": v(-31.72, 3.13) * mm, "end": v(-31.72, 0.35) * mm});
            skLineSegment(sketch, "E894.bottom", {"start": v(-34.13, -7.9) * mm, "end": v(-31.72, -7.9) * mm});
            skLineSegment(sketch, "E894.top", {"start": v(-34.13, -10.8) * mm, "end": v(-31.72, -10.8) * mm});
            skLineSegment(sketch, "E894.left", {"start": v(-34.13, -7.9) * mm, "end": v(-34.13, -10.8) * mm});
            skLineSegment(sketch, "E894.right", {"start": v(-31.72, -7.9) * mm, "end": v(-31.72, -10.8) * mm});
            skSolve(sketch);
        }
        {
            var Q0;
            Q0 = qSketchRegion(id + "F47", true);
            var Q1;
            Q1=makeQuery(id+"F35.boolean.opBoolean","MERGE",FACE,{"derivedFrom":[makeQuery(id+"F3.boolean.opBoolean","COPY",FACE,{"derivedFrom":makeQuery(id+"F3.opExtrude","SWEPT_FACE",FACE,{"disambiguationData":[OSD([sQuery(id+"F2.wireOp",EDGE,"E14")])]})}),makeQuery(id+"F35.opExtrude","CAP_FACE",FACE,{"disambiguationData":[OSD([sQuery(id+"F34.wireOp",EDGE,"E864")])],"isStart":false}),makeQuery(id+"F35.opExtrude","CAP_FACE",FACE,{"disambiguationData":[OSD([sQuery(id+"F34.wireOp",EDGE,"E865")])],"isStart":false})]});
            extrude(context, id + "F48", {"entities" : qUnion([Q0]), "operationType" : NewBodyOperationType.ADD, "endBound" : BoundingType.UP_TO_SURFACE, "endBoundEntityFace" : qUnion([Q1]), "depth" : 25 * mm});
        }
        {
            var Q0;
            Q0=makeQuery(id+"F35.boolean.opBoolean","MERGE",FACE,{"derivedFrom":[makeQuery(id+"F3.boolean.opBoolean","COPY",FACE,{"derivedFrom":makeQuery(id+"F3.opExtrude","SWEPT_FACE",FACE,{"disambiguationData":[OSD([sQuery(id+"F2.wireOp",EDGE,"E14")])]})}),makeQuery(id+"F35.opExtrude","CAP_FACE",FACE,{"disambiguationData":[OSD([sQuery(id+"F34.wireOp",EDGE,"E864")])],"isStart":false}),makeQuery(id+"F35.opExtrude","CAP_FACE",FACE,{"disambiguationData":[OSD([sQuery(id+"F34.wireOp",EDGE,"E865")])],"isStart":false})]});
            var sketch = newSketch(context, id + "F49", { "sketchPlane" : qUnion([Q0])});
            skText(sketch, "E895", { "text": "12v", "fontName": "OpenSans-Bold.ttf"});
            skText(sketch, "E896", { "text": "L3 L2 L1", "fontName": "OpenSans-Bold.ttf"});
            const initialGuessF49  = {"E895": [0.019, 0, 1, 0, 0.0042], "E896": [-0.00949, -0.00516, 1, 0, 0.00516]};
            skSetInitialGuess(sketch, initialGuessF49);
            skSolve(sketch);
        }
        {
            var Q0;
            Q0 = qSketchRegion(id + "F49", true);
            extrude(context, id + "F50", {"entities" : qUnion([Q0]), "operationType" : NewBodyOperationType.ADD, "depth" : 0.9 * mm});
        }
        {
            var Q0;
            {var subQ1=sQuery(id+"F0.wireOp",EDGE,"E7.rect.top");var subQ2=sQuery(id+"F0.wireOp",EDGE,"E7.rect.right");var subQ9=makeQuery(id+"F1.opExtrude","SWEPT_FACE",FACE,{"disambiguationData":[OSD([subQ1])]});Q0=makeQuery(id+"F19.boolean.opBoolean","SPLIT",FACE,{"disambiguationData":[TD([makeQuery(id+"F1.opExtrude","SWEPT_FACE",FACE,{"disambiguationData":[OSD([subQ2])]})])],"derivedFrom":subQ9});}
            var sketch = newSketch(context, id + "F51", { "sketchPlane" : qUnion([Q0])});
            skText(sketch, "E897", { "text": "S2", "fontName": "OpenSans-Bold.ttf"});
            skText(sketch, "E898", { "text": "S3", "fontName": "OpenSans-Bold.ttf"});
            skText(sketch, "E899", { "text": "S1", "fontName": "OpenSans-Bold.ttf"});
            const initialGuessF51  = {"E897": [0.0049, 0.00582, 1, 0, 0.00474], "E898": [-0.01363, 0, 1, 0, 0.0043], "E899": [0.02768, 0.00016, 1, 0, 0.0043]};
            skSetInitialGuess(sketch, initialGuessF51);
            skSolve(sketch);
        }
        {
            var Q0;
            Q0 = qSketchRegion(id + "F51", true);
            extrude(context, id + "F52", {"entities" : qUnion([Q0]), "operationType" : NewBodyOperationType.ADD, "depth" : 1 * mm, "hasSecondDirection" : true, "secondDirectionOppositeDirection" : true, "secondDirectionDepth" : 1 * mm});
        }
        {
            var Q0;
            {var subQ0=sQuery(id+"F2.wireOp",EDGE,"E22");var subQ1=sQuery(id+"F2.wireOp",EDGE,"E20");Q0=makeQuery(id+"F38.boolean.opBoolean","MERGE",FACE,{"derivedFrom":[makeQuery(id+"F24.boolean.opBoolean","SPLIT",FACE,{"disambiguationData":[TD([makeQuery(id+"F1.opExtrude","SWEPT_FACE",FACE,{"disambiguationData":[OSD([sQuery(id+"F0.wireOp",EDGE,"E3")])]})])],"derivedFrom":makeQuery(id+"F3.boolean.opBoolean","COPY",FACE,{"derivedFrom":makeQuery(id+"F3.opExtrude","SWEPT_FACE",FACE,{"disambiguationData":[OSD([subQ1,subQ0])]})})}),makeQuery(id+"F38.opExtrude","CAP_FACE",FACE,{"disambiguationData":[OSD([sQuery(id+"F37.wireOp",EDGE,"E866")])],"isStart":false}),makeQuery(id+"F38.opExtrude","CAP_FACE",FACE,{"disambiguationData":[OSD([sQuery(id+"F37.wireOp",EDGE,"E867")])],"isStart":false})]});}
            var sketch = newSketch(context, id + "F53", { "sketchPlane" : qUnion([Q0])});
            skText(sketch, "E900", { "text": "S6", "fontName": "OpenSans-Bold.ttf"});
            const initialGuessF53  = {"E900": [0.00608, -0.02103, 1, 0, 0.00418]};
            skSetInitialGuess(sketch, initialGuessF53);
            skSolve(sketch);
        }
        {
            var Q0;
            Q0 = qSketchRegion(id + "F53", true);
            var Q1;
            Q1=makeQuery(id+"F4.opFillet","BLEND_FACE",FACE,{"disambiguationData":[OSD([sQuery(id+"F0.wireOp",EDGE,"E7.rect.left"),sQuery(id+"F2.wireOp",EDGE,"E20"),sQuery(id+"F2.wireOp",EDGE,"E22")])]});
            extrude(context, id + "F54", {"entities" : qUnion([Q0]), "operationType" : NewBodyOperationType.ADD, "depth" : 1 * mm, "hasSecondDirection" : true, "secondDirectionOppositeDirection" : true, "secondDirectionBoundEntityFace" : qUnion([Q1]), "secondDirectionDepth" : 1.6 * mm});
        }
        {
            var Q0;
            {var subQ1=sQuery(id+"F0.wireOp",EDGE,"E7.rect.left");var subQ3=sQuery(id+"F0.wireOp",EDGE,"E7.rect.bottom");Q0=makeQuery(id+"F9.boolean.opBoolean","SPLIT",FACE,{"disambiguationData":[TD([makeQuery(id+"F1.opExtrude","SWEPT_FACE",FACE,{"disambiguationData":[OSD([subQ3])]})])],"derivedFrom":makeQuery(id+"F1.opExtrude","SWEPT_FACE",FACE,{"disambiguationData":[OSD([subQ1])]})});}
            var sketch = newSketch(context, id + "F55", { "sketchPlane" : qUnion([Q0])});
            skText(sketch, "E901", { "text": "S5", "fontName": "OpenSans-Bold.ttf"});
            skText(sketch, "E902", { "text": "S4", "fontName": "OpenSans-Bold.ttf"});
            const initialGuessF55  = {"E901": [-0.02893, 0, 1, 0, 0.00488], "E902": [0.00624, 0, 1, 0, 0.0048]};
            skSetInitialGuess(sketch, initialGuessF55);
            skSolve(sketch);
        }
        {
            var Q0;
            Q0 = qSketchRegion(id + "F55", true);
            extrude(context, id + "F56", {"entities" : qUnion([Q0]), "operationType" : NewBodyOperationType.ADD, "depth" : 1.2 * mm});
        }
        {
            var Q0;
            {var subQ0=sQuery(id+"F12.wireOp",EDGE,"E51");Q0=makeQuery(id+"F12.imprint","IMPRINT",FACE,{"disambiguationData":[TD([[makeQuery(id+"F12.imprint","IMPRINT",EDGE,{"derivedFrom":subQ0}),-1.0]])]});}
            extrude(context, id + "F57", {"entities" : qUnion([Q0]), "operationType" : NewBodyOperationType.REMOVE, "oppositeDirection" : true, "depth" : 8 * mm});
        }
        {
            var Q0;
            Q0=makeQuery(id+"F0.imprint","IMPRINT",FACE,{"disambiguationData":[TD([[makeQuery(id+"F0.imprint","IMPRINT",EDGE,{"derivedFrom":sQuery(id+"F0.wireOp",EDGE,"E1")}),-1.0]])]});
            var sketch = newSketch(context, id + "F58", { "sketchPlane" : qUnion([Q0])});
            skPoint(sketch, "E903.first.point", {"position": v(6.62, 7.4) * mm});
            skPoint(sketch, "E903.second.point", {"position": v(6.67, 13.38) * mm});
            skPoint(sketch, "E903.third.point", {"position": v(3.73, 10.32) * mm});
            skPoint(sketch, "E904.first.point", {"position": v(17.45, 10.32) * mm});
            skPoint(sketch, "E904.second.point", {"position": v(14.7, 13.34) * mm});
            skPoint(sketch, "E904.third.point", {"position": v(14.7, 7.45) * mm});
            skPoint(sketch, "E905.MirrorP", {"position": v(17.5, 10.32) * mm});
            skPoint(sketch, "E906.MirrorP", {"position": v(14.62, 7.4) * mm});
            skPoint(sketch, "E907.MirrorP", {"position": v(14.57, 13.38) * mm});
            skLineSegment(sketch, "E908", {"start": v(14.46, 6.75) * mm, "end": v(6.63, 6.75) * mm});
            skLineSegment(sketch, "E909", {"start": v(14.66, 13.88) * mm, "end": v(6.96, 13.88) * mm});
            skArc(sketch, "E910.trimOffspring", {"start": v(6.96, 13.88) * mm, "mid": v(3.17, 10.38) * mm, "end": v(6.84, 6.75) * mm});
            skArc(sketch, "E911.trimOffspring", {"start": v(14.27, 13.88) * mm, "mid": v(18.08, 10.42) * mm, "end": v(14.46, 6.75) * mm});
            skPoint(sketch, "E912.orphan", {"position": v(14.5, 10.4) * mm});
            skPoint(sketch, "E913.start.orphan", {"position": v(10.62, 10.36) * mm});
            skCircle(sketch, "E914", {"center": v(6.74, 10.32) * mm, "radius": 2.01 * mm});
            skCircle(sketch, "E915", {"center": v(14.51, 10.32) * mm, "radius": 2.16 * mm});
            skLineSegment(sketch, "E916.trimOffspring", {"start": v(6.52, 13.88) * mm, "end": v(6.5, 13.88) * mm});
            skSolve(sketch);
        }
        {
            var Q0;
            Q0 = qSketchRegion(id + "F58", true);
            extrude(context, id + "F59", {"entities" : qUnion([Q0]), "operationType" : NewBodyOperationType.REMOVE, "depth" : 8.2 * mm});
        }
    });
